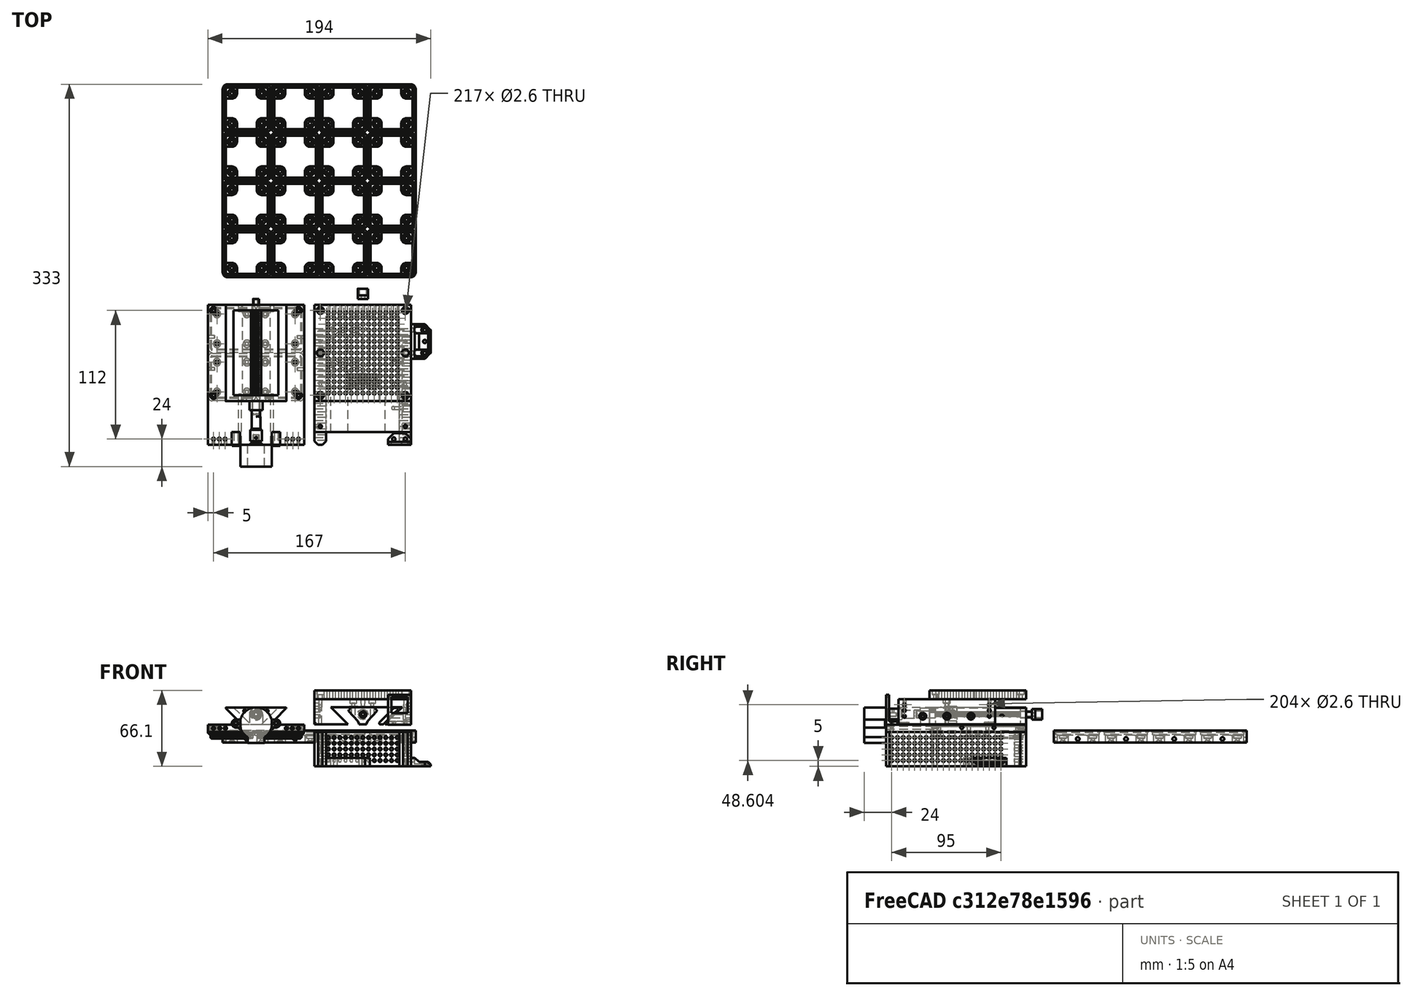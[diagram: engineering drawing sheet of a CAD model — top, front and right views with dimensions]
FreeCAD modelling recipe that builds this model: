
FCSTD DOCUMENT  (FreeCAD 1.0R39109 (Git))
Label: Linear Stage Motorised
License: All rights reserved
LicenseURL: https://en.wikipedia.org/wiki/All_rights_reserved
objects: Sketcher::SketchObject×99, PartDesign::Pocket×54, PartDesign::Pad×44, PartDesign::Chamfer×26, PartDesign::Plane×17, PartDesign::Body×16, PartDesign::ShapeBinder×15, PartDesign::Fillet×6, PartDesign::SubShapeBinder×5, PartDesign::Hole×3, PartDesign::FeatureBase×3, PartDesign::LinearPattern×3, PartDesign::Point×1, Part::Part2DObjectPython×1, Part::Helix×1, PartDesign::AdditivePipe×1, Part::FeaturePython×1, App::VarSet×1, PartDesign::FeaturePython×1
note: 671 computed .brp shape members not serialized (recipe doc carries the construction recipe); baked Part::Feature solids carry a one-line shape summary decoded from their .brp

FEATURE [Sketcher::SketchObject] Sketch
  ArcFitTolerance = 1e-06
  AttachmentSupport = -> [XZ_Plane]
  FullyConstrained = true
  MakeInternals = false
  MapMode = 5
  Placement = pos=(0,0,0) rot=(1,0,0;1.5708rad)
  sketch-geometry (8):
    g0: LineSegment StartX=0 StartY=0 StartZ=0 EndX=84 EndY=0 EndZ=0
    g1: LineSegment StartX=0 StartY=0 StartZ=0 EndX=0 EndY=5 EndZ=0
    g2: LineSegment StartX=84 StartY=0 StartZ=0 EndX=84 EndY=5 EndZ=0
    g3: LineSegment StartX=0 StartY=5 StartZ=0 EndX=30 EndY=5 EndZ=0
    g4: LineSegment StartX=84 StartY=5 StartZ=0 EndX=54 EndY=5 EndZ=0
    g5: LineSegment StartX=30 StartY=5 StartZ=0 EndX=15 EndY=20 EndZ=0
    g6: LineSegment StartX=54 StartY=5 StartZ=0 EndX=69 EndY=20 EndZ=0
    g7: LineSegment StartX=15 StartY=20 StartZ=0 EndX=69 EndY=20 EndZ=0
  constraints (24):
    c: Distance(g0) = 84
    c: Distance(g1) = 5
    c: Coincident(g1,g0)
    c: PointOnObject(g1,g-2)
    c: Vertical(g1)
    c: Distance(g2) = 5
    c: Vertical(g2)
    c: Tangent(g0,g-1)
    c: PointOnObject(g2,g0)
    c: PointOnObject(g0,g2)
    c: Coincident(g3,g1)
    c: Horizontal(g3)
    c: Coincident(g4,g2)
    c: Horizontal(g4)
    c: DistanceX(g3,g3) = 30
    c: DistanceX(g4,g4) = 30
    c: Angle(g-1,g5) = 2.35619
    c: Coincident(g5,g3)
    c: Angle(g-1,g6) = 0.785398
    c: Coincident(g6,g4)
    c: DistanceY(g-1,g5) = 20
    c: DistanceY(g-1,g6) = 20
    c: Coincident(g7,g5)
    c: Coincident(g7,g6)
FEATURE [PartDesign::Pad] Pad
  Direction = (0,-1,2e-16)
  Length = 5
  Length2 = 10
  Placement = pos=(0,0,0) rot=(1,0,0;1.5708rad)
  Profile = -> Sketch
  ReferenceAxis = -> Sketch [N_Axis]
  Refine = true
  Suppressed = false
  Type = 0
FEATURE [Sketcher::SketchObject] Sketch001
  ArcFitTolerance = 1e-06
  AttachmentSupport = -> [Pad]
  ExternalGeometry = -> [Pad]
  FullyConstrained = true
  MakeInternals = false
  MapMode = 5
  Placement = pos=(0,-5,0) rot=(1,0,0;1.5708rad)
  sketch-geometry (14):
    g0: LineSegment StartX=15 StartY=20 StartZ=0 EndX=22.5 EndY=20 EndZ=0
    g1: LineSegment [constr] StartX=30 StartY=5 StartZ=0 EndX=37.5 EndY=5 EndZ=0
    g2: LineSegment StartX=22.5 StartY=20 StartZ=0 EndX=37.5 EndY=5 EndZ=0
    g3: LineSegment StartX=69 StartY=20 StartZ=0 EndX=61.5 EndY=20 EndZ=0
    g4: LineSegment [constr] StartX=54 StartY=5 StartZ=0 EndX=46.5 EndY=5 EndZ=0
    g5: LineSegment StartX=46.5 StartY=5 StartZ=0 EndX=61.5 EndY=20 EndZ=0
    g6: LineSegment StartX=46.5 StartY=5 StartZ=0 EndX=37.5 EndY=5 EndZ=0
    g7: LineSegment StartX=15 StartY=20 StartZ=0 EndX=30 EndY=5 EndZ=0
    g8: LineSegment StartX=30 StartY=5 StartZ=0 EndX=0 EndY=5 EndZ=0
    g9: LineSegment StartX=0 StartY=5 StartZ=0 EndX=0 EndY=0 EndZ=0
    g10: LineSegment StartX=0 StartY=0 StartZ=0 EndX=84 EndY=0 EndZ=0
    g11: LineSegment StartX=84 StartY=0 StartZ=0 EndX=84 EndY=5 EndZ=0
    g12: LineSegment StartX=84 StartY=5 StartZ=0 EndX=54 EndY=5 EndZ=0
    g13: LineSegment StartX=54 StartY=5 StartZ=0 EndX=69 EndY=20 EndZ=0
  constraints (32):
    c: Distance(g0) = 7.5
    c: Coincident(g0,g-4)
    c: PointOnObject(g0,g-3)
    c: Distance(g1) = 7.5
    c: Coincident(g1,g-5)
    c: Horizontal(g1)
    c: Coincident(g2,g0)
    c: Coincident(g2,g1)
    c: Distance(g3) = 7.5
    c: Coincident(g3,g-3)
    c: PointOnObject(g3,g-3)
    c: Distance(g4) = 7.5
    c: Coincident(g4,g-6)
    c: Horizontal(g4)
    c: Coincident(g5,g4)
    c: Coincident(g5,g3)
    c: Coincident(g6,g4)
    c: Coincident(g6,g1)
    c: Coincident(g7,g0)
    c: Coincident(g7,g1)
    c: Coincident(g8,g1)
    c: Coincident(g8,g-8)
    c: Coincident(g9,g8)
    c: Coincident(g9,g-1)
    c: Coincident(g10,g9)
    c: Coincident(g10,g-9)
    c: Coincident(g11,g10)
    c: Coincident(g11,g-7)
    c: Coincident(g12,g11)
    c: Coincident(g12,g4)
    c: Coincident(g13,g4)
    c: Coincident(g13,g3)
FEATURE [PartDesign::Pad] Pad001
  BaseFeature = -> Pad
  Direction = (0,-1,2e-16)
  Length = 74
  Length2 = 10
  Placement = pos=(0,0,0) rot=(1,0,0;1.5708rad)
  Profile = -> Sketch001
  ReferenceAxis = -> Sketch001 [N_Axis]
  Refine = true
  Suppressed = false
  Type = 0
FEATURE [Sketcher::SketchObject] Sketch002
  ArcFitTolerance = 1e-06
  AttachmentSupport = -> [Pad001]
  ExternalGeometry = -> [Pad001]
  FullyConstrained = true
  MakeInternals = false
  MapMode = 5
  Placement = pos=(0,-5,0) rot=(1,0,0;1.5708rad)
  sketch-geometry (2):
    g0: LineSegment [constr] StartX=42 StartY=20 StartZ=0 EndX=42 EndY=14 EndZ=0
    g1: Circle CenterX=42 CenterY=14 CenterZ=0 NormalX=0 NormalY=0 NormalZ=1 AngleXU=0 Radius=3
  constraints (5):
    c: Distance(g0) = 6
    c: Symmetric(g-3,g-3,g0)
    c: Vertical(g0)
    c: Diameter(g1) = 6
    c: Coincident(g1,g0)
FEATURE [PartDesign::Hole] Hole
  BaseFeature = -> Pad001
  CustomThreadClearance = 0
  Depth = 25
  DepthType = 0
  Diameter = 6
  DrillForDepth = false
  DrillPoint = 1
  DrillPointAngle = 118
  HoleCutCountersinkAngle = 90
  HoleCutCustomValues = false
  HoleCutDepth = 0
  HoleCutDiameter = 6.1
  HoleCutType = 0
  ModelThread = false
  Placement = pos=(0,0,0) rot=(1,0,0;1.5708rad)
  Profile = -> Sketch002
  Refine = true
  Suppressed = false
  Tapered = false
  TaperedAngle = 90
  ThreadClass = 0
  ThreadDepth = 25
  ThreadDepthType = 0
  ThreadDirection = 0
  ThreadFit = 0
  ThreadSize = 0
  ThreadType = 0
  Threaded = false
  UseCustomThreadClearance = false
FEATURE [Sketcher::SketchObject] Sketch003
  ArcFitTolerance = 1e-06
  AttachmentSupport = -> [Hole]
  ExternalGeometry = -> [Hole]
  FullyConstrained = true
  MakeInternals = false
  MapMode = 5
  Placement = pos=(0,-79,1.74e-14) rot=(1,0,0;1.5708rad)
  sketch-geometry (16):
    g0: LineSegment StartX=15 StartY=20 StartZ=0 EndX=69 EndY=20 EndZ=0
    g1: LineSegment StartX=15 StartY=20 StartZ=0 EndX=30 EndY=5 EndZ=0
    g2: LineSegment StartX=30 StartY=5 StartZ=0 EndX=0 EndY=5 EndZ=0
    g3: LineSegment StartX=0 StartY=5 StartZ=0 EndX=0 EndY=0 EndZ=0
    g4: LineSegment StartX=0 StartY=0 StartZ=0 EndX=84 EndY=0 EndZ=0
    g5: LineSegment StartX=84 StartY=0 StartZ=0 EndX=84 EndY=5 EndZ=0
    g6: LineSegment StartX=84 StartY=5 StartZ=0 EndX=54 EndY=5 EndZ=0
    g7: LineSegment StartX=54 StartY=5 StartZ=0 EndX=69 EndY=20 EndZ=0
    g8: LineSegment [constr] StartX=42 StartY=20 StartZ=0 EndX=42 EndY=14 EndZ=0
    g9: Circle CenterX=42 CenterY=14 CenterZ=0 NormalX=0 NormalY=0 NormalZ=1 AngleXU=0 Radius=3
    g10: LineSegment [constr] StartX=42 StartY=14 StartZ=0 EndX=22.5 EndY=20 EndZ=0
    g11: LineSegment [constr] StartX=42 StartY=14 StartZ=0 EndX=61.5 EndY=20 EndZ=0
    g12: GeomPoint [constr] X=32.25 Y=17 Z=0
    g13: GeomPoint [constr] X=51.75 Y=17 Z=0
    g14: Circle CenterX=32.25 CenterY=17 CenterZ=0 NormalX=0 NormalY=0 NormalZ=1 AngleXU=0 Radius=1.25
    g15: Circle CenterX=51.75 CenterY=17 CenterZ=0 NormalX=0 NormalY=0 NormalZ=1 AngleXU=0 Radius=1.25
  constraints (31):
    c: Coincident(g0,g-4)
    c: Coincident(g0,g-11)
    c: Coincident(g1,g0)
    c: Coincident(g1,g-5)
    c: Coincident(g2,g1)
    c: Coincident(g2,g-6)
    c: Coincident(g3,g2)
    c: Coincident(g3,g-1)
    c: Coincident(g4,g3)
    c: Coincident(g4,g-8)
    c: Coincident(g5,g4)
    c: Coincident(g5,g-9)
    c: Coincident(g6,g5)
    c: Coincident(g6,g-10)
    c: Coincident(g7,g6)
    c: Coincident(g7,g0)
    c: Distance(g8) = 6
    c: Symmetric(g0,g0,g8)
    c: Vertical(g8)
    c: Diameter(g9) = 6
    c: Coincident(g9,g8)
    c: Coincident(g10,g8)
    c: Coincident(g10,g-14)
    c: Coincident(g11,g8)
    c: Coincident(g11,g-12)
    c: Symmetric(g10,g10,g12)
    c: Symmetric(g11,g11,g13)
    c: Diameter(g14) = 2.5
    c: Coincident(g14,g12)
    c: Diameter(g15) = 2.5
    c: Coincident(g15,g13)
FEATURE [PartDesign::Pad] Pad002
  BaseFeature = -> Hole
  Direction = (0,-1,2e-16)
  Length = 5
  Length2 = 10
  Placement = pos=(0,0,0) rot=(1,0,0;1.5708rad)
  Profile = -> Sketch003
  ReferenceAxis = -> Sketch003 [N_Axis]
  Refine = true
  Suppressed = false
  Type = 0
FEATURE [PartDesign::Plane] DatumPlane
  AttachmentSupport = -> [Pad002]
  Length = 131.586
  MapMode = 5
  Placement = pos=(0,0,-5e-16) rot=(1,0,0;3.14159rad)
  ResizeMode = 0
  Width = 139.586
FEATURE [Sketcher::SketchObject] Sketch004
  ArcFitTolerance = 1e-06
  AttachmentSupport = -> [Pad002]
  ExternalGeometry = -> [Pad002]
  FullyConstrained = true
  MakeInternals = false
  MapMode = 5
  Placement = pos=(0,0,-5e-16) rot=(1,0,0;3.14159rad)
  sketch-geometry (23):
    g0: LineSegment [constr] StartX=0 StartY=84 StartZ=0 EndX=84 EndY=0 EndZ=0
    g1: LineSegment [constr] StartX=41.75 StartY=41.75 StartZ=0 EndX=42.25 EndY=41.75 EndZ=0
    g2: LineSegment [constr] StartX=42.25 StartY=41.75 StartZ=0 EndX=42.25 EndY=42.25 EndZ=0
    g3: LineSegment [constr] StartX=42.25 StartY=42.25 StartZ=0 EndX=41.75 EndY=42.25 EndZ=0
    g4: LineSegment [constr] StartX=41.75 StartY=42.25 StartZ=0 EndX=41.75 EndY=41.75 EndZ=0
    g5: GeomPoint [constr] X=42 Y=42 Z=0
    g6: LineSegment [constr] StartX=0 StartY=0 StartZ=0 EndX=84 EndY=84 EndZ=0
    g7: LineSegment StartX=42.25 StartY=42.25 StartZ=0 EndX=83.75 EndY=42.25 EndZ=0
    g8: LineSegment StartX=83.75 StartY=42.25 StartZ=0 EndX=83.75 EndY=83.75 EndZ=0
    g9: LineSegment StartX=83.75 StartY=83.75 StartZ=0 EndX=42.25 EndY=83.75 EndZ=0
    g10: LineSegment StartX=42.25 StartY=83.75 StartZ=0 EndX=42.25 EndY=42.25 EndZ=0
    g11: LineSegment StartX=41.75 StartY=42.25 StartZ=0 EndX=41.75 EndY=83.75 EndZ=0
    g12: LineSegment StartX=41.75 StartY=83.75 StartZ=0 EndX=0.25 EndY=83.75 EndZ=0
    g13: LineSegment StartX=0.25 StartY=83.75 StartZ=0 EndX=0.25 EndY=42.25 EndZ=0
    g14: LineSegment StartX=0.25 StartY=42.25 StartZ=0 EndX=41.75 EndY=42.25 EndZ=0
    g15: LineSegment StartX=42.25 StartY=41.75 StartZ=0 EndX=42.25 EndY=0.25 EndZ=0
    g16: LineSegment StartX=42.25 StartY=0.25 StartZ=0 EndX=83.75 EndY=0.25 EndZ=0
    g17: LineSegment StartX=83.75 StartY=0.25 StartZ=0 EndX=83.75 EndY=41.75 EndZ=0
    g18: LineSegment StartX=83.75 StartY=41.75 StartZ=0 EndX=42.25 EndY=41.75 EndZ=0
    g19: LineSegment StartX=41.75 StartY=41.75 StartZ=0 EndX=0.25 EndY=41.75 EndZ=0
    g20: LineSegment StartX=0.25 StartY=41.75 StartZ=0 EndX=0.25 EndY=0.25 EndZ=0
    g21: LineSegment StartX=0.25 StartY=0.25 StartZ=0 EndX=41.75 EndY=0.25 EndZ=0
    g22: LineSegment StartX=41.75 StartY=0.25 StartZ=0 EndX=41.75 EndY=41.75 EndZ=0
  constraints (61):
    c: Coincident(g0,g-6)
    c: Coincident(g0,g-5)
    c: Coincident(g1,g2)
    c: Coincident(g2,g3)
    c: Coincident(g3,g4)
    c: Coincident(g4,g1)
    c: Horizontal(g1)
    c: Horizontal(g3)
    c: Vertical(g2)
    c: Vertical(g4)
    c: Symmetric(g3,g1,g5)
    c: Distance(g2,g4) = 0.5
    c: Distance(g1,g3) = 0.5
    c: PointOnObject(g5,g0)
    c: Coincident(g6,g-1)
    c: Coincident(g6,g-4)
    c: PointOnObject(g5,g6)
    c: Coincident(g7,g8)
    c: Coincident(g8,g9)
    c: Coincident(g9,g10)
    c: Coincident(g10,g7)
    c: Horizontal(g7)
    c: Horizontal(g9)
    c: Vertical(g8)
    c: Vertical(g10)
    c: Distance(g8,g10) = 41.5
    c: Coincident(g7,g2)
    c: PointOnObject(g8,g6)
    c: Coincident(g11,g12)
    c: Coincident(g12,g13)
    c: Coincident(g13,g14)
    c: Coincident(g14,g11)
    c: Vertical(g11)
    c: Vertical(g13)
    c: Horizontal(g12)
    c: Horizontal(g14)
    c: Distance(g11,g13) = 41.5
    c: Coincident(g11,g3)
    c: PointOnObject(g12,g0)
    c: Coincident(g15,g16)
    c: Coincident(g16,g17)
    c: Coincident(g17,g18)
    c: Coincident(g18,g15)
    c: Vertical(g15)
    c: Vertical(g17)
    c: Horizontal(g16)
    c: Horizontal(g18)
    c: Distance(g15,g17) = 41.5
    c: Coincident(g15,g1)
    c: PointOnObject(g16,g0)
    c: Coincident(g19,g20)
    c: Coincident(g20,g21)
    c: Coincident(g21,g22)
    c: Coincident(g22,g19)
    c: Horizontal(g19)
    c: Horizontal(g21)
    c: Vertical(g20)
    c: Vertical(g22)
    c: Distance(g20,g22) = 41.5
    c: Coincident(g19,g1)
    c: PointOnObject(g20,g6)
FEATURE [PartDesign::Pad] Pad003
  BaseFeature = -> Pad002
  Direction = (0,0,-1)
  Length = 1
  Length2 = 10
  Placement = pos=(0,0,0) rot=(1,0,0;1.5708rad)
  Profile = -> Sketch004
  ReferenceAxis = -> Sketch004 [N_Axis]
  Refine = true
  Suppressed = false
  Type = 0
FEATURE [PartDesign::Plane] DatumPlane001
  AttachmentSupport = -> [Pad003]
  Length = 131.586
  MapMode = 5
  Placement = pos=(0,0,-1) rot=(1,0,0;3.14159rad)
  ResizeMode = 0
  Width = 139.586
FEATURE [Sketcher::SketchObject] Sketch005
  ArcFitTolerance = 1e-06
  AttachmentSupport = -> [DatumPlane001]
  ExternalGeometry = -> [Pad003]
  FullyConstrained = true
  MakeInternals = false
  MapMode = 5
  Placement = pos=(0,0,-1) rot=(1,0,0;3.14159rad)
  sketch-geometry (28):
    g0: LineSegment [constr] StartX=41.75 StartY=42.25 StartZ=0 EndX=0.25 EndY=83.75 EndZ=0
    g1: GeomPoint [constr] X=21 Y=63 Z=0
    g2: LineSegment StartX=2.4 StartY=44.4 StartZ=0 EndX=39.6 EndY=44.4 EndZ=0
    g3: LineSegment StartX=39.6 StartY=44.4 StartZ=0 EndX=39.6 EndY=81.6 EndZ=0
    g4: LineSegment StartX=39.6 StartY=81.6 StartZ=0 EndX=2.4 EndY=81.6 EndZ=0
    g5: LineSegment StartX=2.4 StartY=81.6 StartZ=0 EndX=2.4 EndY=44.4 EndZ=0
    g6: GeomPoint [constr] X=21 Y=63 Z=0
    g7: LineSegment [constr] StartX=42.25 StartY=83.75 StartZ=0 EndX=83.75 EndY=42.25 EndZ=0
    g8: LineSegment [constr] StartX=83.75 StartY=41.75 StartZ=0 EndX=42.25 EndY=0.25 EndZ=0
    g9: LineSegment [constr] StartX=41.75 StartY=0.25 StartZ=0 EndX=0.25 EndY=41.75 EndZ=0
    g10: GeomPoint [constr] X=63 Y=63 Z=0
    g11: GeomPoint [constr] X=63 Y=21 Z=0
    g12: GeomPoint [constr] X=21 Y=21 Z=0
    g13: LineSegment StartX=44.4 StartY=44.4 StartZ=0 EndX=81.6 EndY=44.4 EndZ=0
    g14: LineSegment StartX=81.6 StartY=44.4 StartZ=0 EndX=81.6 EndY=81.6 EndZ=0
    g15: LineSegment StartX=81.6 StartY=81.6 StartZ=0 EndX=44.4 EndY=81.6 EndZ=0
    g16: LineSegment StartX=44.4 StartY=81.6 StartZ=0 EndX=44.4 EndY=44.4 EndZ=0
    g17: GeomPoint [constr] X=63 Y=63 Z=0
    g18: LineSegment StartX=44.4 StartY=2.4 StartZ=0 EndX=81.6 EndY=2.4 EndZ=0
    g19: LineSegment StartX=81.6 StartY=2.4 StartZ=0 EndX=81.6 EndY=39.6 EndZ=0
    g20: LineSegment StartX=81.6 StartY=39.6 StartZ=0 EndX=44.4 EndY=39.6 EndZ=0
    g21: LineSegment StartX=44.4 StartY=39.6 StartZ=0 EndX=44.4 EndY=2.4 EndZ=0
    g22: GeomPoint [constr] X=63 Y=21 Z=0
    g23: LineSegment StartX=2.4 StartY=2.4 StartZ=0 EndX=39.6 EndY=2.4 EndZ=0
    g24: LineSegment StartX=39.6 StartY=2.4 StartZ=0 EndX=39.6 EndY=39.6 EndZ=0
    g25: LineSegment StartX=39.6 StartY=39.6 StartZ=0 EndX=2.4 EndY=39.6 EndZ=0
    g26: LineSegment StartX=2.4 StartY=39.6 StartZ=0 EndX=2.4 EndY=2.4 EndZ=0
    g27: GeomPoint [constr] X=21 Y=21 Z=0
  constraints (60):
    c: Coincident(g0,g-14)
    c: Coincident(g0,g-16)
    c: Symmetric(g0,g0,g1)
    c: Coincident(g2,g3)
    c: Coincident(g3,g4)
    c: Coincident(g4,g5)
    c: Coincident(g5,g2)
    c: Horizontal(g2)
    c: Horizontal(g4)
    c: Vertical(g3)
    c: Vertical(g5)
    c: Symmetric(g4,g2,g6)
    c: Distance(g3,g5) = 37.2
    c: Distance(g2,g4) = 37.2
    c: Coincident(g6,g1)
    c: Coincident(g7,g-18)
    c: Coincident(g7,g-17)
    c: Coincident(g8,g-9)
    c: Coincident(g8,g-10)
    c: Coincident(g9,g-4)
    c: Coincident(g9,g-6)
    c: Symmetric(g7,g7,g10)
    c: Symmetric(g8,g8,g11)
    c: Symmetric(g9,g9,g12)
    c: Coincident(g13,g14)
    c: Coincident(g14,g15)
    c: Coincident(g15,g16)
    c: Coincident(g16,g13)
    c: Horizontal(g13)
    c: Horizontal(g15)
    c: Vertical(g14)
    c: Vertical(g16)
    c: Symmetric(g15,g13,g17)
    c: Distance(g14,g16) = 37.2
    c: Distance(g13,g15) = 37.2
    c: Coincident(g17,g10)
    c: Coincident(g18,g19)
    c: Coincident(g19,g20)
    c: Coincident(g20,g21)
    c: Coincident(g21,g18)
    c: Horizontal(g18)
    c: Horizontal(g20)
    c: Vertical(g19)
    c: Vertical(g21)
    c: Symmetric(g20,g18,g22)
    c: Distance(g19,g21) = 37.2
    c: Coincident(g22,g11)
    c: PointOnObject(g19,g8)
    c: Coincident(g23,g24)
    c: Coincident(g24,g25)
    c: Coincident(g25,g26)
    c: Coincident(g26,g23)
    c: Horizontal(g23)
    c: Horizontal(g25)
    c: Vertical(g24)
    c: Vertical(g26)
    c: Symmetric(g25,g23,g27)
    c: Distance(g24,g26) = 37.2
    c: Distance(g23,g25) = 37.2
    c: Coincident(g27,g12)
FEATURE [PartDesign::Pad] Pad004
  BaseFeature = -> Pad003
  Direction = (0,0,-1)
  Length = 3.5
  Length2 = 10
  Placement = pos=(0,0,0) rot=(1,0,0;1.5708rad)
  Profile = -> Sketch005
  ReferenceAxis = -> Sketch005 [N_Axis]
  Refine = true
  Suppressed = false
  Type = 0
FEATURE [PartDesign::Chamfer] Chamfer
  Angle = 45
  Base = -> Pad004 [Edge114]
  BaseFeature = -> Pad004
  ChamferType = 0
  FlipDirection = false
  Placement = pos=(0,0,0) rot=(1,0,0;1.5708rad)
  Refine = true
  Size = 7
  Size2 = 1
  SupportTransform = false
  Suppressed = false
  UseAllEdges = false
FEATURE [PartDesign::Chamfer] Chamfer001
  Angle = 45
  Base = -> Chamfer [Edge23]
  BaseFeature = -> Chamfer
  ChamferType = 0
  FlipDirection = false
  Placement = pos=(0,0,0) rot=(1,0,0;1.5708rad)
  Refine = true
  Size = 7
  Size2 = 1
  SupportTransform = false
  Suppressed = false
  UseAllEdges = false
FEATURE [PartDesign::Chamfer] Chamfer002
  Angle = 45
  Base = -> Chamfer001 [Edge136,Edge28,Edge143,Edge22,Edge135,Edge128,Edge144,Edge148,Edge140,Edge127,Edge132,Edge138,Edge26,Edge130]
  BaseFeature = -> Chamfer001
  ChamferType = 0
  FlipDirection = false
  Placement = pos=(0,0,0) rot=(1,0,0;1.5708rad)
  Refine = true
  Size = 7
  Size2 = 1
  SupportTransform = false
  Suppressed = false
  UseAllEdges = false
FEATURE [PartDesign::Chamfer] Chamfer003
  Angle = 45
  Base = -> Chamfer002 [Edge77,Edge79,Edge93,Edge81,Edge95,Edge38,Edge76,Edge32,Edge92,Edge84,Edge97,Edge85,Edge87,Edge89,Edge35]
  BaseFeature = -> Chamfer002
  ChamferType = 0
  FlipDirection = false
  Placement = pos=(0,0,0) rot=(1,0,0;1.5708rad)
  Refine = true
  Size = 8
  Size2 = 1
  SupportTransform = false
  Suppressed = false
  UseAllEdges = false
FEATURE [PartDesign::Chamfer] Chamfer004
  Angle = 45
  Base = -> Chamfer003 [Edge231]
  BaseFeature = -> Chamfer003
  ChamferType = 0
  FlipDirection = false
  Placement = pos=(0,0,0) rot=(1,0,0;1.5708rad)
  Refine = true
  Size = 7
  Size2 = 1
  SupportTransform = false
  Suppressed = false
  UseAllEdges = false
FEATURE [PartDesign::Chamfer] Chamfer005
  Angle = 45
  Base = -> Chamfer004 [Edge1,Edge2,Edge4,Edge6,Edge8,Edge7,Edge5,Edge3]
  BaseFeature = -> Chamfer004
  ChamferType = 0
  FlipDirection = false
  Placement = pos=(0,0,0) rot=(1,0,0;1.5708rad)
  Refine = true
  Size = 2
  Size2 = 1
  SupportTransform = false
  Suppressed = false
  UseAllEdges = false
FEATURE [PartDesign::Chamfer] Chamfer006
  Angle = 45
  Base = -> Chamfer005 [Edge60,Edge64,Edge62,Edge58,Edge55,Edge50,Edge52,Edge56]
  BaseFeature = -> Chamfer005
  ChamferType = 0
  FlipDirection = false
  Placement = pos=(0,0,0) rot=(1,0,0;1.5708rad)
  Refine = true
  Size = 0.8
  Size2 = 1
  SupportTransform = false
  Suppressed = false
  UseAllEdges = false
FEATURE [PartDesign::Chamfer] Chamfer007
  Angle = 45
  Base = -> Chamfer006 [Edge207,Edge208,Edge205,Edge206,Edge204,Edge202,Edge203,Edge201]
  BaseFeature = -> Chamfer006
  ChamferType = 0
  FlipDirection = false
  Placement = pos=(0,0,0) rot=(1,0,0;1.5708rad)
  Refine = true
  Size = 2
  Size2 = 1
  SupportTransform = false
  Suppressed = false
  UseAllEdges = false
FEATURE [PartDesign::Chamfer] Chamfer008
  Angle = 45
  Base = -> Chamfer007 [Edge63,Edge64,Edge60,Edge57,Edge52,Edge50,Edge55,Edge59]
  BaseFeature = -> Chamfer007
  ChamferType = 0
  FlipDirection = false
  Placement = pos=(0,0,0) rot=(1,0,0;1.5708rad)
  Refine = true
  Size = 0.8
  Size2 = 1
  SupportTransform = false
  Suppressed = false
  UseAllEdges = false
FEATURE [PartDesign::Chamfer] Chamfer009
  Angle = 45
  Base = -> Chamfer008 [Edge179,Edge177,Edge178,Edge181,Edge180,Edge182,Edge184,Edge183]
  BaseFeature = -> Chamfer008
  ChamferType = 0
  FlipDirection = false
  Placement = pos=(0,0,0) rot=(1,0,0;1.5708rad)
  Refine = true
  Size = 2
  Size2 = 1
  SupportTransform = false
  Suppressed = false
  UseAllEdges = false
FEATURE [PartDesign::Chamfer] Chamfer010
  Angle = 45
  Base = -> Chamfer009 [Edge55,Edge58,Edge62,Edge64,Edge61,Edge56,Edge53,Edge50]
  BaseFeature = -> Chamfer009
  ChamferType = 0
  FlipDirection = false
  Placement = pos=(0,0,0) rot=(1,0,0;1.5708rad)
  Refine = true
  Size = 0.8
  Size2 = 1
  SupportTransform = false
  Suppressed = false
  UseAllEdges = false
FEATURE [PartDesign::Chamfer] Chamfer011
  Angle = 45
  Base = -> Chamfer010 [Edge203,Edge205,Edge201,Edge202,Edge204,Edge206,Edge208,Edge207]
  BaseFeature = -> Chamfer010
  ChamferType = 0
  FlipDirection = false
  Placement = pos=(0,0,0) rot=(1,0,0;1.5708rad)
  Refine = true
  Size = 2
  Size2 = 1
  SupportTransform = false
  Suppressed = false
  UseAllEdges = false
FEATURE [PartDesign::Chamfer] Chamfer012
  Angle = 45
  Base = -> Chamfer011 [Edge62,Edge59,Edge54,Edge50,Edge53,Edge56,Edge61,Edge64]
  BaseFeature = -> Chamfer011
  ChamferType = 0
  FlipDirection = false
  Placement = pos=(0,0,0) rot=(1,0,0;1.5708rad)
  Refine = true
  Size = 0.8
  Size2 = 1
  SupportTransform = false
  Suppressed = false
  UseAllEdges = false
FEATURE [PartDesign::Fillet] Fillet
  Base = -> Chamfer012 [Edge188,Edge187]
  BaseFeature = -> Chamfer012
  Placement = pos=(0,0,0) rot=(1,0,0;1.5708rad)
  Radius = 0.5
  Refine = true
  SupportTransform = false
  Suppressed = false
  UseAllEdges = false
FEATURE [PartDesign::ShapeBinder] ShapeBinder
  Support = -> [Fillet]
  TraceSupport = false
FEATURE [PartDesign::ShapeBinder] CopyFillet
  Placement = pos=(0,-5,2e-15) rot=(0,0,1;0rad)
  TraceSupport = false
FEATURE [PartDesign::Plane] DatumPlane002
  AttachmentSupport = -> [CopyFillet]
  Length = 111.71
  MapMode = 5
  Placement = pos=(0,-84,2e-15) rot=(1,0,0;1.5708rad)
  ResizeMode = 0
  Width = 63.9806
FEATURE [Sketcher::SketchObject] Sketch006
  ArcFitTolerance = 1e-06
  AttachmentSupport = -> [DatumPlane002]
  ExternalGeometry = -> [ShapeBinder]
  FullyConstrained = true
  MakeInternals = false
  MapMode = 5
  Placement = pos=(0,-84,2e-15) rot=(1,0,0;1.5708rad)
  sketch-geometry (16):
    g0: LineSegment [constr] StartX=68.1465 StartY=19.1464 StartZ=0 EndX=69 EndY=20 EndZ=0
    g1: LineSegment [constr] StartX=67.7929 StartY=20 StartZ=0 EndX=69 EndY=20 EndZ=0
    g2: LineSegment [constr] StartX=69 StartY=20 StartZ=0 EndX=69.5 EndY=20 EndZ=0
    g3: LineSegment [constr] StartX=69.5 StartY=20 StartZ=0 EndX=74.5 EndY=20 EndZ=0
    g4: LineSegment [constr] StartX=54 StartY=5 StartZ=0 EndX=54.5 EndY=5 EndZ=0
    g5: LineSegment [constr] StartX=54.5 StartY=5 StartZ=0 EndX=59.5 EndY=5 EndZ=0
    g6: LineSegment [constr] StartX=59.5 StartY=5 StartZ=0 EndX=74.5 EndY=20 EndZ=0
    g7: LineSegment [constr] StartX=54.5 StartY=5 StartZ=0 EndX=69.5 EndY=20 EndZ=0
    g8: LineSegment [constr] StartX=59.5 StartY=5 StartZ=0 EndX=59.8536 EndY=5.35355 EndZ=0
    g9: LineSegment [constr] StartX=54.5 StartY=5 StartZ=0 EndX=54.8536 EndY=5.35355 EndZ=0
    g10: LineSegment [constr] StartX=74.5 StartY=20 StartZ=0 EndX=74.1465 EndY=19.6464 EndZ=0
    g11: LineSegment [constr] StartX=69.5 StartY=20 StartZ=0 EndX=69.1465 EndY=19.6464 EndZ=0
    g12: LineSegment StartX=54.8536 StartY=5.35355 StartZ=0 EndX=59.8536 EndY=5.35355 EndZ=0
    g13: LineSegment StartX=59.8536 StartY=5.35355 StartZ=0 EndX=74.1465 EndY=19.6464 EndZ=0
    g14: LineSegment StartX=74.1465 StartY=19.6464 StartZ=0 EndX=69.1465 EndY=19.6464 EndZ=0
    g15: LineSegment StartX=69.1465 StartY=19.6464 StartZ=0 EndX=54.8536 EndY=5.35355 EndZ=0
  constraints (41):
    c: Coincident(g0,g-3)
    c: Coincident(g1,g-4)
    c: Coincident(g1,g0)
    c: Angle(g-4,g1) = 3.14159
    c: Angle(g-3,g0) = 3.14159
    c: Distance(g2) = 0.5
    c: Coincident(g2,g0)
    c: Horizontal(g2)
    c: Distance(g3) = 5
    c: Coincident(g3,g2)
    c: Horizontal(g3)
    c: Distance(g4) = 0.5
    c: Coincident(g4,g-3)
    c: Horizontal(g4)
    c: Distance(g5) = 5
    c: Coincident(g5,g4)
    c: Horizontal(g5)
    c: Coincident(g6,g5)
    c: Coincident(g6,g3)
    c: Coincident(g7,g4)
    c: Coincident(g7,g2)
    c: Distance(g8) = 0.5
    c: Coincident(g8,g5)
    c: PointOnObject(g8,g6)
    c: Distance(g9) = 0.5
    c: Coincident(g9,g4)
    c: PointOnObject(g9,g7)
    c: Distance(g10) = 0.5
    c: Coincident(g10,g3)
    c: PointOnObject(g10,g6)
    c: Distance(g11) = 0.5
    c: Coincident(g11,g2)
    c: PointOnObject(g11,g7)
    c: Coincident(g12,g9)
    c: Coincident(g12,g8)
    c: Coincident(g13,g8)
    c: Coincident(g13,g10)
    c: Coincident(g14,g10)
    c: Coincident(g14,g11)
    c: Coincident(g15,g11)
    c: Coincident(g15,g9)
FEATURE [PartDesign::Pad] Pad005
  Direction = (0,-1,2e-16)
  Length = 84
  Length2 = 10
  Placement = pos=(0,-84,2e-15) rot=(1,0,0;1.5708rad)
  Profile = -> Sketch006
  ReferenceAxis = -> Sketch006 [N_Axis]
  Refine = true
  Reversed = true
  Suppressed = false
  Type = 0
FEATURE [PartDesign::Plane] DatumPlane003
  AttachmentSupport = -> [Pad005]
  Length = 125.801
  MapMode = 5
  Placement = pos=(27.25,-84,-27.25) rot=(0.92388,0,0.382683;3.14159rad)
  ResizeMode = 0
  Width = 130.341
FEATURE [Sketcher::SketchObject] Sketch007
  ArcFitTolerance = 1e-06
  AttachmentSupport = -> [DatumPlane003]
  ExternalGeometry = -> [Pad005]
  FullyConstrained = true
  MakeInternals = false
  MapMode = 5
  Placement = pos=(27.25,-84,-27.25) rot=(0.92388,0,0.382683;3.14159rad)
  sketch-geometry (8):
    g0: LineSegment [constr] StartX=46.1084 StartY=-42 StartZ=0 EndX=66.3216 EndY=-42 EndZ=0
    g1: LineSegment [constr] StartX=56.215 StartY=-42 StartZ=0 EndX=56.215 EndY=-1.42e-14 EndZ=0
    g2: LineSegment [constr] StartX=56.215 StartY=-42 StartZ=0 EndX=56.215 EndY=-84 EndZ=0
    g3: GeomPoint [constr] X=56.215 Y=-63 Z=0
    g4: GeomPoint [constr] X=56.215 Y=-21 Z=0
    g5: Circle CenterX=56.215 CenterY=-21 CenterZ=0 NormalX=0 NormalY=0 NormalZ=1 AngleXU=0 Radius=1.55
    g6: Circle CenterX=56.215 CenterY=-42 CenterZ=0 NormalX=0 NormalY=0 NormalZ=1 AngleXU=0 Radius=1.55
    g7: Circle CenterX=56.215 CenterY=-63 CenterZ=0 NormalX=0 NormalY=0 NormalZ=1 AngleXU=0 Radius=1.55
  constraints (14):
    c: Symmetric(g-4,g-4,g0)
    c: Symmetric(g-3,g-3,g0)
    c: Symmetric(g0,g0,g1)
    c: Symmetric(g-5,g-5,g1)
    c: Coincident(g2,g1)
    c: Symmetric(g-6,g-6,g2)
    c: Symmetric(g2,g2,g3)
    c: Symmetric(g1,g1,g4)
    c: Diameter(g5) = 3.1
    c: Coincident(g5,g4)
    c: Diameter(g6) = 3.1
    c: Coincident(g6,g1)
    c: Diameter(g7) = 3.1
    c: Coincident(g7,g3)
FEATURE [PartDesign::Pocket] Pocket
  BaseFeature = -> Pad005
  Direction = (-0.707107,0,0.707107)
  Length = 1
  Length2 = 5
  Placement = pos=(0,-84,2e-15) rot=(1,0,0;1.5708rad)
  Profile = -> Sketch007
  ReferenceAxis = -> Sketch007 [N_Axis]
  Refine = true
  Suppressed = false
  Type = 0
FEATURE [PartDesign::Fillet] Fillet001
  Base = -> Pocket [Edge5,Edge10,Edge1,Edge2]
  BaseFeature = -> Pocket
  Placement = pos=(0,-84,2e-15) rot=(1,0,0;1.5708rad)
  Radius = 1
  Refine = true
  SupportTransform = false
  Suppressed = false
  UseAllEdges = false
FEATURE [PartDesign::Fillet] Fillet002
  Base = -> Fillet001 [Edge24,Edge25,Edge23]
  BaseFeature = -> Fillet001
  Placement = pos=(0,-84,2e-15) rot=(1,0,0;1.5708rad)
  Radius = 0.3
  Refine = true
  SupportTransform = false
  Suppressed = false
  UseAllEdges = false
FEATURE [PartDesign::Fillet] Fillet003
  Base = -> Fillet002 [Edge31,Edge37,Edge39]
  BaseFeature = -> Fillet002
  Placement = pos=(0,-84,2e-15) rot=(1,0,0;1.5708rad)
  Radius = 0.3
  Refine = true
  SupportTransform = false
  Suppressed = false
  UseAllEdges = false
FEATURE [PartDesign::Body] Body001  label="Shim"
  AllowCompound = false
  Group = -> [ShapeBinder,DatumPlane002,CopyFillet,Sketch006,Pad005,DatumPlane003,Sketch007,Pocket,Fillet001,Fillet002,Fillet003]
  Origin = -> Origin001
  Tip = -> Fillet003
FEATURE [PartDesign::ShapeBinder] ShapeBinder001
  Support = -> [Fillet]
  TraceSupport = false
FEATURE [PartDesign::ShapeBinder] CopyFillet001
  Placement = pos=(0,-5,2e-15) rot=(0,0,1;0rad)
  TraceSupport = false
FEATURE [PartDesign::Plane] DatumPlane004
  AttachmentSupport = -> [CopyFillet001]
  Length = 124.108
  MapMode = 5
  Placement = pos=(0,-84,2e-15) rot=(1,0,0;1.5708rad)
  ResizeMode = 0
  Width = 67.4619
FEATURE [Sketcher::SketchObject] Sketch008
  ArcFitTolerance = 1e-06
  AttachmentSupport = -> [DatumPlane004]
  ExternalGeometry = -> [ShapeBinder001]
  FullyConstrained = true
  MakeInternals = false
  MapMode = 5
  Placement = pos=(0,-84,2e-15) rot=(1,0,0;1.5708rad)
  sketch-geometry (21):
    g0: LineSegment [constr] StartX=54 StartY=5 StartZ=0 EndX=61 EndY=5 EndZ=0
    g1: LineSegment [constr] StartX=68.1465 StartY=19.1464 StartZ=0 EndX=69 EndY=20 EndZ=0
    g2: LineSegment [constr] StartX=67.7929 StartY=20 StartZ=0 EndX=69 EndY=20 EndZ=0
    g3: LineSegment [constr] StartX=69 StartY=20 StartZ=0 EndX=76 EndY=20 EndZ=0
    g4: LineSegment [constr] StartX=61 StartY=5 StartZ=0 EndX=61.3536 EndY=5.35355 EndZ=0
    g5: LineSegment [constr] StartX=76 StartY=20 StartZ=0 EndX=76.3536 EndY=20.3536 EndZ=0
    g6: LineSegment StartX=76.3536 StartY=20.3536 StartZ=0 EndX=61.3536 EndY=5.35355 EndZ=0
    g7: LineSegment [constr] StartX=84 StartY=5 StartZ=0 EndX=84 EndY=5.5 EndZ=0
    g8: LineSegment StartX=61.3536 StartY=5.35355 StartZ=0 EndX=84 EndY=5.35355 EndZ=0
    g9: LineSegment StartX=84 StartY=5.35355 StartZ=0 EndX=84 EndY=25.3536 EndZ=0
    g10: LineSegment [constr] StartX=30 StartY=5 StartZ=0 EndX=29.5 EndY=5 EndZ=0
    g11: LineSegment [constr] StartX=16.2071 StartY=20 StartZ=0 EndX=14.5 EndY=20 EndZ=0
    g12: LineSegment [constr] StartX=29.5 StartY=5 StartZ=0 EndX=14.5 EndY=20 EndZ=0
    g13: LineSegment [constr] StartX=14.5 StartY=20 StartZ=0 EndX=14.1465 EndY=20.3536 EndZ=0
    g14: LineSegment [constr] StartX=29.5 StartY=5 StartZ=0 EndX=29.1464 EndY=5.35355 EndZ=0
    g15: LineSegment StartX=29.1464 StartY=5.35355 StartZ=0 EndX=14.1465 EndY=20.3536 EndZ=0
    g16: LineSegment [constr] StartX=0 StartY=5 StartZ=0 EndX=0 EndY=15 EndZ=0
    g17: LineSegment StartX=29.1464 StartY=5.35355 StartZ=0 EndX=0 EndY=5.35355 EndZ=0
    g18: LineSegment StartX=0 StartY=5.35355 StartZ=0 EndX=0 EndY=25.3536 EndZ=0
    g19: LineSegment StartX=0 StartY=25.3536 StartZ=0 EndX=84 EndY=25.3536 EndZ=0
    g20: LineSegment StartX=14.1465 StartY=20.3536 StartZ=0 EndX=76.3536 EndY=20.3536 EndZ=0
  constraints (58):
    c: Distance(g0) = 7
    c: Coincident(g0,g-8)
    c: PointOnObject(g0,g-8)
    c: Coincident(g1,g-7)
    c: Coincident(g2,g-6)
    c: Coincident(g2,g1)
    c: Parallel(g2,g-6)
    c: Parallel(g1,g-7)
    c: Distance(g3) = 7
    c: Coincident(g3,g1)
    c: Parallel(g3,g-6)
    c: Distance(g4) = 0.5
    c: Coincident(g4,g0)
    c: Parallel(g-7,g4)
    c: Distance(g5) = 0.5
    c: Coincident(g5,g3)
    c: Parallel(g5,g1)
    c: Coincident(g6,g5)
    c: Coincident(g6,g4)
    c: Distance(g7) = 0.5
    c: Coincident(g7,g-9)
    c: Vertical(g7)
    c: Coincident(g8,g4)
    c: PointOnObject(g8,g7)
    c: Horizontal(g8)
    c: Distance(g9) = 20
    c: Coincident(g9,g8)
    c: Vertical(g9)
    c: Distance(g10) = 0.5
    c: Coincident(g10,g-5)
    c: PointOnObject(g10,g-3)
    c: Coincident(g11,g-6)
    c: Horizontal(g11)
    c: Coincident(g12,g10)
    c: PointOnObject(g12,g11)
    c: Parallel(g12,g-5)
    c: PointOnObject(g11,g12)
    c: Distance(g13) = 0.5
    c: Coincident(g13,g11)
    c: Parallel(g12,g13)
    c: Distance(g14) = 0.5
    c: Coincident(g14,g10)
    c: PointOnObject(g14,g12)
    c: Coincident(g15,g14)
    c: Coincident(g15,g13)
    c: Distance(g16) = 10
    c: Coincident(g16,g-4)
    c: PointOnObject(g16,g-2)
    c: Coincident(g17,g14)
    c: PointOnObject(g17,g16)
    c: Parallel(g17,g-3)
    c: Distance(g18) = 20
    c: Coincident(g18,g17)
    c: PointOnObject(g18,g-2)
    c: Coincident(g19,g18)
    c: Coincident(g19,g9)
    c: Coincident(g20,g13)
    c: Coincident(g20,g5)
FEATURE [PartDesign::Pad] Pad006
  Direction = (0,-1,2e-16)
  Length = 84
  Length2 = 10
  Placement = pos=(0,-84,2e-15) rot=(1,0,0;1.5708rad)
  Profile = -> Sketch008
  ReferenceAxis = -> Sketch008 [N_Axis]
  Refine = true
  Reversed = true
  Suppressed = false
  Type = 0
FEATURE [Sketcher::SketchObject] Sketch009
  ArcFitTolerance = 1e-06
  AttachmentSupport = -> [Pad006]
  ExternalGeometry = -> [Pad006]
  FullyConstrained = true
  MakeInternals = false
  MapMode = 5
  Placement = pos=(84,-84,2e-15) rot=(0.707107,0,0.707107;3.14159rad)
  sketch-geometry (11):
    g0: GeomPoint [constr] X=25.3536 Y=-42 Z=0
    g1: GeomPoint [constr] X=5.35355 Y=-42 Z=0
    g2: LineSegment [constr] StartX=5.35355 StartY=-42 StartZ=0 EndX=25.3536 EndY=-42 EndZ=0
    g3: LineSegment [constr] StartX=5.35355 StartY=-42 StartZ=0 EndX=12.3536 EndY=-42 EndZ=0
    g4: LineSegment [constr] StartX=12.3536 StartY=-42 StartZ=0 EndX=12.3536 EndY=-7.1e-15 EndZ=0
    g5: LineSegment [constr] StartX=12.3536 StartY=-42 StartZ=0 EndX=12.3536 EndY=-84 EndZ=0
    g6: GeomPoint [constr] X=12.3536 Y=-21 Z=0
    g7: GeomPoint [constr] X=12.3536 Y=-63 Z=0
    g8: Circle CenterX=12.3536 CenterY=-21 CenterZ=0 NormalX=0 NormalY=0 NormalZ=1 AngleXU=0 Radius=1.325
    g9: Circle CenterX=12.3536 CenterY=-42 CenterZ=0 NormalX=0 NormalY=0 NormalZ=1 AngleXU=0 Radius=1.325
    g10: Circle CenterX=12.3536 CenterY=-63 CenterZ=0 NormalX=0 NormalY=0 NormalZ=1 AngleXU=0 Radius=1.325
  constraints (21):
    c: Symmetric(g-3,g-3,g0)
    c: Symmetric(g-5,g-5,g1)
    c: Coincident(g2,g1)
    c: Coincident(g2,g0)
    c: Distance(g3) = 7
    c: Coincident(g3,g1)
    c: PointOnObject(g3,g2)
    c: Coincident(g4,g3)
    c: PointOnObject(g4,g-6)
    c: Parallel(g4,g-5)
    c: Coincident(g5,g3)
    c: PointOnObject(g5,g-4)
    c: Vertical(g5)
    c: Symmetric(g4,g4,g6)
    c: Symmetric(g5,g5,g7)
    c: Diameter(g8) = 2.65
    c: Coincident(g8,g6)
    c: Diameter(g9) = 2.65
    c: Coincident(g9,g3)
    c: Diameter(g10) = 2.65
    c: Coincident(g10,g7)
FEATURE [PartDesign::Pocket] Pocket001
  BaseFeature = -> Pad006
  Direction = (-1,0,2e-16)
  Length = 20
  Length2 = 5
  Placement = pos=(0,-84,2e-15) rot=(1,0,0;1.5708rad)
  Profile = -> Sketch009
  ReferenceAxis = -> Sketch009 [N_Axis]
  Refine = true
  Suppressed = false
  Type = 0
FEATURE [Sketcher::SketchObject] Sketch010
  ArcFitTolerance = 1e-06
  AttachmentSupport = -> [Pocket001]
  ExternalGeometry = -> [Pocket001]
  FullyConstrained = true
  MakeInternals = false
  MapMode = 5
  Placement = pos=(7.71195e-08,-84,20.3536) rot=(1,0,0;3.14159rad)
  sketch-geometry (8):
    g0: LineSegment [constr] StartX=14.1465 StartY=0 StartZ=0 EndX=41.9965 EndY=0 EndZ=0
    g1: LineSegment [constr] StartX=41.9965 StartY=0 StartZ=0 EndX=41.9965 EndY=-84 EndZ=0
    g2: GeomPoint [constr] X=41.9965 Y=-42 Z=0
    g3: LineSegment StartX=35.4965 StartY=-47 StartZ=0 EndX=48.4965 EndY=-47 EndZ=0
    g4: LineSegment StartX=48.4965 StartY=-47 StartZ=0 EndX=48.4965 EndY=-37 EndZ=0
    g5: LineSegment StartX=48.4965 StartY=-37 StartZ=0 EndX=35.4965 EndY=-37 EndZ=0
    g6: LineSegment StartX=35.4965 StartY=-37 StartZ=0 EndX=35.4965 EndY=-47 EndZ=0
    g7: GeomPoint [constr] X=41.9965 Y=-42 Z=0
  constraints (19):
    c: Distance(g0) = 27.85
    c: Coincident(g0,g-3)
    c: PointOnObject(g0,g-3)
    c: Coincident(g1,g0)
    c: PointOnObject(g1,g-4)
    c: Vertical(g1)
    c: Symmetric(g1,g1,g2)
    c: Coincident(g3,g4)
    c: Coincident(g4,g5)
    c: Coincident(g5,g6)
    c: Coincident(g6,g3)
    c: Horizontal(g3)
    c: Horizontal(g5)
    c: Vertical(g4)
    c: Vertical(g6)
    c: Symmetric(g5,g3,g7)
    c: Distance(g4,g6) = 13
    c: Distance(g3,g5) = 10
    c: Coincident(g7,g2)
FEATURE [PartDesign::Pocket] Pocket002
  BaseFeature = -> Pocket001
  Direction = (3.78899e-09,0,1)
  Length = 0.5
  Length2 = 5
  Placement = pos=(0,-84,2e-15) rot=(1,0,0;1.5708rad)
  Profile = -> Sketch010
  ReferenceAxis = -> Sketch010 [N_Axis]
  Refine = true
  Suppressed = false
  Type = 0
FEATURE [Sketcher::SketchObject] Sketch011
  ArcFitTolerance = 1e-06
  AttachmentSupport = -> [Pocket002]
  FullyConstrained = true
  MakeInternals = false
  MapMode = 5
  Placement = pos=(7.9014e-08,-84,20.8536) rot=(1,0,0;3.14159rad)
  sketch-geometry (2):
    g0: LineSegment [constr] StartX=41.9965 StartY=-37 StartZ=0 EndX=41.9965 EndY=-47 EndZ=0
    g1: Circle CenterX=41.9965 CenterY=-42 CenterZ=0 NormalX=0 NormalY=0 NormalZ=1 AngleXU=0 Radius=1.55
  constraints (4):
    c: Symmetric(g-3,g-3,g0)
    c: Symmetric(g-5,g-5,g0)
    c: Diameter(g1) = 3.1
    c: Symmetric(g0,g0,g1)
FEATURE [PartDesign::Pocket] Pocket003
  BaseFeature = -> Pocket002
  Direction = (3.78899e-09,0,1)
  Length = 5
  Length2 = 5
  Placement = pos=(0,-84,2e-15) rot=(1,0,0;1.5708rad)
  Profile = -> Sketch011
  ReferenceAxis = -> Sketch011 [N_Axis]
  Refine = true
  Suppressed = false
  Type = 0
FEATURE [Sketcher::SketchObject] Sketch012
  ArcFitTolerance = 1e-06
  AttachmentSupport = -> [Pocket003]
  ExternalGeometry = -> [Pocket003]
  FullyConstrained = true
  MakeInternals = false
  MapMode = 5
  Placement = pos=(7.11416e-08,-84,25.3536) rot=(0,0,1;3.14159rad)
  sketch-geometry (20):
    g0: LineSegment [constr] StartX=-84 StartY=1.42e-14 StartZ=0 EndX=-84 EndY=-5 EndZ=0
    g1: LineSegment [constr] StartX=-84 StartY=-5 StartZ=0 EndX=-79 EndY=-5 EndZ=0
    g2: LineSegment [constr] StartX=-79 StartY=-5 StartZ=0 EndX=-79 EndY=1.42e-14 EndZ=0
    g3: LineSegment [constr] StartX=-79 StartY=1.42e-14 StartZ=0 EndX=-84 EndY=1.42e-14 EndZ=0
    g4: LineSegment [constr] StartX=-84 StartY=-84 StartZ=0 EndX=-79 EndY=-84 EndZ=0
    g5: LineSegment [constr] StartX=-79 StartY=-84 StartZ=0 EndX=-79 EndY=-79 EndZ=0
    g6: LineSegment [constr] StartX=-79 StartY=-79 StartZ=0 EndX=-84 EndY=-79 EndZ=0
    g7: LineSegment [constr] StartX=-84 StartY=-79 StartZ=0 EndX=-84 EndY=-84 EndZ=0
    g8: LineSegment [constr] StartX=0 StartY=0 StartZ=0 EndX=-5 EndY=0 EndZ=0
    g9: LineSegment [constr] StartX=-5 StartY=0 StartZ=0 EndX=-5 EndY=-5 EndZ=0
    g10: LineSegment [constr] StartX=-5 StartY=-5 StartZ=0 EndX=0 EndY=-5 EndZ=0
    g11: LineSegment [constr] StartX=0 StartY=-5 StartZ=0 EndX=0 EndY=0 EndZ=0
    g12: LineSegment [constr] StartX=7.11416e-08 StartY=-84 StartZ=0 EndX=7.11416e-08 EndY=-79 EndZ=0
    g13: LineSegment [constr] StartX=7.11416e-08 StartY=-79 StartZ=0 EndX=-5 EndY=-79 EndZ=0
    g14: LineSegment [constr] StartX=-5 StartY=-79 StartZ=0 EndX=-5 EndY=-84 EndZ=0
    g15: LineSegment [constr] StartX=-5 StartY=-84 StartZ=0 EndX=7.11416e-08 EndY=-84 EndZ=0
    g16: Circle CenterX=-79 CenterY=-5 CenterZ=0 NormalX=0 NormalY=0 NormalZ=1 AngleXU=0 Radius=1.35
    g17: Circle CenterX=-79 CenterY=-79 CenterZ=0 NormalX=0 NormalY=0 NormalZ=1 AngleXU=0 Radius=1.35
    g18: Circle CenterX=-5 CenterY=-79 CenterZ=0 NormalX=0 NormalY=0 NormalZ=1 AngleXU=0 Radius=1.35
    g19: Circle CenterX=-5 CenterY=-5 CenterZ=0 NormalX=0 NormalY=0 NormalZ=1 AngleXU=0 Radius=1.35
  constraints (52):
    c: Coincident(g0,g1)
    c: Coincident(g1,g2)
    c: Coincident(g2,g3)
    c: Coincident(g3,g0)
    c: Vertical(g0)
    c: Vertical(g2)
    c: Horizontal(g1)
    c: Horizontal(g3)
    c: Distance(g0,g2) = 5
    c: Distance(g1,g3) = 5
    c: Coincident(g0,g-4)
    c: Coincident(g4,g5)
    c: Coincident(g5,g6)
    c: Coincident(g6,g7)
    c: Coincident(g7,g4)
    c: Horizontal(g4)
    c: Horizontal(g6)
    c: Vertical(g5)
    c: Vertical(g7)
    c: Distance(g5,g7) = 5
    c: Distance(g4,g6) = 5
    c: Coincident(g4,g-6)
    c: Coincident(g8,g9)
    c: Coincident(g9,g10)
    c: Coincident(g10,g11)
    c: Coincident(g11,g8)
    c: Horizontal(g8)
    c: Horizontal(g10)
    c: Vertical(g9)
    c: Vertical(g11)
    c: Distance(g9,g11) = 5
    c: Distance(g8,g10) = 5
    c: Coincident(g8,g-1)
    c: Coincident(g12,g13)
    c: Coincident(g13,g14)
    c: Coincident(g14,g15)
    c: Coincident(g15,g12)
    c: Vertical(g12)
    c: Vertical(g14)
    c: Horizontal(g13)
    c: Horizontal(g15)
    c: Distance(g12,g14) = 5
    c: Distance(g13,g15) = 5
    c: Coincident(g12,g-6)
    c: Diameter(g16) = 2.7
    c: Coincident(g16,g1)
    c: Diameter(g17) = 2.7
    c: Coincident(g17,g5)
    c: Diameter(g18) = 2.7
    c: Coincident(g18,g13)
    c: Diameter(g19) = 2.7
    c: Coincident(g19,g9)
FEATURE [PartDesign::Pocket] Pocket004
  BaseFeature = -> Pocket003
  Direction = (-2.80598e-09,0,-1)
  Length = 5
  Length2 = 5
  Placement = pos=(0,-84,2e-15) rot=(1,0,0;1.5708rad)
  Profile = -> Sketch012
  ReferenceAxis = -> Sketch012 [N_Axis]
  Refine = true
  Suppressed = false
  Type = 0
FEATURE [Sketcher::SketchObject] Sketch013
  ArcFitTolerance = 1e-06
  AttachmentSupport = -> [Pocket004]
  ExternalGeometry = -> [Pocket004]
  FullyConstrained = true
  MakeInternals = false
  MapMode = 5
  Placement = pos=(7.11416e-08,-84,25.3536) rot=(0,0,1;3.14159rad)
  sketch-geometry (4):
    g0: LineSegment [constr] StartX=7.11416e-08 StartY=-42 StartZ=0 EndX=-5 EndY=-42 EndZ=0
    g1: Circle CenterX=-5 CenterY=-42 CenterZ=0 NormalX=0 NormalY=0 NormalZ=1 AngleXU=0 Radius=1.35
    g2: LineSegment [constr] StartX=-84 StartY=-42 StartZ=0 EndX=-79 EndY=-42 EndZ=0
    g3: Circle CenterX=-79 CenterY=-42 CenterZ=0 NormalX=0 NormalY=0 NormalZ=1 AngleXU=0 Radius=1.35
  constraints (10):
    c: Distance(g0) = 5
    c: Symmetric(g-3,g-3,g0)
    c: Horizontal(g0)
    c: Diameter(g1) = 2.7
    c: Coincident(g1,g0)
    c: Distance(g2) = 5
    c: Symmetric(g-4,g-4,g2)
    c: Horizontal(g2)
    c: Diameter(g3) = 2.7
    c: Coincident(g3,g2)
FEATURE [PartDesign::Pocket] Pocket005
  BaseFeature = -> Pocket004
  Direction = (-2.80598e-09,0,-1)
  Length = 22
  Length2 = 5
  Placement = pos=(0,-84,2e-15) rot=(1,0,0;1.5708rad)
  Profile = -> Sketch013
  ReferenceAxis = -> Sketch013 [N_Axis]
  Refine = true
  Suppressed = false
  Type = 0
FEATURE [PartDesign::ShapeBinder] CopyPocket005
  Placement = pos=(0,-84,2e-15) rot=(1,0,0;1.5708rad)
  TraceSupport = false
FEATURE [PartDesign::Plane] DatumPlane005
  AttachmentSupport = -> [CopyPocket005]
  Length = 91.117
  MapMode = 5
  Placement = pos=(7.9014e-08,-84,20.8536) rot=(1,0,0;3.14159rad)
  ResizeMode = 0
  Width = 126.87
FEATURE [Sketcher::SketchObject] Sketch014
  ArcFitTolerance = 1e-06
  AttachmentSupport = -> [DatumPlane005]
  FullyConstrained = true
  MakeInternals = false
  MapMode = 5
  Placement = pos=(7.9014e-08,-84,20.8536) rot=(1,0,0;3.14159rad)
  sketch-geometry (6):
    g0: Circle CenterX=41.9965 CenterY=-42 CenterZ=0 NormalX=0 NormalY=0 NormalZ=1 AngleXU=0 Radius=1.35
    g1: LineSegment StartX=35.7465 StartY=-46.75 StartZ=0 EndX=48.2465 EndY=-46.75 EndZ=0
    g2: LineSegment StartX=48.2465 StartY=-46.75 StartZ=0 EndX=48.2465 EndY=-37.25 EndZ=0
    g3: LineSegment StartX=48.2465 StartY=-37.25 StartZ=0 EndX=35.7465 EndY=-37.25 EndZ=0
    g4: LineSegment StartX=35.7465 StartY=-37.25 StartZ=0 EndX=35.7465 EndY=-46.75 EndZ=0
    g5: GeomPoint [constr] X=41.9965 Y=-42 Z=0
  constraints (14):
    c: Diameter(g0) = 2.7
    c: Coincident(g0,g-4)
    c: Coincident(g1,g2)
    c: Coincident(g2,g3)
    c: Coincident(g3,g4)
    c: Coincident(g4,g1)
    c: Horizontal(g1)
    c: Horizontal(g3)
    c: Vertical(g2)
    c: Vertical(g4)
    c: Symmetric(g3,g1,g5)
    c: Distance(g2,g4) = 12.5
    c: Distance(g1,g3) = 9.5
    c: Coincident(g5,g0)
FEATURE [PartDesign::Pad] Pad007
  Direction = (-3.78899e-09,0,-1)
  Length = 3
  Length2 = 10
  Placement = pos=(7.9014e-08,-84,20.8536) rot=(1,0,0;3.14159rad)
  Profile = -> Sketch014
  ReferenceAxis = -> Sketch014 [N_Axis]
  Refine = true
  Suppressed = false
  Type = 0
FEATURE [Sketcher::SketchObject] Sketch015
  ArcFitTolerance = 1e-06
  AttachmentSupport = -> [Pad007]
  ExternalGeometry = -> [Pad007]
  FullyConstrained = true
  MakeInternals = false
  MapMode = 5
  Placement = pos=(6.7647e-08,-84,17.8536) rot=(1,0,0;3.14159rad)
  sketch-geometry (4):
    g0: LineSegment StartX=35.7465 StartY=-37.25 StartZ=0 EndX=35.7465 EndY=-46.75 EndZ=0
    g1: LineSegment StartX=35.7465 StartY=-46.75 StartZ=0 EndX=48.2465 EndY=-46.75 EndZ=0
    g2: LineSegment StartX=48.2465 StartY=-46.75 StartZ=0 EndX=48.2465 EndY=-37.25 EndZ=0
    g3: LineSegment StartX=48.2465 StartY=-37.25 StartZ=0 EndX=35.7465 EndY=-37.25 EndZ=0
  constraints (10):
    c: Coincident(g0,g1)
    c: Coincident(g1,g2)
    c: Coincident(g2,g3)
    c: Coincident(g3,g0)
    c: Vertical(g0)
    c: Vertical(g2)
    c: Horizontal(g1)
    c: Horizontal(g3)
    c: Coincident(g0,g-6)
    c: Coincident(g1,g-5)
FEATURE [PartDesign::Pad] Pad008
  BaseFeature = -> Pad007
  Direction = (-3.78899e-09,0,-1)
  Length = 8
  Length2 = 10
  Placement = pos=(7.9014e-08,-84,20.8536) rot=(1,0,0;3.14159rad)
  Profile = -> Sketch015
  ReferenceAxis = -> Sketch015 [N_Axis]
  Refine = true
  Suppressed = false
  Type = 0
FEATURE [Sketcher::SketchObject] Sketch016
  ArcFitTolerance = 1e-06
  AttachmentSupport = -> [Pad008]
  ExternalGeometry = -> [Pad008]
  FullyConstrained = true
  MakeInternals = false
  MapMode = 5
  Placement = pos=(7.9014e-08,-46.75,20.8536) rot=(0,0.707107,-0.707107;3.14159rad)
  sketch-geometry (2):
    g0: LineSegment [constr] StartX=-41.9965 StartY=0 StartZ=0 EndX=-41.9965 EndY=7 EndZ=0
    g1: Circle CenterX=-41.9965 CenterY=7 CenterZ=0 NormalX=0 NormalY=0 NormalZ=1 AngleXU=0 Radius=2.5
  constraints (5):
    c: Distance(g0) = 7
    c: Symmetric(g-6,g-6,g0)
    c: Vertical(g0)
    c: Diameter(g1) = 5
    c: Coincident(g1,g0)
FEATURE [PartDesign::Hole] Hole001
  BaseFeature = -> Pad008
  CustomThreadClearance = 0
  Depth = 12.72
  DepthType = 0
  Diameter = 4.2
  DrillForDepth = false
  DrillPoint = 1
  DrillPointAngle = 118
  HoleCutCountersinkAngle = 90
  HoleCutCustomValues = false
  HoleCutDepth = 0
  HoleCutDiameter = 6.1
  HoleCutType = 0
  ModelThread = false
  Placement = pos=(7.9014e-08,-84,20.8536) rot=(1,0,0;3.14159rad)
  Profile = -> Sketch016
  Refine = true
  Suppressed = false
  Tapered = false
  TaperedAngle = 90
  ThreadClass = 0
  ThreadDepth = 12.72
  ThreadDepthType = 0
  ThreadDirection = 0
  ThreadFit = 0
  ThreadSize = 13
  ThreadType = 1
  Threaded = true
  UseCustomThreadClearance = false
FEATURE [Sketcher::SketchObject] Sketch017
  ArcFitTolerance = 1e-06
  AttachmentSupport = -> [Hole001]
  ExternalGeometry = -> [Hole001]
  FullyConstrained = true
  MakeInternals = false
  MapMode = 5
  Placement = pos=(7.9014e-08,-46.75,20.8536) rot=(0,0.707107,-0.707107;3.14159rad)
  sketch-geometry (4):
    g0: LineSegment [constr] StartX=-48.2465 StartY=0 StartZ=0 EndX=-48.2465 EndY=2.5 EndZ=0
    g1: LineSegment [constr] StartX=-35.7465 StartY=0 StartZ=0 EndX=-35.7465 EndY=2.5 EndZ=0
    g2: Circle CenterX=-48.2465 CenterY=2.5 CenterZ=0 NormalX=0 NormalY=0 NormalZ=1 AngleXU=0 Radius=1
    g3: Circle CenterX=-35.7465 CenterY=2.5 CenterZ=0 NormalX=0 NormalY=0 NormalZ=1 AngleXU=0 Radius=1
  constraints (10):
    c: Distance(g0) = 2.5
    c: Coincident(g0,g-6)
    c: PointOnObject(g0,g-3)
    c: Distance(g1) = 2.5
    c: Coincident(g1,g-6)
    c: PointOnObject(g1,g-5)
    c: Diameter(g2) = 2
    c: Coincident(g2,g0)
    c: Diameter(g3) = 2
    c: Coincident(g3,g1)
FEATURE [PartDesign::Pocket] Pocket006
  BaseFeature = -> Hole001
  Direction = (0,1,2e-16)
  Length = 10
  Length2 = 5
  Placement = pos=(7.9014e-08,-84,20.8536) rot=(1,0,0;3.14159rad)
  Profile = -> Sketch017
  ReferenceAxis = -> Sketch017 [N_Axis]
  Refine = true
  Suppressed = false
  Type = 0
FEATURE [PartDesign::Chamfer] Chamfer013
  Angle = 45
  Base = -> Pocket006 [Edge30,Edge29]
  BaseFeature = -> Pocket006
  ChamferType = 0
  FlipDirection = false
  Placement = pos=(7.9014e-08,-84,20.8536) rot=(1,0,0;3.14159rad)
  Refine = true
  Size = 3
  Size2 = 1
  SupportTransform = false
  Suppressed = false
  UseAllEdges = false
FEATURE [PartDesign::Body] Body003  label="PlateThreadBlock OLD"
  AllowCompound = false
  Group = -> [DatumPlane005,CopyPocket005,Sketch014,Pad007,Sketch015,Pad008,Sketch016,Hole001,Sketch017,Pocket006,Chamfer013]
  Origin = -> Origin003
  Tip = -> Chamfer013
FEATURE [PartDesign::FeatureBase] Clone
  BaseFeature = -> Body003
  Suppressed = false
FEATURE [Sketcher::SketchObject] Sketch018
  ArcFitTolerance = 1e-06
  AttachmentSupport = -> [Clone]
  ExternalGeometry = -> [Clone]
  FullyConstrained = true
  MakeInternals = false
  MapMode = 5
  Placement = pos=(0,-46.75,0) rot=(1,0,0;1.5708rad)
  sketch-geometry (1):
    g0: Circle CenterX=41.9965 CenterY=13.8536 CenterZ=0 NormalX=0 NormalY=0 NormalZ=1 AngleXU=0 Radius=2.5
  constraints (2):
    c: Diameter(g0) = 5
    c: Coincident(g0,g-3)
FEATURE [PartDesign::Hole] Hole002
  BaseFeature = -> Clone
  CustomThreadClearance = 0.2
  Depth = 25
  DepthType = 0
  Diameter = 5.2
  DrillForDepth = false
  DrillPoint = 1
  DrillPointAngle = 118
  HoleCutCountersinkAngle = 90
  HoleCutCustomValues = false
  HoleCutDepth = 0
  HoleCutDiameter = 6.1
  HoleCutType = 0
  ModelThread = true
  Profile = -> Sketch018
  Refine = true
  Suppressed = false
  Tapered = false
  TaperedAngle = 90
  ThreadClass = 0
  ThreadDepth = 25
  ThreadDepthType = 0
  ThreadDirection = 0
  ThreadFit = 0
  ThreadSize = 14
  ThreadType = 1
  Threaded = true
  UseCustomThreadClearance = true
FEATURE [PartDesign::ShapeBinder] ShapeBinder003
  Placement = pos=(0,-84,2e-14) rot=(1,0,0;1.5708rad)
  Support = -> [Fillet]
  TraceSupport = false
FEATURE [PartDesign::Plane] DatumPlane006
  AttachmentSupport = -> [ShapeBinder003]
  Length = 61.997
  MapMode = 11
  Placement = pos=(42,-84,14) rot=(0.57735,-0.57735,0.57735;2.0944rad)
  ResizeMode = 0
  Width = 83.9605
FEATURE [Sketcher::SketchObject] Sketch019
  ArcFitTolerance = 1e-06
  AttachmentSupport = -> [DatumPlane006]
  ExternalGeometry = -> [ShapeBinder003]
  FullyConstrained = true
  MakeInternals = false
  MapMode = 5
  Placement = pos=(42,-84,14) rot=(0.57735,-0.57735,0.57735;2.0944rad)
  sketch-geometry (1):
    g0: Circle CenterX=0 CenterY=0 CenterZ=0 NormalX=0 NormalY=0 NormalZ=1 AngleXU=0 Radius=2.9
  constraints (2):
    c: Diameter(g0) = 5.8
    c: Coincident(g0,g-1)
FEATURE [PartDesign::Pad] Pad009
  Direction = (0,-1,0)
  Length = 5
  Length2 = 10
  Placement = pos=(42,-84,14) rot=(0.57735,-0.57735,0.57735;2.0944rad)
  Profile = -> Sketch019
  ReferenceAxis = -> Sketch019 [N_Axis]
  Refine = true
  Reversed = true
  Suppressed = false
  Type = 0
FEATURE [Sketcher::SketchObject] Sketch020
  ArcFitTolerance = 1e-06
  AttachmentSupport = -> [Pad009]
  ExternalGeometry = -> [Pad009]
  FullyConstrained = true
  MakeInternals = false
  MapMode = 5
  Placement = pos=(42,-84,14) rot=(0.57735,-0.57735,0.57735;2.0944rad)
  sketch-geometry (1):
    g0: Circle CenterX=0 CenterY=0 CenterZ=0 NormalX=0 NormalY=0 NormalZ=1 AngleXU=0 Radius=3
  constraints (2):
    c: Diameter(g0) = 6
    c: Coincident(g0,g-1)
FEATURE [PartDesign::Pad] Pad010
  BaseFeature = -> Pad009
  Direction = (0,-1,0)
  Length = 15
  Length2 = 10
  Placement = pos=(42,-84,14) rot=(0.57735,-0.57735,0.57735;2.0944rad)
  Profile = -> Sketch020
  ReferenceAxis = -> Sketch020 [N_Axis]
  Refine = true
  Suppressed = false
  Type = 0
FEATURE [Sketcher::SketchObject] Sketch021
  ArcFitTolerance = 1e-06
  AttachmentSupport = -> [Pad010]
  ExternalGeometry = -> [Pad010]
  FullyConstrained = true
  MakeInternals = false
  MapMode = 5
  Placement = pos=(42,-99,14) rot=(0.57735,-0.57735,0.57735;2.0944rad)
  sketch-geometry (1):
    g0: Circle CenterX=0 CenterY=0 CenterZ=0 NormalX=0 NormalY=0 NormalZ=1 AngleXU=0 Radius=7.5
  constraints (2):
    c: Diameter(g0) = 15
    c: Coincident(g0,g-1)
FEATURE [PartDesign::Pad] Pad011
  BaseFeature = -> Pad010
  Direction = (0,-1,0)
  Length = 20
  Length2 = 10
  Placement = pos=(42,-84,14) rot=(0.57735,-0.57735,0.57735;2.0944rad)
  Profile = -> Sketch021
  ReferenceAxis = -> Sketch021 [N_Axis]
  Refine = true
  Suppressed = false
  Type = 0
FEATURE [Sketcher::SketchObject] Sketch022
  ArcFitTolerance = 1e-06
  AttachmentSupport = -> [Pad011]
  ExternalGeometry = -> [Pad011]
  FullyConstrained = true
  MakeInternals = false
  MapMode = 5
  Placement = pos=(42,-119,14) rot=(0.57735,-0.57735,0.57735;2.0944rad)
  sketch-geometry (17):
    g0: LineSegment [constr] StartX=-5.29923e-11 StartY=5.2929e-11 StartZ=0 EndX=-5.29923e-11 EndY=7.5 EndZ=0
    g1: LineSegment [constr] StartX=-5.29923e-11 StartY=5.2929e-11 StartZ=0 EndX=7.5 EndY=5.2929e-11 EndZ=0
    g2: LineSegment [constr] StartX=-5.29923e-11 StartY=5.2929e-11 StartZ=0 EndX=-5.29923e-11 EndY=-7.5 EndZ=0
    g3: LineSegment [constr] StartX=-5.29923e-11 StartY=5.2929e-11 StartZ=0 EndX=-7.5 EndY=5.2929e-11 EndZ=0
    g4: LineSegment [constr] StartX=-5.29923e-11 StartY=5.2929e-11 StartZ=0 EndX=-5.3033 EndY=5.3033 EndZ=0
    g5: LineSegment [constr] StartX=-5.29923e-11 StartY=5.2929e-11 StartZ=0 EndX=5.3033 EndY=5.3033 EndZ=0
    g6: LineSegment [constr] StartX=-5.29923e-11 StartY=5.2929e-11 StartZ=0 EndX=5.3033 EndY=-5.3033 EndZ=0
    g7: LineSegment [constr] StartX=-5.29923e-11 StartY=5.2929e-11 StartZ=0 EndX=-5.3033 EndY=-5.3033 EndZ=0
    g8: Circle CenterX=-5.3033 CenterY=5.3033 CenterZ=0 NormalX=0 NormalY=0 NormalZ=1 AngleXU=0 Radius=1.34e-13
    g9: Circle CenterX=-5.3033 CenterY=5.3033 CenterZ=0 NormalX=0 NormalY=0 NormalZ=1 AngleXU=0 Radius=1.75
    g10: Circle CenterX=-7.5 CenterY=5.2929e-11 CenterZ=0 NormalX=0 NormalY=0 NormalZ=1 AngleXU=0 Radius=1.75
    g11: Circle CenterX=-5.3033 CenterY=-5.3033 CenterZ=0 NormalX=0 NormalY=0 NormalZ=1 AngleXU=0 Radius=1.75
    g12: Circle CenterX=-5.29923e-11 CenterY=-7.5 CenterZ=0 NormalX=0 NormalY=0 NormalZ=1 AngleXU=0 Radius=1.75
    g13: Circle CenterX=5.3033 CenterY=-5.3033 CenterZ=0 NormalX=0 NormalY=0 NormalZ=1 AngleXU=0 Radius=1.75
    g14: Circle CenterX=7.5 CenterY=5.2929e-11 CenterZ=0 NormalX=0 NormalY=0 NormalZ=1 AngleXU=0 Radius=1.75
    g15: Circle CenterX=5.3033 CenterY=5.3033 CenterZ=0 NormalX=0 NormalY=0 NormalZ=1 AngleXU=0 Radius=1.75
    g16: Circle CenterX=-5.29923e-11 CenterY=7.5 CenterZ=0 NormalX=0 NormalY=0 NormalZ=1 AngleXU=0 Radius=1.75
  constraints (42):
    c: Coincident(g0,g-1)
    c: PointOnObject(g0,g-3)
    c: Vertical(g0)
    c: Coincident(g1,g0)
    c: PointOnObject(g1,g-3)
    c: Horizontal(g1)
    c: Coincident(g2,g0)
    c: PointOnObject(g2,g-3)
    c: Vertical(g2)
    c: Coincident(g3,g0)
    c: PointOnObject(g3,g-3)
    c: Horizontal(g3)
    c: Angle(g-1,g4) = 2.35619
    c: Coincident(g4,g0)
    c: PointOnObject(g4,g-3)
    c: Angle(g-1,g5) = 0.785398
    c: Coincident(g5,g0)
    c: PointOnObject(g5,g-3)
    c: Angle(g-1,g6) = -0.785398
    c: Coincident(g6,g0)
    c: PointOnObject(g6,g-3)
    c: Angle(g-1,g7) = -2.35619
    c: Coincident(g7,g0)
    c: PointOnObject(g7,g-3)
    c: Coincident(g8,g4)
    c: Tangent(g8,g-3)
    c: Diameter(g9) = 3.5
    c: Coincident(g9,g4)
    c: Diameter(g10) = 3.5
    c: Coincident(g10,g3)
    c: Diameter(g11) = 3.5
    c: Coincident(g11,g7)
    c: Diameter(g12) = 3.5
    c: Coincident(g12,g2)
    c: Diameter(g13) = 3.5
    c: Coincident(g13,g6)
    c: Diameter(g14) = 3.5
    c: Coincident(g14,g1)
    c: Diameter(g15) = 3.5
    c: Coincident(g15,g5)
    c: Diameter(g16) = 3.5
    c: Coincident(g16,g0)
FEATURE [PartDesign::Pocket] Pocket007
  BaseFeature = -> Pad011
  Direction = (0,1,0)
  Length = 50
  Length2 = 5
  Placement = pos=(42,-84,14) rot=(0.57735,-0.57735,0.57735;2.0944rad)
  Profile = -> Sketch022
  ReferenceAxis = -> Sketch022 [N_Axis]
  Refine = true
  Suppressed = false
  Type = 1
FEATURE [PartDesign::Fillet] Fillet004
  Base = -> Pocket007 [Edge23]
  BaseFeature = -> Pocket007
  Placement = pos=(42,-84,14) rot=(0.57735,-0.57735,0.57735;2.0944rad)
  Radius = 4
  Refine = true
  SupportTransform = false
  Suppressed = false
  UseAllEdges = false
FEATURE [PartDesign::Point] DatumPoint
  AttacherType = Attacher::AttachEnginePoint
  AttachmentSupport = -> [Fillet004]
  MapMode = 36
  Placement = pos=(42,-79,14) rot=(0.707107,0,0.707107;3.14159rad)
FEATURE [Part::Part2DObjectPython] VThreadProfile  # Draft 2D object (typed FeaturePython)
  Area = 21.5626
  Closed = true
  Continuity = C2
  Deviation = 0.1
  Height = 74
  Helix = Helix
  Instructions = Expand this with the ... button to view instructions | Sweep this object along a helix of the same pitch to produce your thread. | It is recommended to make the helix in the ThreadProfile workbench. | If there is an active Body the ThreadProfile object will be put into it.,If not it can be dragged and dropped into the body later. | If there is an active Body when the helix is made there will be made a ShapeBinder for it | For internal threads you will need to cut the Sweep object out of a cylinder, or if using Part Design sweep it as a Subtractive Pipe. | Always use Frenet mode | I have provided some presets, but it is possible there could be some errors.  Double check for mission critical applications. | Also, the tolerances might be different from what you wish to have.  I believe the internal minor diameters are all minimum and the external are all maximum.
  InternalOrExternal = 1
  MakeFace = true
  MinorDiameter = 4.773
  Parameterization = 1
  Pitch = 1
  Placement = pos=(42,-79,14) rot=(1,0,0;-1.5708rad)
  Points = (66) [(2.37314,0.228827,0),(2.31975,0.451556,0),(2.25136,0.667864,0),(2.16643,0.876642,0),(2.06474,1.07659,0),(1.94661,1.26636,0),(1.81267,1.44463,0),+59 more]
  Presets = 16
  Quality = 11
  ThreadCount = 74
  Variants = 0
  Version = 1.92
  external2S_data = [-0.00461051,-0.00886426,-0.0128148,-0.0165028,-0.0199596,-0.0232105,-0.0262759,-0.0291725,-0.0319145,-0.0345137,-0.0369805,-0.0393235,-0.0415505,-0.0436681,-0.0456823,-0.0475981,-0.0494204,-0.0511532,-0.0528003,-0.0543649,-0.0558502,+698 more]
  external3S_data = [-0.00677828,-0.0128149,-0.0182584,-0.0232106,-0.0277444,-0.0319145,-0.0357632,-0.0393236,-0.0426227,-0.0456823,-0.0485208,-0.0511533,-0.0535928,-0.0558503,-0.0579353,-0.059856,-0.0616195,-0.0632319,-0.0646984,-0.0660239,-0.0672123,+698 more]
  external45_data = [-0.00137363,-0.00271738,-0.00403219,-0.00531893,-0.00657844,-0.00781148,-0.00901878,-0.010201,-0.0113589,-0.012493,-0.0136039,-0.0146921,-0.0157583,-0.0168028,-0.0178261,-0.0188288,-0.0198112,-0.0207738,-0.0217169,-0.0226409,-0.0235462,+698 more]
  external_data = [-0.00235387,-0.00461052,-0.00677828,-0.00886428,-0.0108747,-0.0128149,-0.0146895,-0.0165028,-0.0182584,-0.0199597,-0.0216095,-0.0232106,-0.0247653,-0.0262759,-0.0277444,-0.0291725,-0.0305621,-0.0319145,-0.0332313,-0.0345138,-0.0357632,+698 more]
  internal2S_data = [0,0,0,0,0,0,0,0,0,0,0,0,0,0,0,0,0,0,0,0,0,0,0,0,0,0,0,0,0,0,0,0,0,0,0,0,0,0,0,0,0,0,0,0,0,0,0,0,0,0,0,0,0,0,0,0,0,0,0,0,0,0,0,0,0,0,0,0,0,0,0,0,0,0,0,0,0,0,0,0,0,0,0,0,0,0,0,0,0,0,0.00481128,0.00962256,0.0144338,0.0192451,0.0240564,+624 more]
  internal3S_data = [0,0,0,0,0,0,0,0,0,0,0,0,0,0,0,0,0,0,0,0,0,0,0,0,0,0,0,0,0,0,0,0,0,0,0,0,0,0,0,0,0,0,0,0,0,0,0,0,0,0,0,0,0,0,0,0,0,0,0,0,0.00721688,0.0144338,0.0216506,0.0288675,0.0360844,0.0433013,0.0505181,0.057735,0.0649519,0.0721688,0.0793857,0.0866025,+647 more]
  internal45_data = [0,0,0,0,0,0,0,0,0,0,0,0,0,0,0,0,0,0,0,0,0,0,0,0,0,0,0,0,0,0,0,0,0,0,0,0,0,0,0,0,0,0,0,0,0,0,0,0,0,0,0,0,0,0,0,0,0,0,0,0,0,0,0,0,0,0,0,0,0,0,0,0,0,0,0,0,0,0,0,0,0,0,0,0,0,0,0,0,0,0,0,0,0,0,0,0,0,0,0,0,0,0,0,0,0,0,0,0,0,0,0,0,0,0,0,0,0,0,0,0,+599 more]
  internal_data = [0,0,0,0,0,0,0,0,0,0,0,0,0,0,0,0,0,0,0,0,0,0,0,0,0,0,0,0,0,0,0,0,0,0,0,0,0,0,0,0,0,0,0,0,0,0,0,0,0,0,0,0,0,0,0,0,0,0,0,0,0,0,0,0,0,0,0,0,0,0,0,0,0,0,0,0,0,0,0,0,0,0,0,0,0,0,0,0,0,0,0,0,0,0,0,0,0,0,0,0,0,0,0,0,0,0,0,0,0,0,0,0,0,0,0,0,0,0,0,0,+599 more]
  preset_names = <blob: 3959 chars omitted>
  presets_data = [0,0,0,2.20878,24.1173,24.6888,0.25,0.693,0.729,0.25,0.793,0.829,0.25,0.893,0.929,0.3,1.032,1.075,0.35,1.171,1.221,0.35,1.371,1.421,0.4,1.509,1.567,0.45,1.648,1.713,0.45,1.948,2.013,0.5,2.387,2.459,0.6,2.764,2.85,0.7,3.141,3.242,0.75,3.58,+712 more]
FEATURE [Part::Helix] Helix
  Angle = 0
  AttacherType = Attacher::AttachEngine3D
  Height = 74
  Length = 470.808
  LocalCoord = 0
  Pitch = 1
  Placement = pos=(42,-79,14) rot=(1,0,0;-1.5708rad)
  Radius = 1
  SegmentLength = 1
  Style = 0
  expr: AttachmentOffset = VThreadProfile.AttachmentOffset
  expr: AttachmentSupport = VThreadProfile.AttachmentSupport
  expr: Height = VThreadProfile.ThreadCount * VThreadProfile.Pitch
  expr: MapMode = VThreadProfile.MapMode
  expr: MapPathParameter = VThreadProfile.MapPathParameter
  expr: MapReversed = VThreadProfile.MapReversed
  expr: Pitch = VThreadProfile.Pitch
  expr: SegmentLength = 1
FEATURE [PartDesign::AdditivePipe] AdditivePipe
  AuxilleryCurvelinear = true
  AuxillerySpineTangent = false
  BaseFeature = -> Fillet004
  Binormal = (0,0,0)
  Mode = 2
  Placement = pos=(42,-84,14) rot=(0.57735,-0.57735,0.57735;2.0944rad)
  Profile = -> VThreadProfile
  Refine = true
  Spine = -> Helix [Edge1,Edge2,Edge3,Edge4,Edge5,Edge6,Edge7,Edge8,Edge9,Edge10,Edge11,Edge12,Edge13,Edge14,Edge15,Edge16,Edge17,Edge18,Edge19,Edge20,Edge21,Edge22,Edge23,Edge24,Edge25,Edge26,Edge27,Edge28,Edge29,Edge30,Edge31,Edge32,Edge33,Edge34,Edge35,Edge36,Edge37,Edge38,Edge39,Edge40,+34 more]
  SpineTangent = false
  Suppressed = false
  Transformation = 0
  Transition = 0
FEATURE [PartDesign::ShapeBinder] ShapeBinder004
  Support = -> [Fillet]
  TraceSupport = false
FEATURE [PartDesign::Plane] DatumPlane007
  AttachmentSupport = -> [AdditivePipe]
  Length = 61.9972
  MapMode = 5
  Placement = pos=(42.0014,-4.99998,14) rot=(0.577354,0.577344,0.577354;4.18878rad)
  ResizeMode = 0
  Width = 83.9633
FEATURE [Sketcher::SketchObject] Sketch023
  ArcFitTolerance = 1e-06
  AttachmentSupport = -> [DatumPlane007]
  FullyConstrained = true
  MakeInternals = false
  MapMode = 5
  Placement = pos=(42.0014,-4.99998,14) rot=(0.577354,0.577344,0.577354;4.18878rad)
  sketch-geometry (1):
    g0: Circle CenterX=0 CenterY=0 CenterZ=0 NormalX=0 NormalY=0 NormalZ=1 AngleXU=0 Radius=2.9
  constraints (2):
    c: Diameter(g0) = 5.8
    c: Coincident(g0,g-1)
FEATURE [PartDesign::Pad] Pad012
  BaseFeature = -> AdditivePipe
  Direction = (1.755e-05,1,1.0234e-10)
  Length = 10
  Length2 = 10
  Placement = pos=(42,-84,14) rot=(0.57735,-0.57735,0.57735;2.0944rad)
  Profile = -> Sketch023
  ReferenceAxis = -> Sketch023 [N_Axis]
  Refine = true
  Suppressed = false
  Type = 0
FEATURE [PartDesign::ShapeBinder] CopyPocket008
  Placement = pos=(42,-84,14) rot=(0.57735,-0.57735,0.57735;2.0944rad)
  TraceSupport = false
FEATURE [PartDesign::Plane] DatumPlane008
  AttachmentSupport = -> [CopyPocket008]
  Length = 61.9575
  MapMode = 5
  Placement = pos=(41.9985,5.00002,14) rot=(-0.577347,-0.577357,-0.577347;2.09438rad)
  ResizeMode = 0
  Width = 83.4479
FEATURE [Sketcher::SketchObject] Sketch025
  ArcFitTolerance = 1e-06
  AttachmentSupport = -> [DatumPlane008]
  ExternalGeometry = -> [CopyPocket008]
  FullyConstrained = true
  MakeInternals = false
  MapMode = 5
  Placement = pos=(41.9985,5.00002,14) rot=(-0.577347,-0.577357,-0.577347;2.09438rad)
  sketch-geometry (2):
    g0: Circle CenterX=0 CenterY=0 CenterZ=0 NormalX=0 NormalY=0 NormalZ=1 AngleXU=0 Radius=1.55
    g1: Circle CenterX=0 CenterY=0 CenterZ=0 NormalX=0 NormalY=0 NormalZ=1 AngleXU=0 Radius=4.5
  constraints (4):
    c: Diameter(g0) = 3.1
    c: Coincident(g0,g-1)
    c: Diameter(g1) = 9
    c: Coincident(g1,g0)
FEATURE [PartDesign::Pad] Pad013
  Direction = (-1.75232e-05,1,-4.99912e-10)
  Length = 3
  Length2 = 10
  Placement = pos=(41.9985,5.00002,14) rot=(-0.577347,-0.577357,-0.577347;2.09438rad)
  Profile = -> Sketch025
  ReferenceAxis = -> Sketch025 [N_Axis]
  Refine = true
  Suppressed = false
  Type = 0
FEATURE [PartDesign::Plane] DatumPlane009
  AttachmentSupport = -> [Pad013]
  Length = 61.9575
  MapMode = 5
  Placement = pos=(41.9984,8.00002,14) rot=(-0.577347,-0.577357,-0.577347;2.09438rad)
  ResizeMode = 0
  Width = 83.4479
FEATURE [Sketcher::SketchObject] Sketch026
  ArcFitTolerance = 1e-06
  AttachmentSupport = -> [DatumPlane009]
  ExternalGeometry = -> [Pad013]
  FullyConstrained = true
  MakeInternals = false
  MapMode = 5
  Placement = pos=(41.9984,8.00002,14) rot=(-0.577347,-0.577357,-0.577347;2.09438rad)
  sketch-geometry (2):
    g0: Circle CenterX=0 CenterY=0 CenterZ=0 NormalX=0 NormalY=0 NormalZ=1 AngleXU=0 Radius=4.50001
    g1: Circle CenterX=0 CenterY=0 CenterZ=0 NormalX=0 NormalY=0 NormalZ=1 AngleXU=0 Radius=3.1
  constraints (4):
    c: Coincident(g0,g-1)
    c: Tangent(g0,g-3)
    c: Diameter(g1) = 6.2
    c: Coincident(g1,g0)
FEATURE [PartDesign::Pad] Pad014
  BaseFeature = -> Pad013
  Direction = (-1.75232e-05,1,-4.99912e-10)
  Length = 6
  Length2 = 10
  Placement = pos=(41.9985,5.00002,14) rot=(-0.577347,-0.577357,-0.577347;2.09438rad)
  Profile = -> Sketch026
  ReferenceAxis = -> Sketch026 [N_Axis]
  Refine = true
  Suppressed = false
  Type = 0
FEATURE [PartDesign::Chamfer] Chamfer014
  Angle = 45
  Base = -> Pad014 [Edge11]
  BaseFeature = -> Pad014
  ChamferType = 0
  FlipDirection = false
  Placement = pos=(41.9985,5.00002,14) rot=(-0.577347,-0.577357,-0.577347;2.09438rad)
  Refine = true
  Size = 0.5
  Size2 = 1
  SupportTransform = false
  Suppressed = false
  UseAllEdges = false
FEATURE [PartDesign::Body] Body006  label="Adjuster Cap"
  AllowCompound = false
  Group = -> [DatumPlane008,CopyPocket008,Sketch025,Pad013,DatumPlane009,Sketch026,Pad014,Chamfer014]
  Origin = -> Origin006
  Tip = -> Chamfer014
FEATURE [Sketcher::SketchObject] Sketch027
  ArcFitTolerance = 1e-06
  AttachmentSupport = -> [Fillet]
  ExternalGeometry = -> [Fillet]
  FullyConstrained = true
  MakeInternals = false
  MapMode = 5
  Placement = pos=(0,-84,0) rot=(1,0,0;1.5708rad)
  sketch-geometry (2):
    g0: Circle CenterX=42 CenterY=14 CenterZ=0 NormalX=0 NormalY=0 NormalZ=1 AngleXU=0 Radius=3.125
    g1: Circle CenterX=42 CenterY=14 CenterZ=0 NormalX=0 NormalY=0 NormalZ=1 AngleXU=0 Radius=3.75
  constraints (4):
    c: Coincident(g0,g-3)
    c: Diameter(g1) = 7.5
    c: Coincident(g1,g0)
    c: Diameter(g0) = 6.25
FEATURE [PartDesign::Pad] Pad015
  BaseFeature = -> Fillet
  Direction = (0,-1,2e-16)
  Length = 8
  Length2 = 10
  Placement = pos=(0,0,0) rot=(1,0,0;1.5708rad)
  Profile = -> Sketch027
  ReferenceAxis = -> Sketch027 [N_Axis]
  Refine = true
  Suppressed = false
  Type = 0
FEATURE [PartDesign::Fillet] Fillet005
  Base = -> Pad015 [Edge70]
  BaseFeature = -> Pad015
  Placement = pos=(0,0,0) rot=(1,0,0;1.5708rad)
  Radius = 2
  Refine = true
  SupportTransform = false
  Suppressed = false
  UseAllEdges = false
FEATURE [Sketcher::SketchObject] Sketch030
  ArcFitTolerance = 1e-06
  AttachmentSupport = -> [Pocket005]
  ExternalGeometry = -> [Pocket005]
  FullyConstrained = true
  MakeInternals = false
  MapMode = 5
  Placement = pos=(7.11416e-08,-84,25.3536) rot=(0,0,1;3.14159rad)
  sketch-geometry (11):
    g0: LineSegment StartX=-84 StartY=0 StartZ=0 EndX=-84 EndY=-84 EndZ=0
    g1: LineSegment StartX=-84 StartY=-84 StartZ=0 EndX=7.11416e-08 EndY=-84 EndZ=0
    g2: LineSegment StartX=7.11416e-08 StartY=-84 StartZ=0 EndX=7.11416e-08 EndY=0 EndZ=0
    g3: LineSegment StartX=7.11416e-08 StartY=0 StartZ=0 EndX=-84 EndY=0 EndZ=0
    g4: Circle CenterX=-79 CenterY=-5 CenterZ=0 NormalX=0 NormalY=0 NormalZ=1 AngleXU=0 Radius=1.35
    g5: Circle CenterX=-79 CenterY=-42 CenterZ=0 NormalX=0 NormalY=0 NormalZ=1 AngleXU=0 Radius=1.35
    g6: Circle CenterX=-79 CenterY=-79 CenterZ=0 NormalX=0 NormalY=0 NormalZ=1 AngleXU=0 Radius=1.35
    g7: Circle CenterX=-41.9965 CenterY=-42 CenterZ=0 NormalX=0 NormalY=0 NormalZ=1 AngleXU=0 Radius=1.55
    g8: Circle CenterX=-5 CenterY=-5 CenterZ=0 NormalX=0 NormalY=0 NormalZ=1 AngleXU=0 Radius=1.35
    g9: Circle CenterX=-5 CenterY=-42 CenterZ=0 NormalX=0 NormalY=0 NormalZ=1 AngleXU=0 Radius=1.35
    g10: Circle CenterX=-5 CenterY=-79 CenterZ=0 NormalX=0 NormalY=0 NormalZ=1 AngleXU=0 Radius=1.35
  constraints (24):
    c: Coincident(g0,g1)
    c: Coincident(g1,g2)
    c: Coincident(g2,g3)
    c: Coincident(g3,g0)
    c: Vertical(g0)
    c: Vertical(g2)
    c: Horizontal(g1)
    c: Horizontal(g3)
    c: Coincident(g0,g-7)
    c: Coincident(g1,g-6)
    c: Coincident(g4,g-3)
    c: Equal(g4,g-3)
    c: Coincident(g5,g-10)
    c: Equal(g5,g-10)
    c: Coincident(g6,g-12)
    c: Equal(g6,g-12)
    c: Coincident(g7,g-9)
    c: Equal(g7,g-9)
    c: Coincident(g8,g-11)
    c: Equal(g8,g-11)
    c: Coincident(g9,g-8)
    c: Equal(g9,g-8)
    c: Coincident(g10,g-13)
    c: Equal(g10,g-13)
FEATURE [PartDesign::Pad] Pad016
  BaseFeature = -> Pocket005
  Direction = (2.80598e-09,0,1)
  Length = 2
  Length2 = 10
  Placement = pos=(0,-84,2e-15) rot=(1,0,0;1.5708rad)
  Profile = -> Sketch030
  ReferenceAxis = -> Sketch030 [N_Axis]
  Refine = true
  Suppressed = false
  Type = 0
FEATURE [Sketcher::SketchObject] Sketch031
  ArcFitTolerance = 1e-06
  AttachmentSupport = -> [Pad016]
  ExternalGeometry = -> [Pad016]
  FullyConstrained = true
  MakeInternals = false
  MapMode = 5
  Placement = pos=(7.67535e-08,-84,27.3536) rot=(0,0,1;3.14159rad)
  sketch-geometry (1):
    g0: Circle CenterX=-41.9965 CenterY=-42 CenterZ=0 NormalX=0 NormalY=0 NormalZ=1 AngleXU=0 Radius=3
  constraints (2):
    c: Diameter(g0) = 6
    c: Coincident(g0,g-3)
FEATURE [PartDesign::Pocket] Pocket011
  BaseFeature = -> Pad016
  Direction = (-2.80598e-09,0,-1)
  Length = 4
  Length2 = 5
  Placement = pos=(0,-84,2e-15) rot=(1,0,0;1.5708rad)
  Profile = -> Sketch031
  ReferenceAxis = -> Sketch031 [N_Axis]
  Refine = true
  Suppressed = false
  Type = 0
FEATURE [PartDesign::ShapeBinder] CopyPocket011
  Placement = pos=(0,-84,2e-15) rot=(1,0,0;1.5708rad)
  TraceSupport = false
FEATURE [PartDesign::Plane] DatumPlane010
  AttachmentSupport = -> [CopyPocket011]
  Length = 130.8
  MapMode = 5
  Placement = pos=(7.67535e-08,-84,27.3536) rot=(0,0,1;3.14159rad)
  ResizeMode = 0
  Width = 130.8
FEATURE [Sketcher::SketchObject] Sketch032
  ArcFitTolerance = 1e-06
  AttachmentSupport = -> [DatumPlane010]
  ExternalGeometry = -> [CopyPocket011]
  FullyConstrained = true
  MakeInternals = false
  MapMode = 5
  Placement = pos=(7.67535e-08,-84,27.3536) rot=(0,0,1;3.14159rad)
  sketch-geometry (10):
    g0: Circle CenterX=-79 CenterY=-42 CenterZ=0 NormalX=0 NormalY=0 NormalZ=1 AngleXU=0 Radius=3
    g1: Circle CenterX=-5 CenterY=-42 CenterZ=0 NormalX=0 NormalY=0 NormalZ=1 AngleXU=0 Radius=3
    g2: LineSegment StartX=-84 StartY=0 StartZ=0 EndX=-84 EndY=-84 EndZ=0
    g3: LineSegment StartX=-84 StartY=-84 StartZ=0 EndX=7.11416e-08 EndY=-84 EndZ=0
    g4: LineSegment StartX=7.11416e-08 StartY=-84 StartZ=0 EndX=7.11416e-08 EndY=0 EndZ=0
    g5: LineSegment StartX=7.11416e-08 StartY=0 StartZ=0 EndX=-84 EndY=0 EndZ=0
    g6: Circle CenterX=-79 CenterY=-5 CenterZ=0 NormalX=0 NormalY=0 NormalZ=1 AngleXU=0 Radius=1.6
    g7: Circle CenterX=-79 CenterY=-79 CenterZ=0 NormalX=0 NormalY=0 NormalZ=1 AngleXU=0 Radius=1.6
    g8: Circle CenterX=-5 CenterY=-5 CenterZ=0 NormalX=0 NormalY=0 NormalZ=1 AngleXU=0 Radius=1.6
    g9: Circle CenterX=-5 CenterY=-79 CenterZ=0 NormalX=0 NormalY=0 NormalZ=1 AngleXU=0 Radius=1.6
  constraints (22):
    c: Diameter(g0) = 6
    c: Coincident(g0,g-8)
    c: Diameter(g1) = 6
    c: Coincident(g1,g-10)
    c: Coincident(g2,g3)
    c: Coincident(g3,g4)
    c: Coincident(g4,g5)
    c: Coincident(g5,g2)
    c: Vertical(g2)
    c: Vertical(g4)
    c: Horizontal(g3)
    c: Horizontal(g5)
    c: Coincident(g2,g-4)
    c: Coincident(g3,g-6)
    c: Diameter(g6) = 3.2
    c: Coincident(g6,g-9)
    c: Coincident(g7,g-7)
    c: Diameter(g7) = 3.2
    c: Coincident(g8,g-12)
    c: Coincident(g9,g-11)
    c: Diameter(g9) = 3.2
    c: Diameter(g8) = 3.2
FEATURE [PartDesign::Pad] Pad017
  Direction = (2.80598e-09,0,1)
  Length = 4
  Length2 = 10
  Placement = pos=(7.67535e-08,-84,27.3536) rot=(0,0,1;3.14159rad)
  Profile = -> Sketch032
  ReferenceAxis = -> Sketch032 [N_Axis]
  Refine = true
  Suppressed = false
  Type = 0
FEATURE [Sketcher::SketchObject] Sketch033
  ArcFitTolerance = 1e-06
  AttachmentSupport = -> [Pad017]
  ExternalGeometry = -> [Pad017]
  FullyConstrained = true
  MakeInternals = false
  MapMode = 5
  Placement = pos=(8.79774e-08,-84,31.3536) rot=(0,0,1;3.14159rad)
  sketch-geometry (10):
    g0: Circle CenterX=-79 CenterY=-42 CenterZ=0 NormalX=0 NormalY=0 NormalZ=1 AngleXU=0 Radius=3
    g1: Circle CenterX=-5 CenterY=-42 CenterZ=0 NormalX=0 NormalY=0 NormalZ=1 AngleXU=0 Radius=3
    g2: Circle CenterX=-5 CenterY=-5 CenterZ=0 NormalX=0 NormalY=0 NormalZ=1 AngleXU=0 Radius=3
    g3: Circle CenterX=-5 CenterY=-79 CenterZ=0 NormalX=0 NormalY=0 NormalZ=1 AngleXU=0 Radius=3
    g4: Circle CenterX=-79 CenterY=-79 CenterZ=0 NormalX=0 NormalY=0 NormalZ=1 AngleXU=0 Radius=3
    g5: Circle CenterX=-79 CenterY=-5 CenterZ=0 NormalX=0 NormalY=0 NormalZ=1 AngleXU=0 Radius=3
    g6: LineSegment StartX=-84 StartY=0 StartZ=0 EndX=-84 EndY=-84 EndZ=0
    g7: LineSegment StartX=-84 StartY=-84 StartZ=0 EndX=7.11416e-08 EndY=-84 EndZ=0
    g8: LineSegment StartX=7.11416e-08 StartY=-84 StartZ=0 EndX=7.11416e-08 EndY=0 EndZ=0
    g9: LineSegment StartX=7.11416e-08 StartY=0 StartZ=0 EndX=-84 EndY=0 EndZ=0
  constraints (22):
    c: Coincident(g0,g-8)
    c: Equal(g0,g-8)
    c: Coincident(g1,g-11)
    c: Equal(g1,g-11)
    c: Diameter(g2) = 6
    c: Coincident(g2,g-10)
    c: Diameter(g3) = 6
    c: Coincident(g3,g-12)
    c: Diameter(g4) = 6
    c: Coincident(g4,g-7)
    c: Diameter(g5) = 6
    c: Coincident(g5,g-9)
    c: Coincident(g6,g7)
    c: Coincident(g7,g8)
    c: Coincident(g8,g9)
    c: Coincident(g9,g6)
    c: Vertical(g6)
    c: Vertical(g8)
    c: Horizontal(g7)
    c: Horizontal(g9)
    c: Coincident(g6,g-4)
    c: Coincident(g7,g-6)
FEATURE [PartDesign::Pad] Pad018
  BaseFeature = -> Pad017
  Direction = (2.80598e-09,0,1)
  Length = 3.5
  Length2 = 10
  Placement = pos=(7.67535e-08,-84,27.3536) rot=(0,0,1;3.14159rad)
  Profile = -> Sketch033
  ReferenceAxis = -> Sketch033 [N_Axis]
  Refine = true
  Suppressed = false
  Type = 0
FEATURE [Sketcher::SketchObject] Sketch034
  ArcFitTolerance = 1e-06
  AttachmentSupport = -> [Pad018]
  ExternalGeometry = -> [Pad018]
  FullyConstrained = false
  MakeInternals = false
  MapMode = 5
  Placement = pos=(9.77984e-08,-84,34.8536) rot=(0,0,1;3.14159rad)
  sketch-geometry (212):
    g0: LineSegment [constr] StartX=-42 StartY=-7.1e-15 StartZ=0 EndX=-42 EndY=-84 EndZ=0
    g1: GeomPoint X=-42 Y=-42 Z=0
    g2: Circle CenterX=-42 CenterY=-42 CenterZ=0 NormalX=0 NormalY=0 NormalZ=1 AngleXU=0 Radius=1.3
    g3: Circle CenterX=-37 CenterY=-42 CenterZ=0 NormalX=0 NormalY=0 NormalZ=1 AngleXU=0 Radius=1.3
    g4: Circle CenterX=-32 CenterY=-42 CenterZ=0 NormalX=0 NormalY=0 NormalZ=1 AngleXU=0 Radius=1.3
    g5: Circle CenterX=-27 CenterY=-42 CenterZ=0 NormalX=0 NormalY=0 NormalZ=1 AngleXU=0 Radius=1.3
    g6: Circle CenterX=-22 CenterY=-42 CenterZ=0 NormalX=0 NormalY=0 NormalZ=1 AngleXU=0 Radius=1.3
    g7: Circle CenterX=-17 CenterY=-42 CenterZ=0 NormalX=0 NormalY=0 NormalZ=1 AngleXU=0 Radius=1.3
    g8: Circle CenterX=-12 CenterY=-42 CenterZ=0 NormalX=0 NormalY=0 NormalZ=1 AngleXU=0 Radius=1.3
    g9: GeomPoint X=-42 Y=-37 Z=0
    g10: Circle CenterX=-42 CenterY=-37 CenterZ=0 NormalX=0 NormalY=0 NormalZ=1 AngleXU=0 Radius=1.3
    g11: Circle CenterX=-37 CenterY=-37 CenterZ=0 NormalX=0 NormalY=0 NormalZ=1 AngleXU=0 Radius=1.3
    g12: Circle CenterX=-32 CenterY=-37 CenterZ=0 NormalX=0 NormalY=0 NormalZ=1 AngleXU=0 Radius=1.3
    g13: Circle CenterX=-27 CenterY=-37 CenterZ=0 NormalX=0 NormalY=0 NormalZ=1 AngleXU=0 Radius=1.3
    g14: Circle CenterX=-22 CenterY=-37 CenterZ=0 NormalX=0 NormalY=0 NormalZ=1 AngleXU=0 Radius=1.3
    g15: Circle CenterX=-17 CenterY=-37 CenterZ=0 NormalX=0 NormalY=0 NormalZ=1 AngleXU=0 Radius=1.3
    g16: Circle CenterX=-12 CenterY=-37 CenterZ=0 NormalX=0 NormalY=0 NormalZ=1 AngleXU=0 Radius=1.3
    g17: GeomPoint X=-42 Y=-32 Z=0
    g18: Circle CenterX=-42 CenterY=-32 CenterZ=0 NormalX=0 NormalY=0 NormalZ=1 AngleXU=0 Radius=1.3
    g19: Circle CenterX=-37 CenterY=-32 CenterZ=0 NormalX=0 NormalY=0 NormalZ=1 AngleXU=0 Radius=1.3
    g20: Circle CenterX=-32 CenterY=-32 CenterZ=0 NormalX=0 NormalY=0 NormalZ=1 AngleXU=0 Radius=1.3
    g21: Circle CenterX=-27 CenterY=-32 CenterZ=0 NormalX=0 NormalY=0 NormalZ=1 AngleXU=0 Radius=1.3
    g22: Circle CenterX=-22 CenterY=-32 CenterZ=0 NormalX=0 NormalY=0 NormalZ=1 AngleXU=0 Radius=1.3
    g23: Circle CenterX=-17 CenterY=-32 CenterZ=0 NormalX=0 NormalY=0 NormalZ=1 AngleXU=0 Radius=1.3
    g24: Circle CenterX=-12 CenterY=-32 CenterZ=0 NormalX=0 NormalY=0 NormalZ=1 AngleXU=0 Radius=1.3
    g25: GeomPoint X=-42 Y=-27 Z=0
    g26: Circle CenterX=-42 CenterY=-27 CenterZ=0 NormalX=0 NormalY=0 NormalZ=1 AngleXU=0 Radius=1.3
    g27: Circle CenterX=-37 CenterY=-27 CenterZ=0 NormalX=0 NormalY=0 NormalZ=1 AngleXU=0 Radius=1.3
    g28: Circle CenterX=-32 CenterY=-27 CenterZ=0 NormalX=0 NormalY=0 NormalZ=1 AngleXU=0 Radius=1.3
    g29: Circle CenterX=-27 CenterY=-27 CenterZ=0 NormalX=0 NormalY=0 NormalZ=1 AngleXU=0 Radius=1.3
    g30: Circle CenterX=-22 CenterY=-27 CenterZ=0 NormalX=0 NormalY=0 NormalZ=1 AngleXU=0 Radius=1.3
    g31: Circle CenterX=-17 CenterY=-27 CenterZ=0 NormalX=0 NormalY=0 NormalZ=1 AngleXU=0 Radius=1.3
    g32: Circle CenterX=-12 CenterY=-27 CenterZ=0 NormalX=0 NormalY=0 NormalZ=1 AngleXU=0 Radius=1.3
    g33: GeomPoint X=-42 Y=-22 Z=0
    g34: Circle CenterX=-42 CenterY=-22 CenterZ=0 NormalX=0 NormalY=0 NormalZ=1 AngleXU=0 Radius=1.3
    g35: Circle CenterX=-37 CenterY=-22 CenterZ=0 NormalX=0 NormalY=0 NormalZ=1 AngleXU=0 Radius=1.3
    g36: Circle CenterX=-32 CenterY=-22 CenterZ=0 NormalX=0 NormalY=0 NormalZ=1 AngleXU=0 Radius=1.3
    g37: Circle CenterX=-27 CenterY=-22 CenterZ=0 NormalX=0 NormalY=0 NormalZ=1 AngleXU=0 Radius=1.3
    g38: Circle CenterX=-22 CenterY=-22 CenterZ=0 NormalX=0 NormalY=0 NormalZ=1 AngleXU=0 Radius=1.3
    g39: Circle CenterX=-17 CenterY=-22 CenterZ=0 NormalX=0 NormalY=0 NormalZ=1 AngleXU=0 Radius=1.3
    g40: Circle CenterX=-12 CenterY=-22 CenterZ=0 NormalX=0 NormalY=0 NormalZ=1 AngleXU=0 Radius=1.3
    g41: GeomPoint X=-42 Y=-17 Z=0
    g42: Circle CenterX=-42 CenterY=-17 CenterZ=0 NormalX=0 NormalY=0 NormalZ=1 AngleXU=0 Radius=1.3
    g43: Circle CenterX=-37 CenterY=-17 CenterZ=0 NormalX=0 NormalY=0 NormalZ=1 AngleXU=0 Radius=1.3
    g44: Circle CenterX=-32 CenterY=-17 CenterZ=0 NormalX=0 NormalY=0 NormalZ=1 AngleXU=0 Radius=1.3
    g45: Circle CenterX=-27 CenterY=-17 CenterZ=0 NormalX=0 NormalY=0 NormalZ=1 AngleXU=0 Radius=1.3
    g46: Circle CenterX=-22 CenterY=-17 CenterZ=0 NormalX=0 NormalY=0 NormalZ=1 AngleXU=0 Radius=1.3
    g47: Circle CenterX=-17 CenterY=-17 CenterZ=0 NormalX=0 NormalY=0 NormalZ=1 AngleXU=0 Radius=1.3
    g48: Circle CenterX=-12 CenterY=-17 CenterZ=0 NormalX=0 NormalY=0 NormalZ=1 AngleXU=0 Radius=1.3
    g49: GeomPoint X=-42 Y=-12 Z=0
    g50: Circle CenterX=-42 CenterY=-12 CenterZ=0 NormalX=0 NormalY=0 NormalZ=1 AngleXU=0 Radius=1.3
    g51: Circle CenterX=-37 CenterY=-12 CenterZ=0 NormalX=0 NormalY=0 NormalZ=1 AngleXU=0 Radius=1.3
    g52: Circle CenterX=-32 CenterY=-12 CenterZ=0 NormalX=0 NormalY=0 NormalZ=1 AngleXU=0 Radius=1.3
    g53: Circle CenterX=-27 CenterY=-12 CenterZ=0 NormalX=0 NormalY=0 NormalZ=1 AngleXU=0 Radius=1.3
    g54: Circle CenterX=-22 CenterY=-12 CenterZ=0 NormalX=0 NormalY=0 NormalZ=1 AngleXU=0 Radius=1.3
    g55: Circle CenterX=-17 CenterY=-12 CenterZ=0 NormalX=0 NormalY=0 NormalZ=1 AngleXU=0 Radius=1.3
    g56: Circle CenterX=-12 CenterY=-12 CenterZ=0 NormalX=0 NormalY=0 NormalZ=1 AngleXU=0 Radius=1.3
    g57: GeomPoint X=-42 Y=-7 Z=0
    g58: Circle CenterX=-42 CenterY=-7 CenterZ=0 NormalX=0 NormalY=0 NormalZ=1 AngleXU=0 Radius=1.3
    g59: Circle CenterX=-37 CenterY=-7 CenterZ=0 NormalX=0 NormalY=0 NormalZ=1 AngleXU=0 Radius=1.3
    g60: Circle CenterX=-32 CenterY=-7 CenterZ=0 NormalX=0 NormalY=0 NormalZ=1 AngleXU=0 Radius=1.3
    g61: Circle CenterX=-27 CenterY=-7 CenterZ=0 NormalX=0 NormalY=0 NormalZ=1 AngleXU=0 Radius=1.3
    g62: Circle CenterX=-22 CenterY=-7 CenterZ=0 NormalX=0 NormalY=0 NormalZ=1 AngleXU=0 Radius=1.3
    g63: Circle CenterX=-17 CenterY=-7 CenterZ=0 NormalX=0 NormalY=0 NormalZ=1 AngleXU=0 Radius=1.3
    g64: Circle CenterX=-12 CenterY=-7 CenterZ=0 NormalX=0 NormalY=0 NormalZ=1 AngleXU=0 Radius=1.3
    g65: LineSegment [constr] StartX=-84 StartY=-42 StartZ=0 EndX=7.11416e-08 EndY=-42 EndZ=0
    g66: Circle CenterX=-47 CenterY=-42 CenterZ=0 NormalX=0 NormalY=0 NormalZ=1 AngleXU=0 Radius=1.3
    g67: Circle CenterX=-52 CenterY=-42 CenterZ=0 NormalX=0 NormalY=0 NormalZ=1 AngleXU=0 Radius=1.3
    g68: Circle CenterX=-57 CenterY=-42 CenterZ=0 NormalX=0 NormalY=0 NormalZ=1 AngleXU=0 Radius=1.3
    g69: Circle CenterX=-62 CenterY=-42 CenterZ=0 NormalX=0 NormalY=0 NormalZ=1 AngleXU=0 Radius=1.3
    g70: Circle CenterX=-67 CenterY=-42 CenterZ=0 NormalX=0 NormalY=0 NormalZ=1 AngleXU=0 Radius=1.3
    g71: Circle CenterX=-72 CenterY=-42 CenterZ=0 NormalX=0 NormalY=0 NormalZ=1 AngleXU=0 Radius=1.3
    g72: Circle CenterX=-47 CenterY=-37 CenterZ=0 NormalX=0 NormalY=0 NormalZ=1 AngleXU=0 Radius=1.3
    g73: Circle CenterX=-52 CenterY=-37 CenterZ=0 NormalX=0 NormalY=0 NormalZ=1 AngleXU=0 Radius=1.3
    g74: Circle CenterX=-57 CenterY=-37 CenterZ=0 NormalX=0 NormalY=0 NormalZ=1 AngleXU=0 Radius=1.3
    g75: Circle CenterX=-62 CenterY=-37 CenterZ=0 NormalX=0 NormalY=0 NormalZ=1 AngleXU=0 Radius=1.3
    g76: Circle CenterX=-67 CenterY=-37 CenterZ=0 NormalX=0 NormalY=0 NormalZ=1 AngleXU=0 Radius=1.3
    g77: Circle CenterX=-72 CenterY=-37 CenterZ=0 NormalX=0 NormalY=0 NormalZ=1 AngleXU=0 Radius=1.3
    g78: Circle CenterX=-47 CenterY=-32 CenterZ=0 NormalX=0 NormalY=0 NormalZ=1 AngleXU=0 Radius=1.3
    g79: Circle CenterX=-52 CenterY=-32 CenterZ=0 NormalX=0 NormalY=0 NormalZ=1 AngleXU=0 Radius=1.3
    g80: Circle CenterX=-57 CenterY=-32 CenterZ=0 NormalX=0 NormalY=0 NormalZ=1 AngleXU=0 Radius=1.3
    g81: Circle CenterX=-62 CenterY=-32 CenterZ=0 NormalX=0 NormalY=0 NormalZ=1 AngleXU=0 Radius=1.3
    g82: Circle CenterX=-67 CenterY=-32 CenterZ=0 NormalX=0 NormalY=0 NormalZ=1 AngleXU=0 Radius=1.3
    g83: Circle CenterX=-72 CenterY=-32 CenterZ=0 NormalX=0 NormalY=0 NormalZ=1 AngleXU=0 Radius=1.3
    g84: Circle CenterX=-47 CenterY=-27 CenterZ=0 NormalX=0 NormalY=0 NormalZ=1 AngleXU=0 Radius=1.3
    g85: Circle CenterX=-52 CenterY=-27 CenterZ=0 NormalX=0 NormalY=0 NormalZ=1 AngleXU=0 Radius=1.3
    g86: Circle CenterX=-57 CenterY=-27 CenterZ=0 NormalX=0 NormalY=0 NormalZ=1 AngleXU=0 Radius=1.3
    g87: Circle CenterX=-62 CenterY=-27 CenterZ=0 NormalX=0 NormalY=0 NormalZ=1 AngleXU=0 Radius=1.3
    g88: Circle CenterX=-67 CenterY=-27 CenterZ=0 NormalX=0 NormalY=0 NormalZ=1 AngleXU=0 Radius=1.3
    g89: Circle CenterX=-72 CenterY=-27 CenterZ=0 NormalX=0 NormalY=0 NormalZ=1 AngleXU=0 Radius=1.3
    g90: Circle CenterX=-47 CenterY=-22 CenterZ=0 NormalX=0 NormalY=0 NormalZ=1 AngleXU=0 Radius=1.3
    g91: Circle CenterX=-52 CenterY=-22 CenterZ=0 NormalX=0 NormalY=0 NormalZ=1 AngleXU=0 Radius=1.3
    g92: Circle CenterX=-57 CenterY=-22 CenterZ=0 NormalX=0 NormalY=0 NormalZ=1 AngleXU=0 Radius=1.3
    g93: Circle CenterX=-62 CenterY=-22 CenterZ=0 NormalX=0 NormalY=0 NormalZ=1 AngleXU=0 Radius=1.3
    g94: Circle CenterX=-67 CenterY=-22 CenterZ=0 NormalX=0 NormalY=0 NormalZ=1 AngleXU=0 Radius=1.3
    g95: Circle CenterX=-72 CenterY=-22 CenterZ=0 NormalX=0 NormalY=0 NormalZ=1 AngleXU=0 Radius=1.3
    g96: Circle CenterX=-47 CenterY=-17 CenterZ=0 NormalX=0 NormalY=0 NormalZ=1 AngleXU=0 Radius=1.3
    g97: Circle CenterX=-52 CenterY=-17 CenterZ=0 NormalX=0 NormalY=0 NormalZ=1 AngleXU=0 Radius=1.3
    g98: Circle CenterX=-57 CenterY=-17 CenterZ=0 NormalX=0 NormalY=0 NormalZ=1 AngleXU=0 Radius=1.3
    g99: Circle CenterX=-62 CenterY=-17 CenterZ=0 NormalX=0 NormalY=0 NormalZ=1 AngleXU=0 Radius=1.3
    g100: Circle CenterX=-67 CenterY=-17 CenterZ=0 NormalX=0 NormalY=0 NormalZ=1 AngleXU=0 Radius=1.3
    g101: Circle CenterX=-72 CenterY=-17 CenterZ=0 NormalX=0 NormalY=0 NormalZ=1 AngleXU=0 Radius=1.3
    g102: Circle CenterX=-47 CenterY=-12 CenterZ=0 NormalX=0 NormalY=0 NormalZ=1 AngleXU=0 Radius=1.3
    g103: Circle CenterX=-52 CenterY=-12 CenterZ=0 NormalX=0 NormalY=0 NormalZ=1 AngleXU=0 Radius=1.3
    g104: Circle CenterX=-57 CenterY=-12 CenterZ=0 NormalX=0 NormalY=0 NormalZ=1 AngleXU=0 Radius=1.3
    g105: Circle CenterX=-62 CenterY=-12 CenterZ=0 NormalX=0 NormalY=0 NormalZ=1 AngleXU=0 Radius=1.3
    g106: Circle CenterX=-67 CenterY=-12 CenterZ=0 NormalX=0 NormalY=0 NormalZ=1 AngleXU=0 Radius=1.3
    g107: Circle CenterX=-72 CenterY=-12 CenterZ=0 NormalX=0 NormalY=0 NormalZ=1 AngleXU=0 Radius=1.3
    g108: Circle CenterX=-47 CenterY=-7 CenterZ=0 NormalX=0 NormalY=0 NormalZ=1 AngleXU=0 Radius=1.3
    g109: Circle CenterX=-52 CenterY=-7 CenterZ=0 NormalX=0 NormalY=0 NormalZ=1 AngleXU=0 Radius=1.3
    g110: Circle CenterX=-57 CenterY=-7 CenterZ=0 NormalX=0 NormalY=0 NormalZ=1 AngleXU=0 Radius=1.3
    g111: Circle CenterX=-62 CenterY=-7 CenterZ=0 NormalX=0 NormalY=0 NormalZ=1 AngleXU=0 Radius=1.3
    g112: Circle CenterX=-67 CenterY=-7 CenterZ=0 NormalX=0 NormalY=0 NormalZ=1 AngleXU=0 Radius=1.3
    g113: Circle CenterX=-72 CenterY=-7 CenterZ=0 NormalX=0 NormalY=0 NormalZ=1 AngleXU=0 Radius=1.3
    g114: GeomPoint X=-42 Y=-47 Z=0
    g115: Circle CenterX=-42 CenterY=-47 CenterZ=0 NormalX=0 NormalY=0 NormalZ=1 AngleXU=0 Radius=1.3
    g116: Circle CenterX=-37 CenterY=-47 CenterZ=0 NormalX=0 NormalY=0 NormalZ=1 AngleXU=0 Radius=1.3
    g117: Circle CenterX=-32 CenterY=-47 CenterZ=0 NormalX=0 NormalY=0 NormalZ=1 AngleXU=0 Radius=1.3
    g118: Circle CenterX=-27 CenterY=-47 CenterZ=0 NormalX=0 NormalY=0 NormalZ=1 AngleXU=0 Radius=1.3
    g119: Circle CenterX=-22 CenterY=-47 CenterZ=0 NormalX=0 NormalY=0 NormalZ=1 AngleXU=0 Radius=1.3
    g120: Circle CenterX=-17 CenterY=-47 CenterZ=0 NormalX=0 NormalY=0 NormalZ=1 AngleXU=0 Radius=1.3
    g121: Circle CenterX=-12 CenterY=-47 CenterZ=0 NormalX=0 NormalY=0 NormalZ=1 AngleXU=0 Radius=1.3
    g122: GeomPoint X=-42 Y=-52 Z=0
    g123: Circle CenterX=-42 CenterY=-52 CenterZ=0 NormalX=0 NormalY=0 NormalZ=1 AngleXU=0 Radius=1.3
    g124: Circle CenterX=-37 CenterY=-52 CenterZ=0 NormalX=0 NormalY=0 NormalZ=1 AngleXU=0 Radius=1.3
    g125: Circle CenterX=-32 CenterY=-52 CenterZ=0 NormalX=0 NormalY=0 NormalZ=1 AngleXU=0 Radius=1.3
    g126: Circle CenterX=-27 CenterY=-52 CenterZ=0 NormalX=0 NormalY=0 NormalZ=1 AngleXU=0 Radius=1.3
    g127: Circle CenterX=-22 CenterY=-52 CenterZ=0 NormalX=0 NormalY=0 NormalZ=1 AngleXU=0 Radius=1.3
    g128: Circle CenterX=-17 CenterY=-52 CenterZ=0 NormalX=0 NormalY=0 NormalZ=1 AngleXU=0 Radius=1.3
    g129: Circle CenterX=-12 CenterY=-52 CenterZ=0 NormalX=0 NormalY=0 NormalZ=1 AngleXU=0 Radius=1.3
    g130: GeomPoint X=-42 Y=-57 Z=0
    g131: Circle CenterX=-42 CenterY=-57 CenterZ=0 NormalX=0 NormalY=0 NormalZ=1 AngleXU=0 Radius=1.3
    g132: Circle CenterX=-37 CenterY=-57 CenterZ=0 NormalX=0 NormalY=0 NormalZ=1 AngleXU=0 Radius=1.3
    g133: Circle CenterX=-32 CenterY=-57 CenterZ=0 NormalX=0 NormalY=0 NormalZ=1 AngleXU=0 Radius=1.3
    g134: Circle CenterX=-27 CenterY=-57 CenterZ=0 NormalX=0 NormalY=0 NormalZ=1 AngleXU=0 Radius=1.3
    g135: Circle CenterX=-22 CenterY=-57 CenterZ=0 NormalX=0 NormalY=0 NormalZ=1 AngleXU=0 Radius=1.3
    g136: Circle CenterX=-17 CenterY=-57 CenterZ=0 NormalX=0 NormalY=0 NormalZ=1 AngleXU=0 Radius=1.3
    g137: Circle CenterX=-12 CenterY=-57 CenterZ=0 NormalX=0 NormalY=0 NormalZ=1 AngleXU=0 Radius=1.3
    g138: GeomPoint X=-42 Y=-62 Z=0
    g139: Circle CenterX=-42 CenterY=-62 CenterZ=0 NormalX=0 NormalY=0 NormalZ=1 AngleXU=0 Radius=1.3
    g140: Circle CenterX=-37 CenterY=-62 CenterZ=0 NormalX=0 NormalY=0 NormalZ=1 AngleXU=0 Radius=1.3
    g141: Circle CenterX=-32 CenterY=-62 CenterZ=0 NormalX=0 NormalY=0 NormalZ=1 AngleXU=0 Radius=1.3
    g142: Circle CenterX=-27 CenterY=-62 CenterZ=0 NormalX=0 NormalY=0 NormalZ=1 AngleXU=0 Radius=1.3
    g143: Circle CenterX=-22 CenterY=-62 CenterZ=0 NormalX=0 NormalY=0 NormalZ=1 AngleXU=0 Radius=1.3
    g144: Circle CenterX=-17 CenterY=-62 CenterZ=0 NormalX=0 NormalY=0 NormalZ=1 AngleXU=0 Radius=1.3
    g145: Circle CenterX=-12 CenterY=-62 CenterZ=0 NormalX=0 NormalY=0 NormalZ=1 AngleXU=0 Radius=1.3
    g146: GeomPoint X=-42 Y=-67 Z=0
    g147: Circle CenterX=-42 CenterY=-67 CenterZ=0 NormalX=0 NormalY=0 NormalZ=1 AngleXU=0 Radius=1.3
    g148: Circle CenterX=-37 CenterY=-67 CenterZ=0 NormalX=0 NormalY=0 NormalZ=1 AngleXU=0 Radius=1.3
    g149: Circle CenterX=-32 CenterY=-67 CenterZ=0 NormalX=0 NormalY=0 NormalZ=1 AngleXU=0 Radius=1.3
    g150: Circle CenterX=-27 CenterY=-67 CenterZ=0 NormalX=0 NormalY=0 NormalZ=1 AngleXU=0 Radius=1.3
    g151: Circle CenterX=-22 CenterY=-67 CenterZ=0 NormalX=0 NormalY=0 NormalZ=1 AngleXU=0 Radius=1.3
    g152: Circle CenterX=-17 CenterY=-67 CenterZ=0 NormalX=0 NormalY=0 NormalZ=1 AngleXU=0 Radius=1.3
    g153: Circle CenterX=-12 CenterY=-67 CenterZ=0 NormalX=0 NormalY=0 NormalZ=1 AngleXU=0 Radius=1.3
    g154: GeomPoint X=-42 Y=-72 Z=0
    g155: Circle CenterX=-42 CenterY=-72 CenterZ=0 NormalX=0 NormalY=0 NormalZ=1 AngleXU=0 Radius=1.3
    g156: Circle CenterX=-37 CenterY=-72 CenterZ=0 NormalX=0 NormalY=0 NormalZ=1 AngleXU=0 Radius=1.3
    g157: Circle CenterX=-32 CenterY=-72 CenterZ=0 NormalX=0 NormalY=0 NormalZ=1 AngleXU=0 Radius=1.3
    g158: Circle CenterX=-27 CenterY=-72 CenterZ=0 NormalX=0 NormalY=0 NormalZ=1 AngleXU=0 Radius=1.3
    g159: Circle CenterX=-22 CenterY=-72 CenterZ=0 NormalX=0 NormalY=0 NormalZ=1 AngleXU=0 Radius=1.3
    g160: Circle CenterX=-17 CenterY=-72 CenterZ=0 NormalX=0 NormalY=0 NormalZ=1 AngleXU=0 Radius=1.3
    g161: Circle CenterX=-12 CenterY=-72 CenterZ=0 NormalX=0 NormalY=0 NormalZ=1 AngleXU=0 Radius=1.3
    g162: GeomPoint X=-42 Y=-77 Z=0
    g163: Circle CenterX=-42 CenterY=-77 CenterZ=0 NormalX=0 NormalY=0 NormalZ=1 AngleXU=0 Radius=1.3
    g164: Circle CenterX=-37 CenterY=-77 CenterZ=0 NormalX=0 NormalY=0 NormalZ=1 AngleXU=0 Radius=1.3
    g165: Circle CenterX=-32 CenterY=-77 CenterZ=0 NormalX=0 NormalY=0 NormalZ=1 AngleXU=0 Radius=1.3
    g166: Circle CenterX=-27 CenterY=-77 CenterZ=0 NormalX=0 NormalY=0 NormalZ=1 AngleXU=0 Radius=1.3
    g167: Circle CenterX=-22 CenterY=-77 CenterZ=0 NormalX=0 NormalY=0 NormalZ=1 AngleXU=0 Radius=1.3
    g168: Circle CenterX=-17 CenterY=-77 CenterZ=0 NormalX=0 NormalY=0 NormalZ=1 AngleXU=0 Radius=1.3
    g169: Circle CenterX=-12 CenterY=-77 CenterZ=0 NormalX=0 NormalY=0 NormalZ=1 AngleXU=0 Radius=1.3
    g170: Circle CenterX=-47 CenterY=-47 CenterZ=0 NormalX=0 NormalY=0 NormalZ=1 AngleXU=0 Radius=1.3
    g171: Circle CenterX=-52 CenterY=-47 CenterZ=0 NormalX=0 NormalY=0 NormalZ=1 AngleXU=0 Radius=1.3
    g172: Circle CenterX=-57 CenterY=-47 CenterZ=0 NormalX=0 NormalY=0 NormalZ=1 AngleXU=0 Radius=1.3
    g173: Circle CenterX=-62 CenterY=-47 CenterZ=0 NormalX=0 NormalY=0 NormalZ=1 AngleXU=0 Radius=1.3
    g174: Circle CenterX=-67 CenterY=-47 CenterZ=0 NormalX=0 NormalY=0 NormalZ=1 AngleXU=0 Radius=1.3
    g175: Circle CenterX=-72 CenterY=-47 CenterZ=0 NormalX=0 NormalY=0 NormalZ=1 AngleXU=0 Radius=1.3
    g176: Circle CenterX=-47 CenterY=-52 CenterZ=0 NormalX=0 NormalY=0 NormalZ=1 AngleXU=0 Radius=1.3
    g177: Circle CenterX=-52 CenterY=-52 CenterZ=0 NormalX=0 NormalY=0 NormalZ=1 AngleXU=0 Radius=1.3
    g178: Circle CenterX=-57 CenterY=-52 CenterZ=0 NormalX=0 NormalY=0 NormalZ=1 AngleXU=0 Radius=1.3
    g179: Circle CenterX=-62 CenterY=-52 CenterZ=0 NormalX=0 NormalY=0 NormalZ=1 AngleXU=0 Radius=1.3
    g180: Circle CenterX=-67 CenterY=-52 CenterZ=0 NormalX=0 NormalY=0 NormalZ=1 AngleXU=0 Radius=1.3
    g181: Circle CenterX=-72 CenterY=-52 CenterZ=0 NormalX=0 NormalY=0 NormalZ=1 AngleXU=0 Radius=1.3
    g182: Circle CenterX=-47 CenterY=-57 CenterZ=0 NormalX=0 NormalY=0 NormalZ=1 AngleXU=0 Radius=1.3
    g183: Circle CenterX=-52 CenterY=-57 CenterZ=0 NormalX=0 NormalY=0 NormalZ=1 AngleXU=0 Radius=1.3
    g184: Circle CenterX=-57 CenterY=-57 CenterZ=0 NormalX=0 NormalY=0 NormalZ=1 AngleXU=0 Radius=1.3
    g185: Circle CenterX=-62 CenterY=-57 CenterZ=0 NormalX=0 NormalY=0 NormalZ=1 AngleXU=0 Radius=1.3
    g186: Circle CenterX=-67 CenterY=-57 CenterZ=0 NormalX=0 NormalY=0 NormalZ=1 AngleXU=0 Radius=1.3
    g187: Circle CenterX=-72 CenterY=-57 CenterZ=0 NormalX=0 NormalY=0 NormalZ=1 AngleXU=0 Radius=1.3
    g188: Circle CenterX=-47 CenterY=-62 CenterZ=0 NormalX=0 NormalY=0 NormalZ=1 AngleXU=0 Radius=1.3
    g189: Circle CenterX=-52 CenterY=-62 CenterZ=0 NormalX=0 NormalY=0 NormalZ=1 AngleXU=0 Radius=1.3
    g190: Circle CenterX=-57 CenterY=-62 CenterZ=0 NormalX=0 NormalY=0 NormalZ=1 AngleXU=0 Radius=1.3
    g191: Circle CenterX=-62 CenterY=-62 CenterZ=0 NormalX=0 NormalY=0 NormalZ=1 AngleXU=0 Radius=1.3
    g192: Circle CenterX=-67 CenterY=-62 CenterZ=0 NormalX=0 NormalY=0 NormalZ=1 AngleXU=0 Radius=1.3
    g193: Circle CenterX=-72 CenterY=-62 CenterZ=0 NormalX=0 NormalY=0 NormalZ=1 AngleXU=0 Radius=1.3
    g194: Circle CenterX=-47 CenterY=-67 CenterZ=0 NormalX=0 NormalY=0 NormalZ=1 AngleXU=0 Radius=1.3
    g195: Circle CenterX=-52 CenterY=-67 CenterZ=0 NormalX=0 NormalY=0 NormalZ=1 AngleXU=0 Radius=1.3
    g196: Circle CenterX=-57 CenterY=-67 CenterZ=0 NormalX=0 NormalY=0 NormalZ=1 AngleXU=0 Radius=1.3
    g197: Circle CenterX=-62 CenterY=-67 CenterZ=0 NormalX=0 NormalY=0 NormalZ=1 AngleXU=0 Radius=1.3
    g198: Circle CenterX=-67 CenterY=-67 CenterZ=0 NormalX=0 NormalY=0 NormalZ=1 AngleXU=0 Radius=1.3
    g199: Circle CenterX=-72 CenterY=-67 CenterZ=0 NormalX=0 NormalY=0 NormalZ=1 AngleXU=0 Radius=1.3
    g200: Circle CenterX=-47 CenterY=-72 CenterZ=0 NormalX=0 NormalY=0 NormalZ=1 AngleXU=0 Radius=1.3
    g201: Circle CenterX=-52 CenterY=-72 CenterZ=0 NormalX=0 NormalY=0 NormalZ=1 AngleXU=0 Radius=1.3
    g202: Circle CenterX=-57 CenterY=-72 CenterZ=0 NormalX=0 NormalY=0 NormalZ=1 AngleXU=0 Radius=1.3
    g203: Circle CenterX=-62 CenterY=-72 CenterZ=0 NormalX=0 NormalY=0 NormalZ=1 AngleXU=0 Radius=1.3
    g204: Circle CenterX=-67 CenterY=-72 CenterZ=0 NormalX=0 NormalY=0 NormalZ=1 AngleXU=0 Radius=1.3
    g205: Circle CenterX=-72 CenterY=-72 CenterZ=0 NormalX=0 NormalY=0 NormalZ=1 AngleXU=0 Radius=1.3
    g206: Circle CenterX=-47 CenterY=-77 CenterZ=0 NormalX=0 NormalY=0 NormalZ=1 AngleXU=0 Radius=1.3
    g207: Circle CenterX=-52 CenterY=-77 CenterZ=0 NormalX=0 NormalY=0 NormalZ=1 AngleXU=0 Radius=1.3
    g208: Circle CenterX=-57 CenterY=-77 CenterZ=0 NormalX=0 NormalY=0 NormalZ=1 AngleXU=0 Radius=1.3
    g209: Circle CenterX=-62 CenterY=-77 CenterZ=0 NormalX=0 NormalY=0 NormalZ=1 AngleXU=0 Radius=1.3
    g210: Circle CenterX=-67 CenterY=-77 CenterZ=0 NormalX=0 NormalY=0 NormalZ=1 AngleXU=0 Radius=1.3
    g211: Circle CenterX=-72 CenterY=-77 CenterZ=0 NormalX=0 NormalY=0 NormalZ=1 AngleXU=0 Radius=1.3
  constraints (215):
    c: Symmetric(g-4,g-4,g0)
    c: Symmetric(g-6,g-6,g0)
    c: Symmetric(g0,g0,g1)
    c: Diameter(g2) = 2.6
    c: Coincident(g2,g1)
    c: Diameter(g3) = 2.6
    c: Diameter(g4) = 2.6
    c: Diameter(g5) = 2.6
    c: Diameter(g6) = 2.6
    c: Diameter(g7) = 2.6
    c: Diameter(g8) = 2.6
    c: Diameter(g10) = 2.6
    c: Diameter(g18) = 2.6
    c: Diameter(g26) = 2.6
    c: Diameter(g34) = 2.6
    c: Diameter(g42) = 2.6
    c: Diameter(g50) = 2.6
    c: Diameter(g58) = 2.6
    c: Coincident(g10,g9)
    c: Coincident(g18,g17)
    c: Coincident(g26,g25)
    c: Coincident(g34,g33)
    c: Coincident(g42,g41)
    c: Coincident(g50,g49)
    c: Coincident(g58,g57)
    c: Diameter(g11) = 2.6
    c: Diameter(g19) = 2.6
    c: Diameter(g27) = 2.6
    c: Diameter(g35) = 2.6
    c: Diameter(g43) = 2.6
    c: Diameter(g51) = 2.6
    c: Diameter(g59) = 2.6
    c: Diameter(g12) = 2.6
    c: Diameter(g20) = 2.6
    c: Diameter(g28) = 2.6
    c: Diameter(g36) = 2.6
    c: Diameter(g44) = 2.6
    c: Diameter(g52) = 2.6
    c: Diameter(g60) = 2.6
    c: Diameter(g13) = 2.6
    c: Diameter(g21) = 2.6
    c: Diameter(g29) = 2.6
    c: Diameter(g37) = 2.6
    c: Diameter(g45) = 2.6
    c: Diameter(g53) = 2.6
    c: Diameter(g61) = 2.6
    c: Diameter(g14) = 2.6
    c: Diameter(g22) = 2.6
    c: Diameter(g30) = 2.6
    c: Diameter(g38) = 2.6
    c: Diameter(g46) = 2.6
    c: Diameter(g54) = 2.6
    c: Diameter(g62) = 2.6
    c: Diameter(g15) = 2.6
    c: Diameter(g23) = 2.6
    c: Diameter(g31) = 2.6
    c: Diameter(g39) = 2.6
    c: Diameter(g47) = 2.6
    c: Diameter(g55) = 2.6
    c: Diameter(g63) = 2.6
    c: Diameter(g16) = 2.6
    c: Diameter(g24) = 2.6
    c: Diameter(g32) = 2.6
    c: Diameter(g40) = 2.6
    c: Diameter(g48) = 2.6
    c: Diameter(g56) = 2.6
    c: Diameter(g64) = 2.6
    c: Symmetric(g-3,g-3,g65)
    c: Symmetric(g-5,g-5,g65)
    c: Diameter(g66) = 2.6
    c: Diameter(g67) = 2.6
    c: Diameter(g68) = 2.6
    c: Diameter(g69) = 2.6
    c: Diameter(g70) = 2.6
    c: Diameter(g71) = 2.6
    c: Diameter(g72) = 2.6
    c: Diameter(g78) = 2.6
    c: Diameter(g84) = 2.6
    c: Diameter(g90) = 2.6
    c: Diameter(g96) = 2.6
    c: Diameter(g102) = 2.6
    c: Diameter(g108) = 2.6
    c: Diameter(g73) = 2.6
    c: Diameter(g79) = 2.6
    c: Diameter(g85) = 2.6
    c: Diameter(g91) = 2.6
    c: Diameter(g97) = 2.6
    c: Diameter(g103) = 2.6
    c: Diameter(g109) = 2.6
    c: Diameter(g74) = 2.6
    c: Diameter(g80) = 2.6
    c: Diameter(g86) = 2.6
    c: Diameter(g92) = 2.6
    c: Diameter(g98) = 2.6
    c: Diameter(g104) = 2.6
    c: Diameter(g110) = 2.6
    c: Diameter(g75) = 2.6
    c: Diameter(g81) = 2.6
    c: Diameter(g87) = 2.6
    c: Diameter(g93) = 2.6
    c: Diameter(g99) = 2.6
    c: Diameter(g105) = 2.6
    c: Diameter(g111) = 2.6
    c: Diameter(g76) = 2.6
    c: Diameter(g82) = 2.6
    c: Diameter(g88) = 2.6
    c: Diameter(g94) = 2.6
    c: Diameter(g100) = 2.6
    c: Diameter(g106) = 2.6
    c: Diameter(g112) = 2.6
    c: Diameter(g77) = 2.6
    c: Diameter(g83) = 2.6
    c: Diameter(g89) = 2.6
    c: Diameter(g95) = 2.6
    c: Diameter(g101) = 2.6
    c: Diameter(g107) = 2.6
    c: Diameter(g113) = 2.6
    c: Diameter(g115) = 2.6
    c: Diameter(g123) = 2.6
    c: Diameter(g131) = 2.6
    c: Diameter(g139) = 2.6
    c: Diameter(g147) = 2.6
    c: Diameter(g155) = 2.6
    c: Diameter(g163) = 2.6
    c: Coincident(g115,g114)
    c: Coincident(g123,g122)
    c: Coincident(g131,g130)
    c: Coincident(g139,g138)
    c: Coincident(g147,g146)
    c: Coincident(g155,g154)
    c: Coincident(g163,g162)
    c: Diameter(g116) = 2.6
    c: Diameter(g124) = 2.6
    c: Diameter(g132) = 2.6
    c: Diameter(g140) = 2.6
    c: Diameter(g148) = 2.6
    c: Diameter(g156) = 2.6
    c: Diameter(g164) = 2.6
    c: Diameter(g117) = 2.6
    c: Diameter(g125) = 2.6
    c: Diameter(g133) = 2.6
    c: Diameter(g141) = 2.6
    c: Diameter(g149) = 2.6
    c: Diameter(g157) = 2.6
    c: Diameter(g165) = 2.6
    c: Diameter(g118) = 2.6
    c: Diameter(g126) = 2.6
    c: Diameter(g134) = 2.6
    c: Diameter(g142) = 2.6
    c: Diameter(g150) = 2.6
    c: Diameter(g158) = 2.6
    c: Diameter(g166) = 2.6
    c: Diameter(g119) = 2.6
    c: Diameter(g127) = 2.6
    c: Diameter(g135) = 2.6
    c: Diameter(g143) = 2.6
    c: Diameter(g151) = 2.6
    c: Diameter(g159) = 2.6
    c: Diameter(g167) = 2.6
    c: Diameter(g120) = 2.6
    c: Diameter(g128) = 2.6
    c: Diameter(g136) = 2.6
    c: Diameter(g144) = 2.6
    c: Diameter(g152) = 2.6
    c: Diameter(g160) = 2.6
    c: Diameter(g168) = 2.6
    c: Diameter(g121) = 2.6
    c: Diameter(g129) = 2.6
    c: Diameter(g137) = 2.6
    c: Diameter(g145) = 2.6
    c: Diameter(g153) = 2.6
    c: Diameter(g161) = 2.6
    c: Diameter(g169) = 2.6
    c: Diameter(g170) = 2.6
    c: Diameter(g176) = 2.6
    c: Diameter(g182) = 2.6
    c: Diameter(g188) = 2.6
    c: Diameter(g194) = 2.6
    c: Diameter(g200) = 2.6
    c: Diameter(g206) = 2.6
    c: Diameter(g171) = 2.6
    c: Diameter(g177) = 2.6
    c: Diameter(g183) = 2.6
    c: Diameter(g189) = 2.6
    c: Diameter(g195) = 2.6
    c: Diameter(g201) = 2.6
    c: Diameter(g207) = 2.6
    c: Diameter(g172) = 2.6
    c: Diameter(g178) = 2.6
    c: Diameter(g184) = 2.6
    c: Diameter(g190) = 2.6
    c: Diameter(g196) = 2.6
    c: Diameter(g202) = 2.6
    c: Diameter(g208) = 2.6
    c: Diameter(g173) = 2.6
    c: Diameter(g179) = 2.6
    c: Diameter(g185) = 2.6
    c: Diameter(g191) = 2.6
    c: Diameter(g197) = 2.6
    c: Diameter(g203) = 2.6
    c: Diameter(g209) = 2.6
    c: Diameter(g174) = 2.6
    c: Diameter(g180) = 2.6
    c: Diameter(g186) = 2.6
    c: Diameter(g192) = 2.6
    c: Diameter(g198) = 2.6
    c: Diameter(g204) = 2.6
    c: Diameter(g210) = 2.6
    c: Diameter(g175) = 2.6
    c: Diameter(g181) = 2.6
    c: Diameter(g187) = 2.6
    c: Diameter(g193) = 2.6
    c: Diameter(g199) = 2.6
    c: Diameter(g205) = 2.6
    c: Diameter(g211) = 2.6
FEATURE [PartDesign::Pocket] Pocket012
  BaseFeature = -> Pad018
  Direction = (-2.80598e-09,0,-1)
  Length = 8
  Length2 = 5
  Placement = pos=(7.67535e-08,-84,27.3536) rot=(0,0,1;3.14159rad)
  Profile = -> Sketch034
  ReferenceAxis = -> Sketch034 [N_Axis]
  Refine = true
  Suppressed = false
  Type = 0
FEATURE [PartDesign::Body] Body008  label="M3 5mm Spaced Mounting Plate"
  AllowCompound = false
  Group = -> [DatumPlane010,CopyPocket011,Sketch032,Pad017,Sketch033,Pad018,Sketch034,Pocket012]
  Origin = -> Origin008
  Tip = -> Pocket012
FEATURE [Sketcher::SketchObject] Sketch035
  ArcFitTolerance = 1e-06
  AttachmentSupport = -> [Pad012]
  FullyConstrained = true
  MakeInternals = false
  MapMode = 5
  Placement = pos=(42.0016,5.00002,14) rot=(0.577354,0.577344,0.577354;4.18878rad)
  sketch-geometry (1):
    g0: Circle CenterX=0 CenterY=0 CenterZ=0 NormalX=0 NormalY=0 NormalZ=1 AngleXU=0 Radius=1.35
  constraints (2):
    c: Diameter(g0) = 2.7
    c: Coincident(g0,g-1)
FEATURE [PartDesign::Pocket] Pocket013
  BaseFeature = -> Pad012
  Direction = (-1.755e-05,-1,-1.0234e-10)
  Length = 5
  Length2 = 5
  Placement = pos=(42,-84,14) rot=(0.57735,-0.57735,0.57735;2.0944rad)
  Profile = -> Sketch035
  ReferenceAxis = -> Sketch035 [N_Axis]
  Refine = true
  Suppressed = false
  Type = 0
FEATURE [Sketcher::SketchObject] Sketch036
  ArcFitTolerance = 1e-06
  AttachmentSupport = -> [Pocket013]
  ExternalGeometry = -> [Pocket013]
  FullyConstrained = true
  MakeInternals = false
  MapMode = 5
  Placement = pos=(42.0016,5.00002,14) rot=(0.577354,0.577344,0.577354;4.18878rad)
  sketch-geometry (2):
    g0: Circle CenterX=0 CenterY=0 CenterZ=0 NormalX=0 NormalY=0 NormalZ=1 AngleXU=0 Radius=2.5
    g1: Circle CenterX=0 CenterY=0 CenterZ=0 NormalX=0 NormalY=0 NormalZ=1 AngleXU=0 Radius=2.9
  constraints (4):
    c: Diameter(g0) = 5
    c: Coincident(g0,g-1)
    c: Coincident(g1,g0)
    c: Tangent(g1,g-3)
FEATURE [PartDesign::Pocket] Pocket014
  BaseFeature = -> Pocket013
  Direction = (-1.755e-05,-1,-1.0234e-10)
  Length = 10
  Length2 = 5
  Placement = pos=(42,-84,14) rot=(0.57735,-0.57735,0.57735;2.0944rad)
  Profile = -> Sketch036
  ReferenceAxis = -> Sketch036 [N_Axis]
  Refine = true
  Suppressed = false
  Type = 0
FEATURE [Sketcher::SketchObject] Sketch037
  ArcFitTolerance = 1e-06
  AttachmentSupport = -> [Pocket011]
  FullyConstrained = true
  MakeInternals = false
  MapMode = 5
  Placement = pos=(84,-84,-1.80021e-08) rot=(0.707107,0,0.707107;3.14159rad)
  sketch-geometry (3):
    g0: Circle CenterX=12.3536 CenterY=-21 CenterZ=0 NormalX=0 NormalY=0 NormalZ=1 AngleXU=0 Radius=3
    g1: Circle CenterX=12.3536 CenterY=-42 CenterZ=0 NormalX=0 NormalY=0 NormalZ=1 AngleXU=0 Radius=3
    g2: Circle CenterX=12.3536 CenterY=-63 CenterZ=0 NormalX=0 NormalY=0 NormalZ=1 AngleXU=0 Radius=3
  constraints (6):
    c: Diameter(g0) = 6
    c: Coincident(g0,g-3)
    c: Diameter(g1) = 6
    c: Coincident(g1,g-4)
    c: Diameter(g2) = 6
    c: Coincident(g2,g-5)
FEATURE [PartDesign::Pocket] Pocket015
  BaseFeature = -> Pocket011
  Direction = (-1,0,2.14311e-10)
  Length = 7
  Length2 = 5
  Placement = pos=(0,-84,2e-15) rot=(1,0,0;1.5708rad)
  Profile = -> Sketch037
  ReferenceAxis = -> Sketch037 [N_Axis]
  Refine = true
  Suppressed = false
  Type = 0
FEATURE [Sketcher::SketchObject] Sketch038
  ArcFitTolerance = 1e-06
  AttachmentSupport = -> [Fillet005]
  ExternalGeometry = -> [Fillet005]
  FullyConstrained = false
  MakeInternals = false
  MapMode = 5
  Placement = pos=(0,0,0) rot=(0.707107,0,-0.707107;3.14159rad)
  sketch-geometry (332):
    g0: LineSegment [constr] StartX=-5 StartY=0 StartZ=0 EndX=-5 EndY=1 EndZ=0
    g1: LineSegment StartX=-5 StartY=1 StartZ=0 EndX=-3.00761 EndY=1.17431 EndZ=0
    g2: LineSegment StartX=-5 StartY=1 StartZ=0 EndX=-3.00761 EndY=0.825689 EndZ=0
    g3: LineSegment StartX=-3.00761 StartY=0.825689 StartZ=0 EndX=-3.00761 EndY=1.17431 EndZ=0
    g4: LineSegment [constr] StartX=-5 StartY=1 StartZ=0 EndX=-5 EndY=2 EndZ=0
    g5: LineSegment StartX=-5 StartY=2 StartZ=0 EndX=-3.00761 EndY=2.17431 EndZ=0
    g6: LineSegment StartX=-5 StartY=2 StartZ=0 EndX=-3.00761 EndY=1.82569 EndZ=0
    g7: LineSegment StartX=-3.00761 StartY=1.82569 StartZ=0 EndX=-3.00761 EndY=2.17431 EndZ=0
    g8: LineSegment [constr] StartX=-5 StartY=2 StartZ=0 EndX=-5 EndY=3 EndZ=0
    g9: LineSegment StartX=-5 StartY=3 StartZ=0 EndX=-3.00761 EndY=3.17431 EndZ=0
    g10: LineSegment StartX=-5 StartY=3 StartZ=0 EndX=-3.00761 EndY=2.82569 EndZ=0
    g11: LineSegment StartX=-3.00761 StartY=2.82569 StartZ=0 EndX=-3.00761 EndY=3.17431 EndZ=0
    g12: LineSegment [constr] StartX=-5 StartY=3 StartZ=0 EndX=-5 EndY=4 EndZ=0
    g13: LineSegment StartX=-5 StartY=4 StartZ=0 EndX=-3.00761 EndY=4.17431 EndZ=0
    g14: LineSegment StartX=-5 StartY=4 StartZ=0 EndX=-3.00761 EndY=3.82569 EndZ=0
    g15: LineSegment StartX=-3.00761 StartY=3.82569 StartZ=0 EndX=-3.00761 EndY=4.17431 EndZ=0
    g16: LineSegment [constr] StartX=-5 StartY=4 StartZ=0 EndX=-5 EndY=5 EndZ=0
    g17: LineSegment StartX=-5 StartY=5 StartZ=0 EndX=-3.00761 EndY=5.17431 EndZ=0
    g18: LineSegment StartX=-5 StartY=5 StartZ=0 EndX=-3.00761 EndY=4.82569 EndZ=0
    g19: LineSegment StartX=-3.00761 StartY=4.82569 StartZ=0 EndX=-3.00761 EndY=5.17431 EndZ=0
    g20: LineSegment [constr] StartX=-5 StartY=5 StartZ=0 EndX=-5 EndY=6 EndZ=0
    g21: LineSegment StartX=-5 StartY=6 StartZ=0 EndX=-3.00761 EndY=6.17431 EndZ=0
    g22: LineSegment StartX=-5 StartY=6 StartZ=0 EndX=-3.00761 EndY=5.82569 EndZ=0
    g23: LineSegment StartX=-3.00761 StartY=5.82569 StartZ=0 EndX=-3.00761 EndY=6.17431 EndZ=0
    g24: LineSegment [constr] StartX=-5 StartY=6 StartZ=0 EndX=-5 EndY=7 EndZ=0
    g25: LineSegment StartX=-5 StartY=7 StartZ=0 EndX=-3.00761 EndY=7.17431 EndZ=0
    g26: LineSegment StartX=-5 StartY=7 StartZ=0 EndX=-3.00761 EndY=6.82569 EndZ=0
    g27: LineSegment StartX=-3.00761 StartY=6.82569 StartZ=0 EndX=-3.00761 EndY=7.17431 EndZ=0
    g28: LineSegment [constr] StartX=-5 StartY=7 StartZ=0 EndX=-5 EndY=8 EndZ=0
    g29: LineSegment StartX=-5 StartY=8 StartZ=0 EndX=-3.00761 EndY=8.17431 EndZ=0
    g30: LineSegment StartX=-5 StartY=8 StartZ=0 EndX=-3.00761 EndY=7.82569 EndZ=0
    g31: LineSegment StartX=-3.00761 StartY=7.82569 StartZ=0 EndX=-3.00761 EndY=8.17431 EndZ=0
    g32: LineSegment [constr] StartX=-5 StartY=8 StartZ=0 EndX=-5 EndY=9 EndZ=0
    g33: LineSegment StartX=-5 StartY=9 StartZ=0 EndX=-3.00761 EndY=9.17431 EndZ=0
    g34: LineSegment StartX=-5 StartY=9 StartZ=0 EndX=-3.00761 EndY=8.82569 EndZ=0
    g35: LineSegment StartX=-3.00761 StartY=8.82569 StartZ=0 EndX=-3.00761 EndY=9.17431 EndZ=0
    g36: LineSegment [constr] StartX=-5 StartY=9 StartZ=0 EndX=-5 EndY=10 EndZ=0
    g37: LineSegment StartX=-5 StartY=10 StartZ=0 EndX=-3.00761 EndY=10.1743 EndZ=0
    g38: LineSegment StartX=-5 StartY=10 StartZ=0 EndX=-3.00761 EndY=9.82569 EndZ=0
    g39: LineSegment StartX=-3.00761 StartY=9.82569 StartZ=0 EndX=-3.00761 EndY=10.1743 EndZ=0
    g40: LineSegment [constr] StartX=-5 StartY=10 StartZ=0 EndX=-5 EndY=11 EndZ=0
    g41: LineSegment StartX=-5 StartY=11 StartZ=0 EndX=-3.00761 EndY=11.1743 EndZ=0
    g42: LineSegment StartX=-5 StartY=11 StartZ=0 EndX=-3.00761 EndY=10.8257 EndZ=0
    g43: LineSegment StartX=-3.00761 StartY=10.8257 StartZ=0 EndX=-3.00761 EndY=11.1743 EndZ=0
    g44: LineSegment [constr] StartX=-5 StartY=11 StartZ=0 EndX=-5 EndY=12 EndZ=0
    g45: LineSegment StartX=-5 StartY=12 StartZ=0 EndX=-3.00761 EndY=12.1743 EndZ=0
    g46: LineSegment StartX=-5 StartY=12 StartZ=0 EndX=-3.00761 EndY=11.8257 EndZ=0
    g47: LineSegment StartX=-3.00761 StartY=11.8257 StartZ=0 EndX=-3.00761 EndY=12.1743 EndZ=0
    g48: LineSegment [constr] StartX=-5 StartY=12 StartZ=0 EndX=-5 EndY=13 EndZ=0
    g49: LineSegment StartX=-5 StartY=13 StartZ=0 EndX=-3.00761 EndY=13.1743 EndZ=0
    g50: LineSegment StartX=-5 StartY=13 StartZ=0 EndX=-3.00761 EndY=12.8257 EndZ=0
    g51: LineSegment StartX=-3.00761 StartY=12.8257 StartZ=0 EndX=-3.00761 EndY=13.1743 EndZ=0
    g52: LineSegment [constr] StartX=-5 StartY=13 StartZ=0 EndX=-5 EndY=14 EndZ=0
    g53: LineSegment StartX=-5 StartY=14 StartZ=0 EndX=-3.00761 EndY=14.1743 EndZ=0
    g54: LineSegment StartX=-5 StartY=14 StartZ=0 EndX=-3.00761 EndY=13.8257 EndZ=0
    g55: LineSegment StartX=-3.00761 StartY=13.8257 StartZ=0 EndX=-3.00761 EndY=14.1743 EndZ=0
    g56: LineSegment [constr] StartX=-5 StartY=14 StartZ=0 EndX=-5 EndY=15 EndZ=0
    g57: LineSegment StartX=-5 StartY=15 StartZ=0 EndX=-3.00761 EndY=15.1743 EndZ=0
    g58: LineSegment StartX=-5 StartY=15 StartZ=0 EndX=-3.00761 EndY=14.8257 EndZ=0
    g59: LineSegment StartX=-3.00761 StartY=14.8257 StartZ=0 EndX=-3.00761 EndY=15.1743 EndZ=0
    g60: LineSegment [constr] StartX=-5 StartY=15 StartZ=0 EndX=-5 EndY=16 EndZ=0
    g61: LineSegment StartX=-5 StartY=16 StartZ=0 EndX=-3.00761 EndY=16.1743 EndZ=0
    g62: LineSegment StartX=-5 StartY=16 StartZ=0 EndX=-3.00761 EndY=15.8257 EndZ=0
    g63: LineSegment StartX=-3.00761 StartY=15.8257 StartZ=0 EndX=-3.00761 EndY=16.1743 EndZ=0
    g64: LineSegment [constr] StartX=-5 StartY=16 StartZ=0 EndX=-5 EndY=17 EndZ=0
    g65: LineSegment StartX=-5 StartY=17 StartZ=0 EndX=-3.00761 EndY=17.1743 EndZ=0
    g66: LineSegment StartX=-5 StartY=17 StartZ=0 EndX=-3.00761 EndY=16.8257 EndZ=0
    g67: LineSegment StartX=-3.00761 StartY=16.8257 StartZ=0 EndX=-3.00761 EndY=17.1743 EndZ=0
    g68: LineSegment [constr] StartX=-5 StartY=17 StartZ=0 EndX=-5 EndY=18 EndZ=0
    g69: LineSegment StartX=-5 StartY=18 StartZ=0 EndX=-3.00761 EndY=18.1743 EndZ=0
    g70: LineSegment StartX=-5 StartY=18 StartZ=0 EndX=-3.00761 EndY=17.8257 EndZ=0
    g71: LineSegment StartX=-3.00761 StartY=17.8257 StartZ=0 EndX=-3.00761 EndY=18.1743 EndZ=0
    g72: LineSegment [constr] StartX=-5 StartY=18 StartZ=0 EndX=-5 EndY=19 EndZ=0
    g73: LineSegment StartX=-5 StartY=19 StartZ=0 EndX=-3.00761 EndY=19.1743 EndZ=0
    g74: LineSegment StartX=-5 StartY=19 StartZ=0 EndX=-3.00761 EndY=18.8257 EndZ=0
    g75: LineSegment StartX=-3.00761 StartY=18.8257 StartZ=0 EndX=-3.00761 EndY=19.1743 EndZ=0
    g76: LineSegment [constr] StartX=-5 StartY=19 StartZ=0 EndX=-5 EndY=20 EndZ=0
    g77: LineSegment StartX=-5 StartY=20 StartZ=0 EndX=-3.00761 EndY=20.1743 EndZ=0
    g78: LineSegment StartX=-5 StartY=20 StartZ=0 EndX=-3.00761 EndY=19.8257 EndZ=0
    g79: LineSegment StartX=-3.00761 StartY=19.8257 StartZ=0 EndX=-3.00761 EndY=20.1743 EndZ=0
    g80: LineSegment [constr] StartX=-5 StartY=20 StartZ=0 EndX=-5 EndY=21 EndZ=0
    g81: LineSegment StartX=-5 StartY=21 StartZ=0 EndX=-3.00761 EndY=21.1743 EndZ=0
    g82: LineSegment StartX=-5 StartY=21 StartZ=0 EndX=-3.00761 EndY=20.8257 EndZ=0
    g83: LineSegment StartX=-3.00761 StartY=20.8257 StartZ=0 EndX=-3.00761 EndY=21.1743 EndZ=0
    g84: LineSegment [constr] StartX=-5 StartY=21 StartZ=0 EndX=-5 EndY=22 EndZ=0
    g85: LineSegment StartX=-5 StartY=22 StartZ=0 EndX=-3.00761 EndY=22.1743 EndZ=0
    g86: LineSegment StartX=-5 StartY=22 StartZ=0 EndX=-3.00761 EndY=21.8257 EndZ=0
    g87: LineSegment StartX=-3.00761 StartY=21.8257 StartZ=0 EndX=-3.00761 EndY=22.1743 EndZ=0
    g88: LineSegment [constr] StartX=-5 StartY=22 StartZ=0 EndX=-5 EndY=23 EndZ=0
    g89: LineSegment StartX=-5 StartY=23 StartZ=0 EndX=-3.00761 EndY=23.1743 EndZ=0
    g90: LineSegment StartX=-5 StartY=23 StartZ=0 EndX=-3.00761 EndY=22.8257 EndZ=0
    g91: LineSegment StartX=-3.00761 StartY=22.8257 StartZ=0 EndX=-3.00761 EndY=23.1743 EndZ=0
    g92: LineSegment [constr] StartX=-5 StartY=23 StartZ=0 EndX=-5 EndY=24 EndZ=0
    g93: LineSegment StartX=-5 StartY=24 StartZ=0 EndX=-3.00761 EndY=24.1743 EndZ=0
    g94: LineSegment StartX=-5 StartY=24 StartZ=0 EndX=-3.00761 EndY=23.8257 EndZ=0
    g95: LineSegment StartX=-3.00761 StartY=23.8257 StartZ=0 EndX=-3.00761 EndY=24.1743 EndZ=0
    g96: LineSegment [constr] StartX=-5 StartY=24 StartZ=0 EndX=-5 EndY=25 EndZ=0
    g97: LineSegment StartX=-5 StartY=25 StartZ=0 EndX=-3.00761 EndY=25.1743 EndZ=0
    g98: LineSegment StartX=-5 StartY=25 StartZ=0 EndX=-3.00761 EndY=24.8257 EndZ=0
    g99: LineSegment StartX=-3.00761 StartY=24.8257 StartZ=0 EndX=-3.00761 EndY=25.1743 EndZ=0
    g100: LineSegment [constr] StartX=-5 StartY=25 StartZ=0 EndX=-5 EndY=26 EndZ=0
    g101: LineSegment StartX=-5 StartY=26 StartZ=0 EndX=-3.00761 EndY=26.1743 EndZ=0
    g102: LineSegment StartX=-5 StartY=26 StartZ=0 EndX=-3.00761 EndY=25.8257 EndZ=0
    g103: LineSegment StartX=-3.00761 StartY=25.8257 StartZ=0 EndX=-3.00761 EndY=26.1743 EndZ=0
    g104: LineSegment [constr] StartX=-5 StartY=26 StartZ=0 EndX=-5 EndY=27 EndZ=0
    g105: LineSegment StartX=-5 StartY=27 StartZ=0 EndX=-3.00761 EndY=27.1743 EndZ=0
    g106: LineSegment StartX=-5 StartY=27 StartZ=0 EndX=-3.00761 EndY=26.8257 EndZ=0
    g107: LineSegment StartX=-3.00761 StartY=26.8257 StartZ=0 EndX=-3.00761 EndY=27.1743 EndZ=0
    g108: LineSegment [constr] StartX=-5 StartY=27 StartZ=0 EndX=-5 EndY=28 EndZ=0
    g109: LineSegment StartX=-5 StartY=28 StartZ=0 EndX=-3.00761 EndY=28.1743 EndZ=0
    g110: LineSegment StartX=-5 StartY=28 StartZ=0 EndX=-3.00761 EndY=27.8257 EndZ=0
    g111: LineSegment StartX=-3.00761 StartY=27.8257 StartZ=0 EndX=-3.00761 EndY=28.1743 EndZ=0
    g112: LineSegment [constr] StartX=-5 StartY=28 StartZ=0 EndX=-5 EndY=29 EndZ=0
    g113: LineSegment StartX=-5 StartY=29 StartZ=0 EndX=-3.00761 EndY=29.1743 EndZ=0
    g114: LineSegment StartX=-5 StartY=29 StartZ=0 EndX=-3.00761 EndY=28.8257 EndZ=0
    g115: LineSegment StartX=-3.00761 StartY=28.8257 StartZ=0 EndX=-3.00761 EndY=29.1743 EndZ=0
    g116: LineSegment [constr] StartX=-5 StartY=29 StartZ=0 EndX=-5 EndY=30 EndZ=0
    g117: LineSegment StartX=-5 StartY=30 StartZ=0 EndX=-3.00761 EndY=30.1743 EndZ=0
    g118: LineSegment StartX=-5 StartY=30 StartZ=0 EndX=-3.00761 EndY=29.8257 EndZ=0
    g119: LineSegment StartX=-3.00761 StartY=29.8257 StartZ=0 EndX=-3.00761 EndY=30.1743 EndZ=0
    g120: LineSegment [constr] StartX=-5 StartY=30 StartZ=0 EndX=-5 EndY=31 EndZ=0
    g121: LineSegment StartX=-5 StartY=31 StartZ=0 EndX=-3.00761 EndY=31.1743 EndZ=0
    g122: LineSegment StartX=-5 StartY=31 StartZ=0 EndX=-3.00761 EndY=30.8257 EndZ=0
    g123: LineSegment StartX=-3.00761 StartY=30.8257 StartZ=0 EndX=-3.00761 EndY=31.1743 EndZ=0
    g124: LineSegment [constr] StartX=-5 StartY=31 StartZ=0 EndX=-5 EndY=32 EndZ=0
    g125: LineSegment StartX=-5 StartY=32 StartZ=0 EndX=-3.00761 EndY=32.1743 EndZ=0
    g126: LineSegment StartX=-5 StartY=32 StartZ=0 EndX=-3.00761 EndY=31.8257 EndZ=0
    g127: LineSegment StartX=-3.00761 StartY=31.8257 StartZ=0 EndX=-3.00761 EndY=32.1743 EndZ=0
    g128: LineSegment [constr] StartX=-5 StartY=32 StartZ=0 EndX=-5 EndY=33 EndZ=0
    g129: LineSegment StartX=-5 StartY=33 StartZ=0 EndX=-3.00761 EndY=33.1743 EndZ=0
    g130: LineSegment StartX=-5 StartY=33 StartZ=0 EndX=-3.00761 EndY=32.8257 EndZ=0
    g131: LineSegment StartX=-3.00761 StartY=32.8257 StartZ=0 EndX=-3.00761 EndY=33.1743 EndZ=0
    g132: LineSegment [constr] StartX=-5 StartY=33 StartZ=0 EndX=-5 EndY=34 EndZ=0
    g133: LineSegment StartX=-5 StartY=34 StartZ=0 EndX=-3.00761 EndY=34.1743 EndZ=0
    g134: LineSegment StartX=-5 StartY=34 StartZ=0 EndX=-3.00761 EndY=33.8257 EndZ=0
    g135: LineSegment StartX=-3.00761 StartY=33.8257 StartZ=0 EndX=-3.00761 EndY=34.1743 EndZ=0
    g136: LineSegment [constr] StartX=-5 StartY=34 StartZ=0 EndX=-5 EndY=35 EndZ=0
    g137: LineSegment StartX=-5 StartY=35 StartZ=0 EndX=-3.00761 EndY=35.1743 EndZ=0
    g138: LineSegment StartX=-5 StartY=35 StartZ=0 EndX=-3.00761 EndY=34.8257 EndZ=0
    g139: LineSegment StartX=-3.00761 StartY=34.8257 StartZ=0 EndX=-3.00761 EndY=35.1743 EndZ=0
    g140: LineSegment [constr] StartX=-5 StartY=35 StartZ=0 EndX=-5 EndY=36 EndZ=0
    g141: LineSegment StartX=-5 StartY=36 StartZ=0 EndX=-3.00761 EndY=36.1743 EndZ=0
    g142: LineSegment StartX=-5 StartY=36 StartZ=0 EndX=-3.00761 EndY=35.8257 EndZ=0
    g143: LineSegment StartX=-3.00761 StartY=35.8257 StartZ=0 EndX=-3.00761 EndY=36.1743 EndZ=0
    g144: LineSegment [constr] StartX=-5 StartY=36 StartZ=0 EndX=-5 EndY=37 EndZ=0
    g145: LineSegment StartX=-5 StartY=37 StartZ=0 EndX=-3.00761 EndY=37.1743 EndZ=0
    g146: LineSegment StartX=-5 StartY=37 StartZ=0 EndX=-3.00761 EndY=36.8257 EndZ=0
    g147: LineSegment StartX=-3.00761 StartY=36.8257 StartZ=0 EndX=-3.00761 EndY=37.1743 EndZ=0
    g148: LineSegment [constr] StartX=-5 StartY=37 StartZ=0 EndX=-5 EndY=38 EndZ=0
    g149: LineSegment StartX=-5 StartY=38 StartZ=0 EndX=-3.00761 EndY=38.1743 EndZ=0
    g150: LineSegment StartX=-5 StartY=38 StartZ=0 EndX=-3.00761 EndY=37.8257 EndZ=0
    g151: LineSegment StartX=-3.00761 StartY=37.8257 StartZ=0 EndX=-3.00761 EndY=38.1743 EndZ=0
    g152: LineSegment [constr] StartX=-5 StartY=38 StartZ=0 EndX=-5 EndY=39 EndZ=0
    g153: LineSegment StartX=-5 StartY=39 StartZ=0 EndX=-3.00761 EndY=39.1743 EndZ=0
    g154: LineSegment StartX=-5 StartY=39 StartZ=0 EndX=-3.00761 EndY=38.8257 EndZ=0
    g155: LineSegment StartX=-3.00761 StartY=38.8257 StartZ=0 EndX=-3.00761 EndY=39.1743 EndZ=0
    g156: LineSegment [constr] StartX=-5 StartY=39 StartZ=0 EndX=-5 EndY=40 EndZ=0
    g157: LineSegment StartX=-5 StartY=40 StartZ=0 EndX=-3.00761 EndY=40.1743 EndZ=0
    g158: LineSegment StartX=-5 StartY=40 StartZ=0 EndX=-3.00761 EndY=39.8257 EndZ=0
    g159: LineSegment StartX=-3.00761 StartY=39.8257 StartZ=0 EndX=-3.00761 EndY=40.1743 EndZ=0
    g160: LineSegment [constr] StartX=-5 StartY=40 StartZ=0 EndX=-5 EndY=41 EndZ=0
    g161: LineSegment StartX=-5 StartY=41 StartZ=0 EndX=-3.00761 EndY=41.1743 EndZ=0
    g162: LineSegment StartX=-5 StartY=41 StartZ=0 EndX=-3.00761 EndY=40.8257 EndZ=0
    g163: LineSegment StartX=-3.00761 StartY=40.8257 StartZ=0 EndX=-3.00761 EndY=41.1743 EndZ=0
    g164: LineSegment [constr] StartX=-5 StartY=41 StartZ=0 EndX=-5 EndY=42 EndZ=0
    g165: LineSegment StartX=-5 StartY=42 StartZ=0 EndX=-3.00761 EndY=42.1743 EndZ=0
    g166: LineSegment StartX=-5 StartY=42 StartZ=0 EndX=-3.00761 EndY=41.8257 EndZ=0
    g167: LineSegment StartX=-3.00761 StartY=41.8257 StartZ=0 EndX=-3.00761 EndY=42.1743 EndZ=0
    g168: LineSegment [constr] StartX=-5 StartY=42 StartZ=0 EndX=-5 EndY=43 EndZ=0
    g169: LineSegment StartX=-5 StartY=43 StartZ=0 EndX=-3.00761 EndY=43.1743 EndZ=0
    g170: LineSegment StartX=-5 StartY=43 StartZ=0 EndX=-3.00761 EndY=42.8257 EndZ=0
    g171: LineSegment StartX=-3.00761 StartY=42.8257 StartZ=0 EndX=-3.00761 EndY=43.1743 EndZ=0
    g172: LineSegment [constr] StartX=-5 StartY=43 StartZ=0 EndX=-5 EndY=44 EndZ=0
    g173: LineSegment StartX=-5 StartY=44 StartZ=0 EndX=-3.00761 EndY=44.1743 EndZ=0
    g174: LineSegment StartX=-5 StartY=44 StartZ=0 EndX=-3.00761 EndY=43.8257 EndZ=0
    g175: LineSegment StartX=-3.00761 StartY=43.8257 StartZ=0 EndX=-3.00761 EndY=44.1743 EndZ=0
    g176: LineSegment [constr] StartX=-5 StartY=44 StartZ=0 EndX=-5 EndY=45 EndZ=0
    g177: LineSegment StartX=-5 StartY=45 StartZ=0 EndX=-3.00761 EndY=45.1743 EndZ=0
    g178: LineSegment StartX=-5 StartY=45 StartZ=0 EndX=-3.00761 EndY=44.8257 EndZ=0
    g179: LineSegment StartX=-3.00761 StartY=44.8257 StartZ=0 EndX=-3.00761 EndY=45.1743 EndZ=0
    g180: LineSegment [constr] StartX=-5 StartY=45 StartZ=0 EndX=-5 EndY=46 EndZ=0
    g181: LineSegment StartX=-5 StartY=46 StartZ=0 EndX=-3.00761 EndY=46.1743 EndZ=0
    g182: LineSegment StartX=-5 StartY=46 StartZ=0 EndX=-3.00761 EndY=45.8257 EndZ=0
    g183: LineSegment StartX=-3.00761 StartY=45.8257 StartZ=0 EndX=-3.00761 EndY=46.1743 EndZ=0
    g184: LineSegment [constr] StartX=-5 StartY=46 StartZ=0 EndX=-5 EndY=47 EndZ=0
    g185: LineSegment StartX=-5 StartY=47 StartZ=0 EndX=-3.00761 EndY=47.1743 EndZ=0
    g186: LineSegment StartX=-5 StartY=47 StartZ=0 EndX=-3.00761 EndY=46.8257 EndZ=0
    g187: LineSegment StartX=-3.00761 StartY=46.8257 StartZ=0 EndX=-3.00761 EndY=47.1743 EndZ=0
    g188: LineSegment [constr] StartX=-5 StartY=47 StartZ=0 EndX=-5 EndY=48 EndZ=0
    g189: LineSegment StartX=-5 StartY=48 StartZ=0 EndX=-3.00761 EndY=48.1743 EndZ=0
    g190: LineSegment StartX=-5 StartY=48 StartZ=0 EndX=-3.00761 EndY=47.8257 EndZ=0
    g191: LineSegment StartX=-3.00761 StartY=47.8257 StartZ=0 EndX=-3.00761 EndY=48.1743 EndZ=0
    g192: LineSegment [constr] StartX=-5 StartY=48 StartZ=0 EndX=-5 EndY=49 EndZ=0
    g193: LineSegment StartX=-5 StartY=49 StartZ=0 EndX=-3.00761 EndY=49.1743 EndZ=0
    g194: LineSegment StartX=-5 StartY=49 StartZ=0 EndX=-3.00761 EndY=48.8257 EndZ=0
    g195: LineSegment StartX=-3.00761 StartY=48.8257 StartZ=0 EndX=-3.00761 EndY=49.1743 EndZ=0
    g196: LineSegment [constr] StartX=-5 StartY=49 StartZ=0 EndX=-5 EndY=50 EndZ=0
    g197: LineSegment StartX=-5 StartY=50 StartZ=0 EndX=-3.00761 EndY=50.1743 EndZ=0
    g198: LineSegment StartX=-5 StartY=50 StartZ=0 EndX=-3.00761 EndY=49.8257 EndZ=0
    g199: LineSegment StartX=-3.00761 StartY=49.8257 StartZ=0 EndX=-3.00761 EndY=50.1743 EndZ=0
    g200: LineSegment [constr] StartX=-5 StartY=50 StartZ=0 EndX=-5 EndY=51 EndZ=0
    g201: LineSegment StartX=-5 StartY=51 StartZ=0 EndX=-3.00761 EndY=51.1743 EndZ=0
    g202: LineSegment StartX=-5 StartY=51 StartZ=0 EndX=-3.00761 EndY=50.8257 EndZ=0
    g203: LineSegment StartX=-3.00761 StartY=50.8257 StartZ=0 EndX=-3.00761 EndY=51.1743 EndZ=0
    g204: LineSegment [constr] StartX=-5 StartY=51 StartZ=0 EndX=-5 EndY=52 EndZ=0
    g205: LineSegment StartX=-5 StartY=52 StartZ=0 EndX=-3.00761 EndY=52.1743 EndZ=0
    g206: LineSegment StartX=-5 StartY=52 StartZ=0 EndX=-3.00761 EndY=51.8257 EndZ=0
    g207: LineSegment StartX=-3.00761 StartY=51.8257 StartZ=0 EndX=-3.00761 EndY=52.1743 EndZ=0
    g208: LineSegment [constr] StartX=-5 StartY=52 StartZ=0 EndX=-5 EndY=53 EndZ=0
    g209: LineSegment StartX=-5 StartY=53 StartZ=0 EndX=-3.00761 EndY=53.1743 EndZ=0
    g210: LineSegment StartX=-5 StartY=53 StartZ=0 EndX=-3.00761 EndY=52.8257 EndZ=0
    g211: LineSegment StartX=-3.00761 StartY=52.8257 StartZ=0 EndX=-3.00761 EndY=53.1743 EndZ=0
    g212: LineSegment [constr] StartX=-5 StartY=53 StartZ=0 EndX=-5 EndY=54 EndZ=0
    g213: LineSegment StartX=-5 StartY=54 StartZ=0 EndX=-3.00761 EndY=54.1743 EndZ=0
    g214: LineSegment StartX=-5 StartY=54 StartZ=0 EndX=-3.00761 EndY=53.8257 EndZ=0
    g215: LineSegment StartX=-3.00761 StartY=53.8257 StartZ=0 EndX=-3.00761 EndY=54.1743 EndZ=0
    g216: LineSegment [constr] StartX=-5 StartY=54 StartZ=0 EndX=-5 EndY=55 EndZ=0
    g217: LineSegment StartX=-5 StartY=55 StartZ=0 EndX=-3.00761 EndY=55.1743 EndZ=0
    g218: LineSegment StartX=-5 StartY=55 StartZ=0 EndX=-3.00761 EndY=54.8257 EndZ=0
    g219: LineSegment StartX=-3.00761 StartY=54.8257 StartZ=0 EndX=-3.00761 EndY=55.1743 EndZ=0
    g220: LineSegment [constr] StartX=-5 StartY=55 StartZ=0 EndX=-5 EndY=56 EndZ=0
    g221: LineSegment StartX=-5 StartY=56 StartZ=0 EndX=-3.00761 EndY=56.1743 EndZ=0
    g222: LineSegment StartX=-5 StartY=56 StartZ=0 EndX=-3.00761 EndY=55.8257 EndZ=0
    g223: LineSegment StartX=-3.00761 StartY=55.8257 StartZ=0 EndX=-3.00761 EndY=56.1743 EndZ=0
    g224: LineSegment [constr] StartX=-5 StartY=56 StartZ=0 EndX=-5 EndY=57 EndZ=0
    g225: LineSegment StartX=-5 StartY=57 StartZ=0 EndX=-3.00761 EndY=57.1743 EndZ=0
    g226: LineSegment StartX=-5 StartY=57 StartZ=0 EndX=-3.00761 EndY=56.8257 EndZ=0
    g227: LineSegment StartX=-3.00761 StartY=56.8257 StartZ=0 EndX=-3.00761 EndY=57.1743 EndZ=0
    g228: LineSegment [constr] StartX=-5 StartY=57 StartZ=0 EndX=-5 EndY=58 EndZ=0
    g229: LineSegment StartX=-5 StartY=58 StartZ=0 EndX=-3.00761 EndY=58.1743 EndZ=0
    g230: LineSegment StartX=-5 StartY=58 StartZ=0 EndX=-3.00761 EndY=57.8257 EndZ=0
    g231: LineSegment StartX=-3.00761 StartY=57.8257 StartZ=0 EndX=-3.00761 EndY=58.1743 EndZ=0
    g232: LineSegment [constr] StartX=-5 StartY=58 StartZ=0 EndX=-5 EndY=59 EndZ=0
    g233: LineSegment StartX=-5 StartY=59 StartZ=0 EndX=-3.00761 EndY=59.1743 EndZ=0
    g234: LineSegment StartX=-5 StartY=59 StartZ=0 EndX=-3.00761 EndY=58.8257 EndZ=0
    g235: LineSegment StartX=-3.00761 StartY=58.8257 StartZ=0 EndX=-3.00761 EndY=59.1743 EndZ=0
    g236: LineSegment [constr] StartX=-5 StartY=59 StartZ=0 EndX=-5 EndY=60 EndZ=0
    g237: LineSegment StartX=-5 StartY=60 StartZ=0 EndX=-3.00761 EndY=60.1743 EndZ=0
    g238: LineSegment StartX=-5 StartY=60 StartZ=0 EndX=-3.00761 EndY=59.8257 EndZ=0
    g239: LineSegment StartX=-3.00761 StartY=59.8257 StartZ=0 EndX=-3.00761 EndY=60.1743 EndZ=0
    g240: LineSegment [constr] StartX=-5 StartY=60 StartZ=0 EndX=-5 EndY=61 EndZ=0
    g241: LineSegment StartX=-5 StartY=61 StartZ=0 EndX=-3.00761 EndY=61.1743 EndZ=0
    g242: LineSegment StartX=-5 StartY=61 StartZ=0 EndX=-3.00761 EndY=60.8257 EndZ=0
    g243: LineSegment StartX=-3.00761 StartY=60.8257 StartZ=0 EndX=-3.00761 EndY=61.1743 EndZ=0
    g244: LineSegment [constr] StartX=-5 StartY=61 StartZ=0 EndX=-5 EndY=62 EndZ=0
    g245: LineSegment StartX=-5 StartY=62 StartZ=0 EndX=-3.00761 EndY=62.1743 EndZ=0
    g246: LineSegment StartX=-5 StartY=62 StartZ=0 EndX=-3.00761 EndY=61.8257 EndZ=0
    g247: LineSegment StartX=-3.00761 StartY=61.8257 StartZ=0 EndX=-3.00761 EndY=62.1743 EndZ=0
    g248: LineSegment [constr] StartX=-5 StartY=62 StartZ=0 EndX=-5 EndY=63 EndZ=0
    g249: LineSegment StartX=-5 StartY=63 StartZ=0 EndX=-3.00761 EndY=63.1743 EndZ=0
    g250: LineSegment StartX=-5 StartY=63 StartZ=0 EndX=-3.00761 EndY=62.8257 EndZ=0
    g251: LineSegment StartX=-3.00761 StartY=62.8257 StartZ=0 EndX=-3.00761 EndY=63.1743 EndZ=0
    g252: LineSegment [constr] StartX=-5 StartY=63 StartZ=0 EndX=-5 EndY=64 EndZ=0
    g253: LineSegment StartX=-5 StartY=64 StartZ=0 EndX=-3.00761 EndY=64.1743 EndZ=0
    g254: LineSegment StartX=-5 StartY=64 StartZ=0 EndX=-3.00761 EndY=63.8257 EndZ=0
    g255: LineSegment StartX=-3.00761 StartY=63.8257 StartZ=0 EndX=-3.00761 EndY=64.1743 EndZ=0
    g256: LineSegment [constr] StartX=-5 StartY=64 StartZ=0 EndX=-5 EndY=65 EndZ=0
    g257: LineSegment StartX=-5 StartY=65 StartZ=0 EndX=-3.00761 EndY=65.1743 EndZ=0
    g258: LineSegment StartX=-5 StartY=65 StartZ=0 EndX=-3.00761 EndY=64.8257 EndZ=0
    g259: LineSegment StartX=-3.00761 StartY=64.8257 StartZ=0 EndX=-3.00761 EndY=65.1743 EndZ=0
    g260: LineSegment [constr] StartX=-5 StartY=65 StartZ=0 EndX=-5 EndY=66 EndZ=0
    g261: LineSegment StartX=-5 StartY=66 StartZ=0 EndX=-3.00761 EndY=66.1743 EndZ=0
    g262: LineSegment StartX=-5 StartY=66 StartZ=0 EndX=-3.00761 EndY=65.8257 EndZ=0
    g263: LineSegment StartX=-3.00761 StartY=65.8257 StartZ=0 EndX=-3.00761 EndY=66.1743 EndZ=0
    g264: LineSegment [constr] StartX=-5 StartY=66 StartZ=0 EndX=-5 EndY=67 EndZ=0
    g265: LineSegment StartX=-5 StartY=67 StartZ=0 EndX=-3.00761 EndY=67.1743 EndZ=0
    g266: LineSegment StartX=-5 StartY=67 StartZ=0 EndX=-3.00761 EndY=66.8257 EndZ=0
    g267: LineSegment StartX=-3.00761 StartY=66.8257 StartZ=0 EndX=-3.00761 EndY=67.1743 EndZ=0
    g268: LineSegment [constr] StartX=-5 StartY=67 StartZ=0 EndX=-5 EndY=68 EndZ=0
    g269: LineSegment StartX=-5 StartY=68 StartZ=0 EndX=-3.00761 EndY=68.1743 EndZ=0
    g270: LineSegment StartX=-5 StartY=68 StartZ=0 EndX=-3.00761 EndY=67.8257 EndZ=0
    g271: LineSegment StartX=-3.00761 StartY=67.8257 StartZ=0 EndX=-3.00761 EndY=68.1743 EndZ=0
    g272: LineSegment [constr] StartX=-5 StartY=68 StartZ=0 EndX=-5 EndY=69 EndZ=0
    g273: LineSegment StartX=-5 StartY=69 StartZ=0 EndX=-3.00761 EndY=69.1743 EndZ=0
    g274: LineSegment StartX=-5 StartY=69 StartZ=0 EndX=-3.00761 EndY=68.8257 EndZ=0
    g275: LineSegment StartX=-3.00761 StartY=68.8257 StartZ=0 EndX=-3.00761 EndY=69.1743 EndZ=0
    g276: LineSegment [constr] StartX=-5 StartY=69 StartZ=0 EndX=-5 EndY=70 EndZ=0
    g277: LineSegment StartX=-5 StartY=70 StartZ=0 EndX=-3.00761 EndY=70.1743 EndZ=0
    g278: LineSegment StartX=-5 StartY=70 StartZ=0 EndX=-3.00761 EndY=69.8257 EndZ=0
    g279: LineSegment StartX=-3.00761 StartY=69.8257 StartZ=0 EndX=-3.00761 EndY=70.1743 EndZ=0
    g280: LineSegment [constr] StartX=-5 StartY=70 StartZ=0 EndX=-5 EndY=71 EndZ=0
    g281: LineSegment StartX=-5 StartY=71 StartZ=0 EndX=-3.00761 EndY=71.1743 EndZ=0
    g282: LineSegment StartX=-5 StartY=71 StartZ=0 EndX=-3.00761 EndY=70.8257 EndZ=0
    g283: LineSegment StartX=-3.00761 StartY=70.8257 StartZ=0 EndX=-3.00761 EndY=71.1743 EndZ=0
    g284: LineSegment [constr] StartX=-5 StartY=71 StartZ=0 EndX=-5 EndY=72 EndZ=0
    g285: LineSegment StartX=-5 StartY=72 StartZ=0 EndX=-3.00761 EndY=72.1743 EndZ=0
    g286: LineSegment StartX=-5 StartY=72 StartZ=0 EndX=-3.00761 EndY=71.8257 EndZ=0
    g287: LineSegment StartX=-3.00761 StartY=71.8257 StartZ=0 EndX=-3.00761 EndY=72.1743 EndZ=0
    g288: LineSegment [constr] StartX=-5 StartY=72 StartZ=0 EndX=-5 EndY=73 EndZ=0
    g289: LineSegment StartX=-5 StartY=73 StartZ=0 EndX=-3.00761 EndY=73.1743 EndZ=0
    g290: LineSegment StartX=-5 StartY=73 StartZ=0 EndX=-3.00761 EndY=72.8257 EndZ=0
    g291: LineSegment StartX=-3.00761 StartY=72.8257 StartZ=0 EndX=-3.00761 EndY=73.1743 EndZ=0
    g292: LineSegment [constr] StartX=-5 StartY=73 StartZ=0 EndX=-5 EndY=74 EndZ=0
    g293: LineSegment StartX=-5 StartY=74 StartZ=0 EndX=-3.00761 EndY=74.1743 EndZ=0
    g294: LineSegment StartX=-5 StartY=74 StartZ=0 EndX=-3.00761 EndY=73.8257 EndZ=0
    g295: LineSegment StartX=-3.00761 StartY=73.8257 StartZ=0 EndX=-3.00761 EndY=74.1743 EndZ=0
    g296: LineSegment [constr] StartX=-5 StartY=74 StartZ=0 EndX=-5 EndY=75 EndZ=0
    g297: LineSegment StartX=-5 StartY=75 StartZ=0 EndX=-3.00761 EndY=75.1743 EndZ=0
    g298: LineSegment StartX=-5 StartY=75 StartZ=0 EndX=-3.00761 EndY=74.8257 EndZ=0
    g299: LineSegment StartX=-3.00761 StartY=74.8257 StartZ=0 EndX=-3.00761 EndY=75.1743 EndZ=0
    g300: LineSegment [constr] StartX=-5 StartY=75 StartZ=0 EndX=-5 EndY=76 EndZ=0
    g301: LineSegment StartX=-5 StartY=76 StartZ=0 EndX=-3.00761 EndY=76.1743 EndZ=0
    g302: LineSegment StartX=-5 StartY=76 StartZ=0 EndX=-3.00761 EndY=75.8257 EndZ=0
    g303: LineSegment StartX=-3.00761 StartY=75.8257 StartZ=0 EndX=-3.00761 EndY=76.1743 EndZ=0
    g304: LineSegment [constr] StartX=-5 StartY=76 StartZ=0 EndX=-5 EndY=77 EndZ=0
    g305: LineSegment StartX=-5 StartY=77 StartZ=0 EndX=-3.00761 EndY=77.1743 EndZ=0
    g306: LineSegment StartX=-5 StartY=77 StartZ=0 EndX=-3.00761 EndY=76.8257 EndZ=0
    g307: LineSegment StartX=-3.00761 StartY=76.8257 StartZ=0 EndX=-3.00761 EndY=77.1743 EndZ=0
    g308: LineSegment [constr] StartX=-5 StartY=77 StartZ=0 EndX=-5 EndY=78 EndZ=0
    g309: LineSegment StartX=-5 StartY=78 StartZ=0 EndX=-3.00761 EndY=78.1743 EndZ=0
    g310: LineSegment StartX=-5 StartY=78 StartZ=0 EndX=-3.00761 EndY=77.8257 EndZ=0
    g311: LineSegment StartX=-3.00761 StartY=77.8257 StartZ=0 EndX=-3.00761 EndY=78.1743 EndZ=0
    g312: LineSegment [constr] StartX=-5 StartY=78 StartZ=0 EndX=-5 EndY=79 EndZ=0
    g313: LineSegment StartX=-5 StartY=79 StartZ=0 EndX=-3.00761 EndY=79.1743 EndZ=0
    g314: LineSegment StartX=-5 StartY=79 StartZ=0 EndX=-3.00761 EndY=78.8257 EndZ=0
    g315: LineSegment StartX=-3.00761 StartY=78.8257 StartZ=0 EndX=-3.00761 EndY=79.1743 EndZ=0
    g316: LineSegment [constr] StartX=-5 StartY=79 StartZ=0 EndX=-5 EndY=80 EndZ=0
    g317: LineSegment StartX=-5 StartY=80 StartZ=0 EndX=-3.00761 EndY=80.1743 EndZ=0
    g318: LineSegment StartX=-5 StartY=80 StartZ=0 EndX=-3.00761 EndY=79.8257 EndZ=0
    g319: LineSegment StartX=-3.00761 StartY=79.8257 StartZ=0 EndX=-3.00761 EndY=80.1743 EndZ=0
    g320: LineSegment [constr] StartX=-5 StartY=80 StartZ=0 EndX=-5 EndY=81 EndZ=0
    g321: LineSegment StartX=-5 StartY=81 StartZ=0 EndX=-3.00761 EndY=81.1743 EndZ=0
    g322: LineSegment StartX=-5 StartY=81 StartZ=0 EndX=-3.00761 EndY=80.8257 EndZ=0
    g323: LineSegment StartX=-3.00761 StartY=80.8257 StartZ=0 EndX=-3.00761 EndY=81.1743 EndZ=0
    g324: LineSegment [constr] StartX=-5 StartY=81 StartZ=0 EndX=-5 EndY=82 EndZ=0
    g325: LineSegment StartX=-5 StartY=82 StartZ=0 EndX=-3.00761 EndY=82.1743 EndZ=0
    g326: LineSegment StartX=-5 StartY=82 StartZ=0 EndX=-3.00761 EndY=81.8257 EndZ=0
    g327: LineSegment StartX=-3.00761 StartY=81.8257 StartZ=0 EndX=-3.00761 EndY=82.1743 EndZ=0
    g328: LineSegment [constr] StartX=-5 StartY=82 StartZ=0 EndX=-5 EndY=83 EndZ=0
    g329: LineSegment StartX=-5 StartY=83 StartZ=0 EndX=-3.00761 EndY=83.1743 EndZ=0
    g330: LineSegment StartX=-5 StartY=83 StartZ=0 EndX=-3.00761 EndY=82.8257 EndZ=0
    g331: LineSegment StartX=-3.00761 StartY=82.8257 StartZ=0 EndX=-3.00761 EndY=83.1743 EndZ=0
  constraints (339):
    c: Distance(g0) = 1
    c: Coincident(g0,g-4)
    c: PointOnObject(g0,g-3)
    c: Distance(g1) = 2
    c: Angle(g-1,g1) = 0.0872665
    c: Coincident(g1,g0)
    c: Distance(g2) = 2
    c: Angle(g-1,g2) = -0.0872665
    c: Coincident(g2,g0)
    c: Coincident(g3,g2)
    c: Coincident(g3,g1)
    c: Coincident(g5,g4)
    c: Coincident(g9,g8)
    c: Coincident(g13,g12)
    c: Coincident(g17,g16)
    c: Coincident(g21,g20)
    c: Coincident(g25,g24)
    c: Coincident(g29,g28)
    c: Coincident(g33,g32)
    c: Coincident(g37,g36)
    c: Coincident(g41,g40)
    c: Coincident(g45,g44)
    c: Coincident(g49,g48)
    c: Coincident(g53,g52)
    c: Coincident(g57,g56)
    c: Coincident(g61,g60)
    c: Coincident(g65,g64)
    c: Coincident(g69,g68)
    c: Coincident(g73,g72)
    c: Coincident(g77,g76)
    c: Coincident(g81,g80)
    c: Coincident(g85,g84)
    c: Coincident(g89,g88)
    c: Coincident(g93,g92)
    c: Coincident(g97,g96)
    c: Coincident(g101,g100)
    c: Coincident(g105,g104)
    c: Coincident(g109,g108)
    c: Coincident(g113,g112)
    c: Coincident(g117,g116)
    c: Coincident(g121,g120)
    c: Coincident(g125,g124)
    c: Coincident(g129,g128)
    c: Coincident(g133,g132)
    c: Coincident(g137,g136)
    c: Coincident(g141,g140)
    c: Coincident(g145,g144)
    c: Coincident(g149,g148)
    c: Coincident(g153,g152)
    c: Coincident(g157,g156)
    c: Coincident(g161,g160)
    c: Coincident(g165,g164)
    c: Coincident(g169,g168)
    c: Coincident(g173,g172)
    c: Coincident(g177,g176)
    c: Coincident(g181,g180)
    c: Coincident(g185,g184)
    c: Coincident(g189,g188)
    c: Coincident(g193,g192)
    c: Coincident(g197,g196)
    c: Coincident(g201,g200)
    c: Coincident(g205,g204)
    c: Coincident(g209,g208)
    c: Coincident(g213,g212)
    c: Coincident(g217,g216)
    c: Coincident(g221,g220)
    c: Coincident(g225,g224)
    c: Coincident(g229,g228)
    c: Coincident(g233,g232)
    c: Coincident(g237,g236)
    c: Coincident(g241,g240)
    c: Coincident(g245,g244)
    c: Coincident(g249,g248)
    c: Coincident(g253,g252)
    c: Coincident(g257,g256)
    c: Coincident(g261,g260)
    c: Coincident(g265,g264)
    c: Coincident(g269,g268)
    c: Coincident(g273,g272)
    c: Coincident(g277,g276)
    c: Coincident(g281,g280)
    c: Coincident(g285,g284)
    c: Coincident(g289,g288)
    c: Coincident(g293,g292)
    c: Coincident(g297,g296)
    c: Coincident(g301,g300)
    c: Coincident(g305,g304)
    c: Coincident(g309,g308)
    c: Coincident(g313,g312)
    c: Coincident(g317,g316)
    c: Coincident(g321,g320)
    c: Coincident(g325,g324)
    c: Coincident(g329,g328)
    c: Coincident(g6,g4)
    c: Coincident(g10,g8)
    c: Coincident(g14,g12)
    c: Coincident(g18,g16)
    c: Coincident(g22,g20)
    c: Coincident(g26,g24)
    c: Coincident(g30,g28)
    c: Coincident(g34,g32)
    c: Coincident(g38,g36)
    c: Coincident(g42,g40)
    c: Coincident(g46,g44)
    c: Coincident(g50,g48)
    c: Coincident(g54,g52)
    c: Coincident(g58,g56)
    c: Coincident(g62,g60)
    c: Coincident(g66,g64)
    c: Coincident(g70,g68)
    c: Coincident(g74,g72)
    c: Coincident(g78,g76)
    c: Coincident(g82,g80)
    c: Coincident(g86,g84)
    c: Coincident(g90,g88)
    c: Coincident(g94,g92)
    c: Coincident(g98,g96)
    c: Coincident(g102,g100)
    c: Coincident(g106,g104)
    c: Coincident(g110,g108)
    c: Coincident(g114,g112)
    c: Coincident(g118,g116)
    c: Coincident(g122,g120)
    c: Coincident(g126,g124)
    c: Coincident(g130,g128)
    c: Coincident(g134,g132)
    c: Coincident(g138,g136)
    c: Coincident(g142,g140)
    c: Coincident(g146,g144)
    c: Coincident(g150,g148)
    c: Coincident(g154,g152)
    c: Coincident(g158,g156)
    c: Coincident(g162,g160)
    c: Coincident(g166,g164)
    c: Coincident(g170,g168)
    c: Coincident(g174,g172)
    c: Coincident(g178,g176)
    c: Coincident(g182,g180)
    c: Coincident(g186,g184)
    c: Coincident(g190,g188)
    c: Coincident(g194,g192)
    c: Coincident(g198,g196)
    c: Coincident(g202,g200)
    c: Coincident(g206,g204)
    c: Coincident(g210,g208)
    c: Coincident(g214,g212)
    c: Coincident(g218,g216)
    c: Coincident(g222,g220)
    c: Coincident(g226,g224)
    c: Coincident(g230,g228)
    c: Coincident(g234,g232)
    c: Coincident(g238,g236)
    c: Coincident(g242,g240)
    c: Coincident(g246,g244)
    c: Coincident(g250,g248)
    c: Coincident(g254,g252)
    c: Coincident(g258,g256)
    c: Coincident(g262,g260)
    c: Coincident(g266,g264)
    c: Coincident(g270,g268)
    c: Coincident(g274,g272)
    c: Coincident(g278,g276)
    c: Coincident(g282,g280)
    c: Coincident(g286,g284)
    c: Coincident(g290,g288)
    c: Coincident(g294,g292)
    c: Coincident(g298,g296)
    c: Coincident(g302,g300)
    c: Coincident(g306,g304)
    c: Coincident(g310,g308)
    c: Coincident(g314,g312)
    c: Coincident(g318,g316)
    c: Coincident(g322,g320)
    c: Coincident(g326,g324)
    c: Coincident(g330,g328)
    c: Coincident(g7,g6)
    c: Coincident(g11,g10)
    c: Coincident(g15,g14)
    c: Coincident(g19,g18)
    c: Coincident(g23,g22)
    c: Coincident(g27,g26)
    c: Coincident(g31,g30)
    c: Coincident(g35,g34)
    c: Coincident(g39,g38)
    c: Coincident(g43,g42)
    c: Coincident(g47,g46)
    c: Coincident(g51,g50)
    c: Coincident(g55,g54)
    c: Coincident(g59,g58)
    c: Coincident(g63,g62)
    c: Coincident(g67,g66)
    c: Coincident(g71,g70)
    c: Coincident(g75,g74)
    c: Coincident(g79,g78)
    c: Coincident(g83,g82)
    c: Coincident(g87,g86)
    c: Coincident(g91,g90)
    c: Coincident(g95,g94)
    c: Coincident(g99,g98)
    c: Coincident(g103,g102)
    c: Coincident(g107,g106)
    c: Coincident(g111,g110)
    c: Coincident(g115,g114)
    c: Coincident(g119,g118)
    c: Coincident(g123,g122)
    c: Coincident(g127,g126)
    c: Coincident(g131,g130)
    c: Coincident(g135,g134)
    c: Coincident(g139,g138)
    c: Coincident(g143,g142)
    c: Coincident(g147,g146)
    c: Coincident(g151,g150)
    c: Coincident(g155,g154)
    c: Coincident(g159,g158)
    c: Coincident(g163,g162)
    c: Coincident(g167,g166)
    c: Coincident(g171,g170)
    c: Coincident(g175,g174)
    c: Coincident(g179,g178)
    c: Coincident(g183,g182)
    c: Coincident(g187,g186)
    c: Coincident(g191,g190)
    c: Coincident(g195,g194)
    c: Coincident(g199,g198)
    c: Coincident(g203,g202)
    c: Coincident(g207,g206)
    c: Coincident(g211,g210)
    c: Coincident(g215,g214)
    c: Coincident(g219,g218)
    c: Coincident(g223,g222)
    c: Coincident(g227,g226)
    c: Coincident(g231,g230)
    c: Coincident(g235,g234)
    c: Coincident(g239,g238)
    c: Coincident(g243,g242)
    c: Coincident(g247,g246)
    c: Coincident(g251,g250)
    c: Coincident(g255,g254)
    c: Coincident(g259,g258)
    c: Coincident(g263,g262)
    c: Coincident(g267,g266)
    c: Coincident(g271,g270)
    c: Coincident(g275,g274)
    c: Coincident(g279,g278)
    c: Coincident(g283,g282)
    c: Coincident(g287,g286)
    c: Coincident(g291,g290)
    c: Coincident(g295,g294)
    c: Coincident(g299,g298)
    c: Coincident(g303,g302)
    c: Coincident(g307,g306)
    c: Coincident(g311,g310)
    c: Coincident(g315,g314)
    c: Coincident(g319,g318)
    c: Coincident(g323,g322)
    c: Coincident(g327,g326)
    c: Coincident(g331,g330)
    c: Coincident(g7,g5)
    c: Coincident(g11,g9)
    c: Coincident(g15,g13)
    c: Coincident(g19,g17)
    c: Coincident(g23,g21)
    c: Coincident(g27,g25)
    c: Coincident(g31,g29)
    c: Coincident(g35,g33)
    c: Coincident(g39,g37)
    c: Coincident(g43,g41)
    c: Coincident(g47,g45)
    c: Coincident(g51,g49)
    c: Coincident(g55,g53)
    c: Coincident(g59,g57)
    c: Coincident(g63,g61)
    c: Coincident(g67,g65)
    c: Coincident(g71,g69)
    c: Coincident(g75,g73)
    c: Coincident(g79,g77)
    c: Coincident(g83,g81)
    c: Coincident(g87,g85)
    c: Coincident(g91,g89)
    c: Coincident(g95,g93)
    c: Coincident(g99,g97)
    c: Coincident(g103,g101)
    c: Coincident(g107,g105)
    c: Coincident(g111,g109)
    c: Coincident(g115,g113)
    c: Coincident(g119,g117)
    c: Coincident(g123,g121)
    c: Coincident(g127,g125)
    c: Coincident(g131,g129)
    c: Coincident(g135,g133)
    c: Coincident(g139,g137)
    c: Coincident(g143,g141)
    c: Coincident(g147,g145)
    c: Coincident(g151,g149)
    c: Coincident(g155,g153)
    c: Coincident(g159,g157)
    c: Coincident(g163,g161)
    c: Coincident(g167,g165)
    c: Coincident(g171,g169)
    c: Coincident(g175,g173)
    c: Coincident(g179,g177)
    c: Coincident(g183,g181)
    c: Coincident(g187,g185)
    c: Coincident(g191,g189)
    c: Coincident(g195,g193)
    c: Coincident(g199,g197)
    c: Coincident(g203,g201)
    c: Coincident(g207,g205)
    c: Coincident(g211,g209)
    c: Coincident(g215,g213)
    c: Coincident(g219,g217)
    c: Coincident(g223,g221)
    c: Coincident(g227,g225)
    c: Coincident(g231,g229)
    c: Coincident(g235,g233)
    c: Coincident(g239,g237)
    c: Coincident(g243,g241)
    c: Coincident(g247,g245)
    c: Coincident(g251,g249)
    c: Coincident(g255,g253)
    c: Coincident(g259,g257)
    c: Coincident(g263,g261)
    c: Coincident(g267,g265)
    c: Coincident(g271,g269)
    c: Coincident(g275,g273)
    c: Coincident(g279,g277)
    c: Coincident(g283,g281)
    c: Coincident(g287,g285)
    c: Coincident(g291,g289)
    c: Coincident(g295,g293)
    c: Coincident(g299,g297)
    c: Coincident(g303,g301)
    c: Coincident(g307,g305)
    c: Coincident(g311,g309)
    c: Coincident(g315,g313)
    c: Coincident(g319,g317)
    c: Coincident(g323,g321)
    c: Coincident(g327,g325)
    c: Coincident(g331,g329)
FEATURE [PartDesign::Pocket] Pocket016
  BaseFeature = -> Fillet005
  Direction = (1,0,2e-16)
  Length = 0.5
  Length2 = 5
  Placement = pos=(0,0,0) rot=(1,0,0;1.5708rad)
  Profile = -> Sketch038
  ReferenceAxis = -> Sketch038 [N_Axis]
  Refine = true
  Suppressed = false
  Type = 0
FEATURE [Sketcher::SketchObject] Sketch039
  ArcFitTolerance = 1e-06
  AttachmentSupport = -> [Pocket015]
  ExternalGeometry = -> [Pocket015]
  FullyConstrained = false
  MakeInternals = false
  MapMode = 5
  Placement = pos=(-1.2282e-09,-84,2e-15) rot=(-0.707107,0,0.707107;3.14159rad)
  sketch-geometry (68):
    g0: LineSegment [constr] StartX=-5.35355 StartY=-84 StartZ=0 EndX=-5.35355 EndY=-75 EndZ=0
    g1: LineSegment StartX=-5.35355 StartY=-75 StartZ=0 EndX=-7.34594 EndY=-74.8257 EndZ=0
    g2: LineSegment StartX=-5.35355 StartY=-75 StartZ=0 EndX=-7.34594 EndY=-75.1743 EndZ=0
    g3: LineSegment StartX=-7.34594 StartY=-75.1743 StartZ=0 EndX=-7.34594 EndY=-74.8257 EndZ=0
    g4: LineSegment StartX=-5.35355 StartY=-75.9 StartZ=0 EndX=-7.34594 EndY=-75.7257 EndZ=0
    g5: LineSegment StartX=-5.35355 StartY=-75.9 StartZ=0 EndX=-7.34594 EndY=-76.0743 EndZ=0
    g6: LineSegment StartX=-7.34594 StartY=-76.0743 StartZ=0 EndX=-7.34594 EndY=-75.7257 EndZ=0
    g7: LineSegment StartX=-5.35355 StartY=-76.8 StartZ=0 EndX=-7.34594 EndY=-76.6257 EndZ=0
    g8: LineSegment StartX=-5.35355 StartY=-76.8 StartZ=0 EndX=-7.34594 EndY=-76.9743 EndZ=0
    g9: LineSegment StartX=-7.34594 StartY=-76.9743 StartZ=0 EndX=-7.34594 EndY=-76.6257 EndZ=0
    g10: LineSegment StartX=-5.35355 StartY=-77.7 StartZ=0 EndX=-7.34594 EndY=-77.5257 EndZ=0
    g11: LineSegment StartX=-5.35355 StartY=-77.7 StartZ=0 EndX=-7.34594 EndY=-77.8743 EndZ=0
    g12: LineSegment StartX=-7.34594 StartY=-77.8743 StartZ=0 EndX=-7.34594 EndY=-77.5257 EndZ=0
    g13: LineSegment StartX=-5.35355 StartY=-78.6 StartZ=0 EndX=-7.34594 EndY=-78.4257 EndZ=0
    g14: LineSegment StartX=-5.35355 StartY=-78.6 StartZ=0 EndX=-7.34594 EndY=-78.7743 EndZ=0
    g15: LineSegment StartX=-7.34594 StartY=-78.7743 StartZ=0 EndX=-7.34594 EndY=-78.4257 EndZ=0
    g16: LineSegment StartX=-5.35355 StartY=-79.5 StartZ=0 EndX=-7.34594 EndY=-79.3257 EndZ=0
    g17: LineSegment StartX=-5.35355 StartY=-79.5 StartZ=0 EndX=-7.34594 EndY=-79.6743 EndZ=0
    g18: LineSegment StartX=-7.34594 StartY=-79.6743 StartZ=0 EndX=-7.34594 EndY=-79.3257 EndZ=0
    g19: LineSegment StartX=-5.35355 StartY=-80.4 StartZ=0 EndX=-7.34594 EndY=-80.2257 EndZ=0
    g20: LineSegment StartX=-5.35355 StartY=-80.4 StartZ=0 EndX=-7.34594 EndY=-80.5743 EndZ=0
    g21: LineSegment StartX=-7.34594 StartY=-80.5743 StartZ=0 EndX=-7.34594 EndY=-80.2257 EndZ=0
    g22: LineSegment StartX=-5.35355 StartY=-81.3 StartZ=0 EndX=-7.34594 EndY=-81.1257 EndZ=0
    g23: LineSegment StartX=-5.35355 StartY=-81.3 StartZ=0 EndX=-7.34594 EndY=-81.4743 EndZ=0
    g24: LineSegment StartX=-7.34594 StartY=-81.4743 StartZ=0 EndX=-7.34594 EndY=-81.1257 EndZ=0
    g25: LineSegment StartX=-5.35355 StartY=-82.2 StartZ=0 EndX=-7.34594 EndY=-82.0257 EndZ=0
    g26: LineSegment StartX=-5.35355 StartY=-82.2 StartZ=0 EndX=-7.34594 EndY=-82.3743 EndZ=0
    g27: LineSegment StartX=-7.34594 StartY=-82.3743 StartZ=0 EndX=-7.34594 EndY=-82.0257 EndZ=0
    g28: LineSegment StartX=-5.35355 StartY=-83.1 StartZ=0 EndX=-7.34594 EndY=-82.9257 EndZ=0
    g29: LineSegment StartX=-5.35355 StartY=-83.1 StartZ=0 EndX=-7.34594 EndY=-83.2743 EndZ=0
    g30: LineSegment StartX=-7.34594 StartY=-83.2743 StartZ=0 EndX=-7.34594 EndY=-82.9257 EndZ=0
    g31: LineSegment [constr] StartX=-5.35355 StartY=0 StartZ=0 EndX=-5.35355 EndY=-9 EndZ=0
    g32: LineSegment StartX=-5.35355 StartY=-9 StartZ=0 EndX=-7.34594 EndY=-9.17431 EndZ=0
    g33: LineSegment StartX=-5.35355 StartY=-9 StartZ=0 EndX=-7.34594 EndY=-8.82569 EndZ=0
    g34: LineSegment StartX=-7.34594 StartY=-8.82569 StartZ=0 EndX=-7.34594 EndY=-9.17431 EndZ=0
    g35: LineSegment StartX=-5.35355 StartY=-8.1 StartZ=0 EndX=-7.34594 EndY=-8.27431 EndZ=0
    g36: LineSegment StartX=-5.35355 StartY=-8.1 StartZ=0 EndX=-7.34594 EndY=-7.92569 EndZ=0
    g37: LineSegment StartX=-7.34594 StartY=-7.92569 StartZ=0 EndX=-7.34594 EndY=-8.27431 EndZ=0
    g38: LineSegment StartX=-5.35355 StartY=-7.2 StartZ=0 EndX=-7.34594 EndY=-7.37431 EndZ=0
    g39: LineSegment StartX=-5.35355 StartY=-7.2 StartZ=0 EndX=-7.34594 EndY=-7.02569 EndZ=0
    g40: LineSegment StartX=-7.34594 StartY=-7.02569 StartZ=0 EndX=-7.34594 EndY=-7.37431 EndZ=0
    g41: LineSegment StartX=-5.35355 StartY=-6.3 StartZ=0 EndX=-7.34594 EndY=-6.47431 EndZ=0
    g42: LineSegment StartX=-5.35355 StartY=-6.3 StartZ=0 EndX=-7.34594 EndY=-6.12569 EndZ=0
    g43: LineSegment StartX=-7.34594 StartY=-6.12569 StartZ=0 EndX=-7.34594 EndY=-6.47431 EndZ=0
    g44: LineSegment StartX=-5.35355 StartY=-5.4 StartZ=0 EndX=-7.34594 EndY=-5.57431 EndZ=0
    g45: LineSegment StartX=-5.35355 StartY=-5.4 StartZ=0 EndX=-7.34594 EndY=-5.22569 EndZ=0
    g46: LineSegment StartX=-7.34594 StartY=-5.22569 StartZ=0 EndX=-7.34594 EndY=-5.57431 EndZ=0
    g47: LineSegment StartX=-5.35355 StartY=-4.5 StartZ=0 EndX=-7.34594 EndY=-4.67431 EndZ=0
    g48: LineSegment StartX=-5.35355 StartY=-4.5 StartZ=0 EndX=-7.34594 EndY=-4.32569 EndZ=0
    g49: LineSegment StartX=-7.34594 StartY=-4.32569 StartZ=0 EndX=-7.34594 EndY=-4.67431 EndZ=0
    g50: LineSegment StartX=-5.35355 StartY=-3.6 StartZ=0 EndX=-7.34594 EndY=-3.77431 EndZ=0
    g51: LineSegment StartX=-5.35355 StartY=-3.6 StartZ=0 EndX=-7.34594 EndY=-3.42569 EndZ=0
    g52: LineSegment StartX=-7.34594 StartY=-3.42569 StartZ=0 EndX=-7.34594 EndY=-3.77431 EndZ=0
    g53: LineSegment StartX=-5.35355 StartY=-2.7 StartZ=0 EndX=-7.34594 EndY=-2.87431 EndZ=0
    g54: LineSegment StartX=-5.35355 StartY=-2.7 StartZ=0 EndX=-7.34594 EndY=-2.52569 EndZ=0
    g55: LineSegment StartX=-7.34594 StartY=-2.52569 StartZ=0 EndX=-7.34594 EndY=-2.87431 EndZ=0
    g56: LineSegment StartX=-5.35355 StartY=-1.8 StartZ=0 EndX=-7.34594 EndY=-1.97431 EndZ=0
    g57: LineSegment StartX=-5.35355 StartY=-1.8 StartZ=0 EndX=-7.34594 EndY=-1.62569 EndZ=0
    g58: LineSegment StartX=-7.34594 StartY=-1.62569 StartZ=0 EndX=-7.34594 EndY=-1.97431 EndZ=0
    g59: LineSegment StartX=-5.35355 StartY=-0.9 StartZ=0 EndX=-7.34594 EndY=-1.07431 EndZ=0
    g60: LineSegment StartX=-5.35355 StartY=-0.9 StartZ=0 EndX=-7.34594 EndY=-0.725689 EndZ=0
    g61: LineSegment StartX=-7.34594 StartY=-0.725689 StartZ=0 EndX=-7.34594 EndY=-1.07431 EndZ=0
    g62: LineSegment StartX=-5.35355 StartY=-84 StartZ=0 EndX=-7.34594 EndY=-83.8257 EndZ=0
    g63: LineSegment StartX=-7.34594 StartY=-83.8257 StartZ=0 EndX=-7.34594 EndY=-84 EndZ=0
    g64: LineSegment StartX=-7.34594 StartY=-84 StartZ=0 EndX=-5.35355 EndY=-84 EndZ=0
    g65: LineSegment StartX=-5.35355 StartY=0 StartZ=0 EndX=-7.34594 EndY=-0.174312 EndZ=0
    g66: LineSegment StartX=-7.34594 StartY=-0.174312 StartZ=0 EndX=-7.34594 EndY=0 EndZ=0
    g67: LineSegment StartX=-7.34594 StartY=0 StartZ=0 EndX=-5.35355 EndY=0 EndZ=0
  constraints (74):
    c: Distance(g0) = 9
    c: Coincident(g0,g-4)
    c: PointOnObject(g0,g-3)
    c: Distance(g1) = 2
    c: Angle(g-1,g1) = 3.05433
    c: Coincident(g1,g0)
    c: Distance(g2) = 2
    c: Angle(g-1,g2) = -3.05433
    c: Coincident(g2,g0)
    c: Coincident(g3,g2)
    c: Coincident(g3,g1)
    c: Coincident(g6,g5)
    c: Coincident(g9,g8)
    c: Coincident(g12,g11)
    c: Coincident(g15,g14)
    c: Coincident(g18,g17)
    c: Coincident(g21,g20)
    c: Coincident(g24,g23)
    c: Coincident(g27,g26)
    c: Coincident(g30,g29)
    c: Coincident(g6,g4)
    c: Coincident(g9,g7)
    c: Coincident(g12,g10)
    c: Coincident(g15,g13)
    c: Coincident(g18,g16)
    c: Coincident(g21,g19)
    c: Coincident(g24,g22)
    c: Coincident(g27,g25)
    c: Coincident(g30,g28)
    c: Distance(g31) = 9
    c: Coincident(g31,g-3)
    c: PointOnObject(g31,g-3)
    c: Distance(g32) = 2
    c: Angle(g-1,g32) = -3.05433
    c: Coincident(g32,g31)
    c: Distance(g33) = 2
    c: Angle(g-1,g33) = 3.05433
    c: Coincident(g33,g31)
    c: Coincident(g34,g33)
    c: Coincident(g34,g32)
    c: Coincident(g37,g36)
    c: Coincident(g40,g39)
    c: Coincident(g43,g42)
    c: Coincident(g46,g45)
    c: Coincident(g49,g48)
    c: Coincident(g52,g51)
    c: Coincident(g55,g54)
    c: Coincident(g58,g57)
    c: Coincident(g61,g60)
    c: Coincident(g37,g35)
    c: Coincident(g40,g38)
    c: Coincident(g43,g41)
    c: Coincident(g46,g44)
    c: Coincident(g49,g47)
    c: Coincident(g52,g50)
    c: Coincident(g55,g53)
    c: Coincident(g58,g56)
    c: Coincident(g61,g59)
    c: Distance(g62) = 2
    c: Angle(g-1,g62) = 3.05433
    c: Coincident(g62,g0)
    c: Coincident(g63,g62)
    c: PointOnObject(g63,g-4)
    c: Vertical(g63)
    c: Coincident(g64,g63)
    c: Coincident(g64,g0)
    c: Distance(g65) = 2
    c: Angle(g-1,g65) = -3.05433
    c: Coincident(g65,g31)
    c: Coincident(g66,g65)
    c: Vertical(g66)
    c: Coincident(g67,g66)
    c: Coincident(g67,g31)
    c: Horizontal(g67)
FEATURE [PartDesign::Pocket] Pocket017
  BaseFeature = -> Pocket015
  Direction = (1,0,-2.14311e-10)
  Length = 0.5
  Length2 = 5
  Placement = pos=(0,-84,2e-15) rot=(1,0,0;1.5708rad)
  Profile = -> Sketch039
  ReferenceAxis = -> Sketch039 [N_Axis]
  Refine = true
  Suppressed = false
  Type = 0
FEATURE [Sketcher::SketchObject] Sketch040
  ArcFitTolerance = 1e-06
  AttachmentSupport = -> [Hole002]
  ExternalGeometry = -> [Hole002]
  FullyConstrained = true
  MakeInternals = false
  MapMode = 5
  Placement = pos=(3.7335e-08,0,9.85355) rot=(1,0,0;3.14159rad)
  sketch-geometry (4):
    g0: LineSegment StartX=38.7465 StartY=46.75 StartZ=0 EndX=38.7465 EndY=37.25 EndZ=0
    g1: LineSegment StartX=38.7465 StartY=37.25 StartZ=0 EndX=45.2465 EndY=37.25 EndZ=0
    g2: LineSegment StartX=45.2465 StartY=37.25 StartZ=0 EndX=45.2465 EndY=46.75 EndZ=0
    g3: LineSegment StartX=45.2465 StartY=46.75 StartZ=0 EndX=38.7465 EndY=46.75 EndZ=0
  constraints (10):
    c: Coincident(g0,g1)
    c: Coincident(g1,g2)
    c: Coincident(g2,g3)
    c: Coincident(g3,g0)
    c: Vertical(g0)
    c: Vertical(g2)
    c: Horizontal(g1)
    c: Horizontal(g3)
    c: Coincident(g0,g-5)
    c: Coincident(g1,g-6)
FEATURE [PartDesign::Pad] Pad019
  BaseFeature = -> Hole002
  Direction = (-3.78899e-09,0,-1)
  Length = 4.65
  Length2 = 10
  Profile = -> Sketch040
  ReferenceAxis = -> Sketch040 [N_Axis]
  Refine = true
  Suppressed = false
  Type = 0
FEATURE [PartDesign::Chamfer] Chamfer015
  Angle = 45
  Base = -> Pad019 [Edge6]
  BaseFeature = -> Pad019
  ChamferType = 0
  FlipDirection = false
  Refine = true
  Size = 4
  Size2 = 1
  SupportTransform = false
  Suppressed = false
  UseAllEdges = false
FEATURE [PartDesign::Chamfer] Chamfer016
  Angle = 45
  Base = -> Chamfer015 [Edge47]
  BaseFeature = -> Chamfer015
  ChamferType = 0
  FlipDirection = false
  Refine = true
  Size = 4
  Size2 = 1
  SupportTransform = false
  Suppressed = false
  UseAllEdges = false
FEATURE [Sketcher::SketchObject] Sketch041
  ArcFitTolerance = 1e-06
  AttachmentSupport = -> [Chamfer016]
  ExternalGeometry = -> [Chamfer016]
  FullyConstrained = true
  MakeInternals = false
  MapMode = 5
  Placement = pos=(0,-37.25,0) rot=(0,0.707107,0.707107;3.14159rad)
  sketch-geometry (4):
    g0: LineSegment StartX=-48.2465 StartY=20.8536 StartZ=0 EndX=-48.2465 EndY=6.85355 EndZ=0
    g1: LineSegment StartX=-48.2465 StartY=6.85355 StartZ=0 EndX=-46.2465 EndY=6.85355 EndZ=0
    g2: LineSegment StartX=-46.2465 StartY=6.85355 StartZ=0 EndX=-46.2465 EndY=20.8536 EndZ=0
    g3: LineSegment StartX=-46.2465 StartY=20.8536 StartZ=0 EndX=-48.2465 EndY=20.8536 EndZ=0
  constraints (11):
    c: Coincident(g0,g1)
    c: Coincident(g1,g2)
    c: Coincident(g2,g3)
    c: Coincident(g3,g0)
    c: Vertical(g0)
    c: Vertical(g2)
    c: Horizontal(g1)
    c: Horizontal(g3)
    c: Distance(g0,g2) = 2
    c: Distance(g1,g3) = 14
    c: Coincident(g0,g-11)
FEATURE [PartDesign::Pocket] Pocket018
  BaseFeature = -> Chamfer016
  Direction = (0,-1,2e-16)
  Length = 10
  Length2 = 5
  Profile = -> Sketch041
  ReferenceAxis = -> Sketch041 [N_Axis]
  Refine = true
  Suppressed = false
  Type = 0
FEATURE [Sketcher::SketchObject] Sketch043
  ArcFitTolerance = 1e-06
  AttachmentSupport = -> [Pocket018]
  ExternalGeometry = -> [Pocket018]
  FullyConstrained = true
  MakeInternals = false
  MapMode = 5
  Placement = pos=(0,-37.25,0) rot=(0,0.707107,0.707107;3.14159rad)
  sketch-geometry (4):
    g0: LineSegment StartX=-35.7465 StartY=20.8536 StartZ=0 EndX=-37.7465 EndY=20.8536 EndZ=0
    g1: LineSegment StartX=-37.7465 StartY=20.8536 StartZ=0 EndX=-37.7465 EndY=7.85355 EndZ=0
    g2: LineSegment StartX=-37.7465 StartY=7.85355 StartZ=0 EndX=-35.7465 EndY=7.85355 EndZ=0
    g3: LineSegment StartX=-35.7465 StartY=7.85355 StartZ=0 EndX=-35.7465 EndY=20.8536 EndZ=0
  constraints (11):
    c: Coincident(g0,g1)
    c: Coincident(g1,g2)
    c: Coincident(g2,g3)
    c: Coincident(g3,g0)
    c: Horizontal(g0)
    c: Horizontal(g2)
    c: Vertical(g1)
    c: Vertical(g3)
    c: Distance(g1,g3) = 2
    c: Distance(g0,g2) = 13
    c: Coincident(g0,g-4)
FEATURE [PartDesign::Pocket] Pocket019
  BaseFeature = -> Pocket018
  Direction = (0,-1,2e-16)
  Length = 10
  Length2 = 5
  Profile = -> Sketch043
  ReferenceAxis = -> Sketch043 [N_Axis]
  Refine = true
  Suppressed = false
  Type = 0
FEATURE [Sketcher::SketchObject] Sketch044
  ArcFitTolerance = 1e-06
  AttachmentSupport = -> [Pocket019]
  ExternalGeometry = -> [Pocket019]
  FullyConstrained = true
  MakeInternals = false
  MapMode = 5
  Placement = pos=(0,-37.25,0) rot=(0,0.707107,0.707107;3.14159rad)
  sketch-geometry (4):
    g0: LineSegment StartX=-46.2465 StartY=20.8536 StartZ=0 EndX=-54.2465 EndY=20.8536 EndZ=0
    g1: LineSegment StartX=-54.2465 StartY=20.8536 StartZ=0 EndX=-54.2465 EndY=16.8536 EndZ=0
    g2: LineSegment StartX=-46.2465 StartY=8.26777 StartZ=0 EndX=-46.2465 EndY=20.8536 EndZ=0
    g3: LineSegment StartX=-54.2465 StartY=16.8536 StartZ=0 EndX=-46.2465 EndY=8.26777 EndZ=0
  constraints (10):
    c: Distance(g0) = 8
    c: Coincident(g0,g-4)
    c: Horizontal(g0)
    c: Distance(g1) = 4
    c: Coincident(g1,g0)
    c: Vertical(g1)
    c: Coincident(g2,g0)
    c: Coincident(g3,g1)
    c: Coincident(g3,g2)
    c: Coincident(g-4,g2)
FEATURE [PartDesign::Pad] Pad020
  BaseFeature = -> Pocket019
  Direction = (0,1,-2e-16)
  Length = 9.5
  Length2 = 10
  Profile = -> Sketch044
  ReferenceAxis = -> Sketch044 [N_Axis]
  Refine = true
  Reversed = true
  Suppressed = false
  Type = 0
FEATURE [Sketcher::SketchObject] Sketch045
  ArcFitTolerance = 1e-06
  AttachmentSupport = -> [Pad020]
  ExternalGeometry = -> [Pad020]
  FullyConstrained = true
  MakeInternals = false
  MapMode = 5
  Placement = pos=(2.2e-14,-37.25,1.23e-14) rot=(0,0.707107,0.707107;3.14159rad)
  sketch-geometry (4):
    g0: LineSegment StartX=-37.7465 StartY=20.8536 StartZ=0 EndX=-29.7465 EndY=20.8536 EndZ=0
    g1: LineSegment StartX=-29.7465 StartY=20.8536 StartZ=0 EndX=-29.7465 EndY=16.8536 EndZ=0
    g2: LineSegment StartX=-29.7465 StartY=16.8536 StartZ=0 EndX=-37.7465 EndY=8.26777 EndZ=0
    g3: LineSegment StartX=-37.7465 StartY=8.26777 StartZ=0 EndX=-37.7465 EndY=20.8536 EndZ=0
  constraints (10):
    c: Distance(g0) = 8
    c: Coincident(g0,g-4)
    c: Horizontal(g0)
    c: Distance(g1) = 4
    c: Coincident(g1,g0)
    c: Vertical(g1)
    c: Coincident(g2,g1)
    c: Coincident(g2,g-6)
    c: Coincident(g3,g2)
    c: Coincident(g3,g0)
FEATURE [PartDesign::Pad] Pad021
  BaseFeature = -> Pad020
  Direction = (0,1,-2e-16)
  Length = 9.5
  Length2 = 10
  Profile = -> Sketch045
  ReferenceAxis = -> Sketch045 [N_Axis]
  Refine = true
  Reversed = true
  Suppressed = false
  Type = 0
FEATURE [Sketcher::SketchObject] Sketch046
  ArcFitTolerance = 1e-06
  AttachmentSupport = -> [Pad021]
  ExternalGeometry = -> [Pad021]
  FullyConstrained = true
  MakeInternals = false
  MapMode = 5
  Placement = pos=(8.12e-14,-37.25,0) rot=(0,0.707107,0.707107;3.14159rad)
  sketch-geometry (2):
    g0: GeomPoint [constr] X=-54.2465 Y=18.8536 Z=0
    g1: Circle CenterX=-54.2465 CenterY=18.8536 CenterZ=0 NormalX=0 NormalY=0 NormalZ=1 AngleXU=0 Radius=1
  constraints (3):
    c: Symmetric(g-3,g-3,g0)
    c: Diameter(g1) = 2
    c: Coincident(g1,g0)
FEATURE [PartDesign::Pocket] Pocket020
  BaseFeature = -> Pad021
  Direction = (2.2e-15,-1,2e-16)
  Length = 10
  Length2 = 5
  Profile = -> Sketch046
  ReferenceAxis = -> Sketch046 [N_Axis]
  Refine = true
  Suppressed = false
  Type = 0
FEATURE [Sketcher::SketchObject] Sketch047
  ArcFitTolerance = 1e-06
  AttachmentSupport = -> [Pocket020]
  ExternalGeometry = -> [Pocket020]
  FullyConstrained = true
  MakeInternals = false
  MapMode = 5
  Placement = pos=(8.12e-14,-37.25,0) rot=(0,0.707107,0.707107;3.14159rad)
  sketch-geometry (2):
    g0: GeomPoint X=-29.7465 Y=18.8536 Z=0
    g1: Circle CenterX=-29.7465 CenterY=18.8536 CenterZ=0 NormalX=0 NormalY=0 NormalZ=1 AngleXU=0 Radius=1
  constraints (3):
    c: Symmetric(g-3,g-3,g0)
    c: Diameter(g1) = 2
    c: Coincident(g1,g0)
FEATURE [PartDesign::Pocket] Pocket021
  BaseFeature = -> Pocket020
  Direction = (2.2e-15,-1,2e-16)
  Length = 11
  Length2 = 5
  Profile = -> Sketch047
  ReferenceAxis = -> Sketch047 [N_Axis]
  Refine = true
  Suppressed = false
  Type = 0
FEATURE [Sketcher::SketchObject] Sketch048
  ArcFitTolerance = 1e-06
  AttachmentSupport = -> [Pocket021]
  ExternalGeometry = -> [Pocket021]
  FullyConstrained = true
  MakeInternals = false
  MapMode = 5
  Placement = pos=(6.7647e-08,0,17.8536) rot=(0,0,1;0rad)
  sketch-geometry (1):
    g0: Circle CenterX=41.9965 CenterY=-42 CenterZ=0 NormalX=0 NormalY=0 NormalZ=1 AngleXU=0 Radius=1.35
  constraints (2):
    c: Coincident(g0,g-3)
    c: Equal(g0,g-3)
FEATURE [PartDesign::Pad] Pad022
  BaseFeature = -> Pocket021
  Direction = (3.78899e-09,0,1)
  Length = 3
  Length2 = 10
  Profile = -> Sketch048
  ReferenceAxis = -> Sketch048 [N_Axis]
  Refine = true
  Suppressed = false
  Type = 0
FEATURE [Sketcher::SketchObject] Sketch049
  ArcFitTolerance = 1e-06
  AttachmentSupport = -> [Pad022]
  ExternalGeometry = -> [Pad022]
  FullyConstrained = true
  MakeInternals = false
  MapMode = 5
  Placement = pos=(3.93837e-08,0,20.8536) rot=(0,0,1;0rad)
  sketch-geometry (8):
    g0: GeomPoint X=33.7465 Y=-37.25 Z=0
    g1: GeomPoint X=33.7465 Y=-46.75 Z=0
    g2: GeomPoint X=50.2465 Y=-46.75 Z=0
    g3: GeomPoint X=50.2465 Y=-37.25 Z=0
    g4: LineSegment [constr] StartX=33.7465 StartY=-37.25 StartZ=0 EndX=33.7465 EndY=-46.75 EndZ=0
    g5: LineSegment [constr] StartX=50.2465 StartY=-37.25 StartZ=0 EndX=50.2465 EndY=-46.75 EndZ=0
    g6: Circle CenterX=33.7465 CenterY=-42 CenterZ=0 NormalX=0 NormalY=0 NormalZ=1 AngleXU=0 Radius=1.35
    g7: Circle CenterX=50.2465 CenterY=-42 CenterZ=0 NormalX=0 NormalY=0 NormalZ=1 AngleXU=0 Radius=1.35
  constraints (12):
    c: Symmetric(g-3,g-3,g0)
    c: Symmetric(g-6,g-6,g1)
    c: Symmetric(g-5,g-5,g2)
    c: Symmetric(g-4,g-4,g3)
    c: Coincident(g4,g0)
    c: Coincident(g4,g1)
    c: Coincident(g5,g3)
    c: Coincident(g5,g2)
    c: Diameter(g6) = 2.7
    c: Symmetric(g4,g4,g6)
    c: Diameter(g7) = 2.7
    c: Symmetric(g5,g5,g7)
FEATURE [PartDesign::Pocket] Pocket022
  BaseFeature = -> Pad022
  Direction = (-1.88858e-09,0,-1)
  Length = 13
  Length2 = 5
  Profile = -> Sketch049
  ReferenceAxis = -> Sketch049 [N_Axis]
  Refine = true
  Suppressed = false
  Type = 0
FEATURE [Sketcher::SketchObject] Sketch050
  ArcFitTolerance = 1e-06
  AttachmentSupport = -> [Pocket017]
  FullyConstrained = true
  MakeInternals = false
  MapMode = 5
  Placement = pos=(7.71195e-08,-84,20.3536) rot=(1,0,0;3.14159rad)
  sketch-geometry (10):
    g0: LineSegment [constr] StartX=35.4965 StartY=-37 StartZ=0 EndX=29.6465 EndY=-37 EndZ=0
    g1: LineSegment [constr] StartX=48.4965 StartY=-37 StartZ=0 EndX=54.3465 EndY=-37 EndZ=0
    g2: LineSegment StartX=29.6465 StartY=-37 StartZ=0 EndX=29.6465 EndY=-47 EndZ=0
    g3: LineSegment StartX=29.6465 StartY=-47 StartZ=0 EndX=35.4965 EndY=-47 EndZ=0
    g4: LineSegment StartX=35.4965 StartY=-47 StartZ=0 EndX=35.4965 EndY=-37 EndZ=0
    g5: LineSegment StartX=35.4965 StartY=-37 StartZ=0 EndX=29.6465 EndY=-37 EndZ=0
    g6: LineSegment StartX=54.3465 StartY=-37 StartZ=0 EndX=48.4965 EndY=-37 EndZ=0
    g7: LineSegment StartX=48.4965 StartY=-37 StartZ=0 EndX=48.4965 EndY=-47 EndZ=0
    g8: LineSegment StartX=48.4965 StartY=-47 StartZ=0 EndX=54.3465 EndY=-47 EndZ=0
    g9: LineSegment StartX=54.3465 StartY=-47 StartZ=0 EndX=54.3465 EndY=-37 EndZ=0
  constraints (26):
    c: Distance(g0) = 5.85
    c: Coincident(g0,g-4)
    c: Horizontal(g0)
    c: Distance(g1) = 5.85
    c: Coincident(g1,g-5)
    c: Horizontal(g1)
    c: Coincident(g2,g3)
    c: Coincident(g3,g4)
    c: Coincident(g4,g5)
    c: Coincident(g5,g2)
    c: Vertical(g2)
    c: Vertical(g4)
    c: Horizontal(g3)
    c: Horizontal(g5)
    c: Coincident(g2,g0)
    c: Coincident(g3,g-6)
    c: Coincident(g6,g7)
    c: Coincident(g7,g8)
    c: Coincident(g8,g9)
    c: Coincident(g9,g6)
    c: Horizontal(g6)
    c: Horizontal(g8)
    c: Vertical(g7)
    c: Vertical(g9)
    c: Coincident(g6,g1)
    c: Coincident(g7,g-6)
FEATURE [PartDesign::Pocket] Pocket023
  BaseFeature = -> Pocket017
  Direction = (3.78899e-09,1.1e-15,1)
  Length = 0.5
  Length2 = 5
  Placement = pos=(0,-84,2e-15) rot=(1,0,0;1.5708rad)
  Profile = -> Sketch050
  ReferenceAxis = -> Sketch050 [N_Axis]
  Refine = true
  Suppressed = false
  Type = 0
FEATURE [Sketcher::SketchObject] Sketch051
  ArcFitTolerance = 1e-06
  AttachmentSupport = -> [Pocket023]
  ExternalGeometry = -> [Pocket023]
  FullyConstrained = true
  MakeInternals = false
  MapMode = 5
  Placement = pos=(7.9014e-08,-84,20.8536) rot=(1,0,0;3.14159rad)
  sketch-geometry (4):
    g0: LineSegment [constr] StartX=41.9965 StartY=-42 StartZ=0 EndX=50.2465 EndY=-42 EndZ=0
    g1: LineSegment [constr] StartX=41.9965 StartY=-42 StartZ=0 EndX=33.7465 EndY=-42 EndZ=0
    g2: Circle CenterX=33.7465 CenterY=-42 CenterZ=0 NormalX=0 NormalY=0 NormalZ=1 AngleXU=0 Radius=1.5
    g3: Circle CenterX=50.2465 CenterY=-42 CenterZ=0 NormalX=0 NormalY=0 NormalZ=1 AngleXU=0 Radius=1.5
  constraints (10):
    c: Distance(g0) = 8.25
    c: Coincident(g0,g-3)
    c: Horizontal(g0)
    c: Distance(g1) = 8.25
    c: Coincident(g1,g0)
    c: Horizontal(g1)
    c: Diameter(g2) = 3
    c: Coincident(g2,g1)
    c: Diameter(g3) = 3
    c: Coincident(g3,g0)
FEATURE [PartDesign::Pocket] Pocket024
  BaseFeature = -> Pocket023
  Direction = (3.78899e-09,1.2e-15,1)
  Length = 11
  Length2 = 5
  Placement = pos=(0,-84,2e-15) rot=(1,0,0;1.5708rad)
  Profile = -> Sketch051
  ReferenceAxis = -> Sketch051 [N_Axis]
  Refine = true
  Suppressed = false
  Type = 0
FEATURE [Sketcher::SketchObject] Sketch052
  ArcFitTolerance = 1e-06
  AttachmentSupport = -> [Pocket024]
  ExternalGeometry = -> [Pocket024]
  FullyConstrained = true
  MakeInternals = false
  MapMode = 5
  Placement = pos=(6.55296e-08,-84,23.3536) rot=(0,0,1;3.14159rad)
  sketch-geometry (2):
    g0: Circle CenterX=-41.9965 CenterY=-42 CenterZ=0 NormalX=0 NormalY=0 NormalZ=1 AngleXU=0 Radius=1.55
    g1: Circle CenterX=-41.9965 CenterY=-42 CenterZ=0 NormalX=0 NormalY=0 NormalZ=1 AngleXU=0 Radius=3
  constraints (4):
    c: Diameter(g0) = 3.1
    c: Coincident(g0,g-4)
    c: Diameter(g1) = 6
    c: Coincident(g1,g0)
FEATURE [PartDesign::Pad] Pad023
  BaseFeature = -> Pocket024
  Direction = (2.80598e-09,0,1)
  Length = 4
  Length2 = 10
  Placement = pos=(0,-84,2e-15) rot=(1,0,0;1.5708rad)
  Profile = -> Sketch052
  ReferenceAxis = -> Sketch052 [N_Axis]
  Refine = true
  Suppressed = false
  Type = 0
FEATURE [Sketcher::SketchObject] Sketch053
  ArcFitTolerance = 1e-06
  AttachmentSupport = -> [Pad023]
  ExternalGeometry = -> [Pad023]
  FullyConstrained = true
  MakeInternals = false
  MapMode = 5
  Placement = pos=(7.67535e-08,-84,27.3536) rot=(0,0,1;3.14159rad)
  sketch-geometry (2):
    g0: Circle CenterX=-50.2465 CenterY=-42 CenterZ=0 NormalX=0 NormalY=0 NormalZ=1 AngleXU=0 Radius=3
    g1: Circle CenterX=-33.7465 CenterY=-42 CenterZ=0 NormalX=0 NormalY=0 NormalZ=1 AngleXU=0 Radius=3
  constraints (4):
    c: Diameter(g0) = 6
    c: Coincident(g0,g-4)
    c: Diameter(g1) = 6
    c: Coincident(g1,g-3)
FEATURE [PartDesign::Pocket] Pocket025
  BaseFeature = -> Pad023
  Direction = (-2.80598e-09,0,-1)
  Length = 3.5
  Length2 = 5
  Placement = pos=(0,-84,2e-15) rot=(1,0,0;1.5708rad)
  Profile = -> Sketch053
  ReferenceAxis = -> Sketch053 [N_Axis]
  Refine = true
  Suppressed = false
  Type = 0
FEATURE [Sketcher::SketchObject] Sketch054
  ArcFitTolerance = 1e-06
  AttachmentSupport = -> [Pocket022]
  ExternalGeometry = -> [Pocket022]
  FullyConstrained = true
  MakeInternals = false
  MapMode = 5
  Placement = pos=(3.93837e-08,0,20.8536) rot=(0,0,1;0rad)
  sketch-geometry (8):
    g0: GeomPoint X=41.9965 Y=-37.25 Z=0
    g1: GeomPoint X=41.9965 Y=-46.75 Z=0
    g2: LineSegment [constr] StartX=41.9965 StartY=-37.25 StartZ=0 EndX=41.9965 EndY=-46.75 EndZ=0
    g3: GeomPoint [constr] X=41.9965 Y=-42 Z=0
    g4: LineSegment StartX=41.9965 StartY=-41 StartZ=0 EndX=41.1304 EndY=-42.5 EndZ=0
    g5: LineSegment StartX=41.1304 StartY=-42.5 StartZ=0 EndX=42.8625 EndY=-42.5 EndZ=0
    g6: LineSegment StartX=42.8625 StartY=-42.5 StartZ=0 EndX=41.9965 EndY=-41 EndZ=0
    g7: Circle [constr] CenterX=41.9965 CenterY=-42 CenterZ=0 NormalX=0 NormalY=0 NormalZ=1 AngleXU=0 Radius=1
  constraints (16):
    c: Symmetric(g-3,g-3,g0)
    c: Symmetric(g-4,g-4,g1)
    c: Coincident(g2,g0)
    c: Coincident(g2,g1)
    c: Symmetric(g2,g2,g3)
    c: Coincident(g4,g5)
    c: Coincident(g5,g6)
    c: Coincident(g6,g4)
    c: Equal(g4,g5)
    c: Equal(g4,g6)
    c: PointOnObject(g4,g7)
    c: PointOnObject(g5,g7)
    c: PointOnObject(g6,g7)
    c: Radius(g7) = 1
    c: Coincident(g7,g3)
    c: PointOnObject(g6,g2)
FEATURE [PartDesign::Pocket] Pocket026
  BaseFeature = -> Pocket022
  Direction = (-1.88858e-09,0,-1)
  Length = 0.5
  Length2 = 5
  Profile = -> Sketch054
  ReferenceAxis = -> Sketch054 [N_Axis]
  Refine = true
  Suppressed = false
  Type = 0
FEATURE [PartDesign::Body] Body004  label="Thread Block Modelled"
  AllowCompound = false
  Group = -> [Clone,Sketch018,Hole002,Sketch040,Pad019,Chamfer015,Chamfer016,Sketch041,Pocket018,Sketch043,Pocket019,Sketch044,Pad020,Sketch045,Pad021,Sketch046,Pocket020,Sketch047,Pocket021,Sketch048,Pad022,Sketch049,Pocket022,Sketch054,Pocket026]
  Origin = -> Origin004
  Placement = pos=(0,-23,0) rot=(0,0,1;0rad)
  Tip = -> Pocket026
FEATURE [Sketcher::SketchObject] Sketch055
  ArcFitTolerance = 1e-06
  AttachmentSupport = -> [Pocket014]
  ExternalGeometry = -> [Pocket014]
  FullyConstrained = true
  MakeInternals = false
  MapMode = 5
  Placement = pos=(42,-84,14) rot=(0.57735,0.57735,0.57735;4.18879rad)
  sketch-geometry (2):
    g0: Circle CenterX=0 CenterY=-0.03 CenterZ=0 NormalX=0 NormalY=0 NormalZ=1 AngleXU=0 Radius=3.03
    g1: Circle CenterX=0 CenterY=-0.03 CenterZ=0 NormalX=0 NormalY=0 NormalZ=1 AngleXU=0 Radius=3.75
  constraints (5):
    c: PointOnObject(g0,g-2)
    c: Tangent(g0,g-3)
    c: Diameter(g0) = 6.06
    c: Diameter(g1) = 7.5
    c: Coincident(g1,g0)
FEATURE [PartDesign::Pad] Pad024
  BaseFeature = -> Pocket014
  Direction = (0,1,0)
  Length = 21
  Length2 = 10
  Placement = pos=(42,-84,14) rot=(0.57735,-0.57735,0.57735;2.0944rad)
  Profile = -> Sketch055
  ReferenceAxis = -> Sketch055 [N_Axis]
  Refine = true
  Reversed = true
  Suppressed = false
  Type = 0
FEATURE [Sketcher::SketchObject] Sketch056
  ArcFitTolerance = 1e-06
  AttachmentSupport = -> [Pad024]
  ExternalGeometry = -> [Pad024]
  FullyConstrained = true
  MakeInternals = false
  MapMode = 5
  Placement = pos=(42,-84,14) rot=(0.57735,0.57735,0.57735;4.18879rad)
  sketch-geometry (2):
    g0: Circle CenterX=0 CenterY=0 CenterZ=0 NormalX=0 NormalY=0 NormalZ=1 AngleXU=0 Radius=2.9
    g1: Circle CenterX=0 CenterY=-0.03 CenterZ=0 NormalX=0 NormalY=0 NormalZ=1 AngleXU=0 Radius=3.75
  constraints (4):
    c: Coincident(g0,g-1)
    c: Diameter(g0) = 5.8
    c: Coincident(g1,g-3)
    c: Equal(g1,g-3)
FEATURE [PartDesign::Pocket] Pocket027
  BaseFeature = -> Pad024
  Direction = (0,-1,0)
  Length = 8
  Length2 = 5
  Placement = pos=(42,-84,14) rot=(0.57735,-0.57735,0.57735;2.0944rad)
  Profile = -> Sketch056
  ReferenceAxis = -> Sketch056 [N_Axis]
  Refine = true
  Suppressed = false
  Type = 0
FEATURE [Part::FeaturePython] BinBase  label="2u Gridfinity Base Plate"  # WARN: FeaturePython — macro-defined, semantics opaque (R4)
  BaseProfileBottomChamfer = 0.8
  BaseProfileHeight = 4.75
  BaseProfileTopChamfer = 2.15
  BaseProfileVerticalSection = 1.8
  BinBottomRadius = 0.8
  BinOuterRadius = 3.75
  BinUnit = 41.5
  BinVerticalRadius = 1.6
  CustomHeight = 42
  GridSize = 42
  HeightUnitValue = 7
  HeightUnits = 1
  MagnetHoleDepth = 2.4
  MagnetHoleDiameter = 6.5
  MagnetHoleDistanceFromEdge = 8
  MagnetHoles = true
  NonStandardHeight = false
  Placement = pos=(-72,-63,-2) rot=(0,0,1;0rad)
  ScrewHoleDepth = 6
  ScrewHoleDiameter = 3
  ScrewHoles = true
  SequentialBridgingLayerHeight = 0.2
  StackingLip = false
  StackingLipBottomChamfer = 0.7
  StackingLipTopChamfer = 1.5
  StackingLipTopLedge = 0.4
  StackingLipVerticalSection = 1.8
  Tolerance = 0.25
  TotalHeight = 7
  WallThickness = 1
  version = 0.6.0
  xGridUnits = 2
  xTotalWidth = 83.5
  yGridUnits = 2
  yTotalWidth = 83.5
FEATURE [PartDesign::ShapeBinder] CopyBinBase
  Placement = pos=(-72,-63,-2) rot=(0,0,1;0rad)
  TraceSupport = false
FEATURE [PartDesign::Plane] DatumPlane011
  AttachmentSupport = -> [CopyBinBase]
  Length = 186.287
  MapMode = 5
  Placement = pos=(-72,-63,-9) rot=(1,0,0;3.14159rad)
  ResizeMode = 0
  Width = 177.287
FEATURE [PartDesign::SubShapeBinder] Binder
  BindCopyOnChange = 0
  BindMode = 0
  ClaimChildren = false
  Context = -> Body007 [Binder.]
  Fuse = false
  MakeFace = true
  OffsetFill = false
  OffsetIntersection = false
  OffsetJoinType = 0
  OffsetOpenResult = false
  PartialLoad = false
  Refine = true
  Relative = true
  Support = -> [BinBase]
  _Version = 2
FEATURE [PartDesign::SubShapeBinder] Binder001
  BindCopyOnChange = 0
  BindMode = 0
  ClaimChildren = false
  Context = -> Body007 [Binder001.]
  Fuse = false
  MakeFace = true
  OffsetFill = false
  OffsetIntersection = false
  OffsetJoinType = 0
  OffsetOpenResult = false
  PartialLoad = false
  Refine = true
  Relative = true
  Support = -> [BinBase[Face242]]
  _Version = 2
FEATURE [PartDesign::SubShapeBinder] Binder002
  BindCopyOnChange = 0
  BindMode = 0
  ClaimChildren = false
  Context = -> Body007 [Binder002.]
  Fuse = false
  MakeFace = true
  OffsetFill = false
  OffsetIntersection = false
  OffsetJoinType = 0
  OffsetOpenResult = false
  PartialLoad = false
  Refine = true
  Relative = true
  Support = -> [BinBase[Face2]]
  _Version = 2
FEATURE [PartDesign::SubShapeBinder] Binder003
  BindCopyOnChange = 0
  BindMode = 0
  ClaimChildren = false
  Context = -> Body007 [Binder003.]
  Fuse = false
  MakeFace = true
  OffsetFill = false
  OffsetIntersection = false
  OffsetJoinType = 0
  OffsetOpenResult = false
  PartialLoad = false
  Refine = true
  Relative = true
  Support = -> [BinBase[Face236]]
  _Version = 2
FEATURE [PartDesign::SubShapeBinder] Binder004
  BindCopyOnChange = 0
  BindMode = 0
  ClaimChildren = false
  Context = -> Body007 [Binder004.]
  Fuse = false
  MakeFace = true
  OffsetFill = false
  OffsetIntersection = false
  OffsetJoinType = 0
  OffsetOpenResult = false
  PartialLoad = false
  Refine = true
  Relative = true
  Support = -> [BinBase[Face234]]
  _Version = 2
FEATURE [Sketcher::SketchObject] Sketch060
  ArcFitTolerance = 1e-06
  AttachmentSupport = -> [DatumPlane011]
  ExternalGeometry = -> [Binder004,Binder001,Binder003,Binder002]
  FullyConstrained = true
  MakeInternals = false
  MapMode = 5
  Placement = pos=(-72,-63,-9) rot=(1,0,0;3.14159rad)
  sketch-geometry (8):
    g0: Circle CenterX=80 CenterY=13 CenterZ=0 NormalX=0 NormalY=0 NormalZ=1 AngleXU=0 Radius=1.3
    g1: Circle CenterX=80 CenterY=-13 CenterZ=0 NormalX=0 NormalY=0 NormalZ=1 AngleXU=0 Radius=1.3
    g2: Circle CenterX=80 CenterY=-29 CenterZ=0 NormalX=0 NormalY=0 NormalZ=1 AngleXU=0 Radius=1.3
    g3: Circle CenterX=80 CenterY=-55 CenterZ=0 NormalX=0 NormalY=0 NormalZ=1 AngleXU=0 Radius=1.3
    g4: Circle CenterX=148 CenterY=-55 CenterZ=0 NormalX=0 NormalY=0 NormalZ=1 AngleXU=0 Radius=1.3
    g5: Circle CenterX=148 CenterY=-29 CenterZ=0 NormalX=0 NormalY=0 NormalZ=1 AngleXU=0 Radius=1.3
    g6: Circle CenterX=148 CenterY=-13 CenterZ=0 NormalX=0 NormalY=0 NormalZ=1 AngleXU=0 Radius=1.3
    g7: Circle CenterX=148 CenterY=13 CenterZ=0 NormalX=0 NormalY=0 NormalZ=1 AngleXU=0 Radius=1.3
  constraints (16):
    c: Diameter(g0) = 2.6
    c: Coincident(g0,g-3)
    c: Diameter(g1) = 2.6
    c: Coincident(g1,g-8)
    c: Diameter(g2) = 2.6
    c: Coincident(g2,g-7)
    c: Diameter(g3) = 2.6
    c: Coincident(g3,g-6)
    c: Diameter(g4) = 2.6
    c: Coincident(g4,g-5)
    c: Diameter(g5) = 2.6
    c: Coincident(g5,g-10)
    c: Diameter(g6) = 2.6
    c: Coincident(g6,g-9)
    c: Diameter(g7) = 2.6
    c: Coincident(g7,g-4)
FEATURE [Sketcher::SketchObject] Sketch061
  ArcFitTolerance = 1e-06
  AttachmentSupport = -> [Pocket016]
  ExternalGeometry = -> [Pocket016]
  FullyConstrained = true
  MakeInternals = false
  MapMode = 5
  Placement = pos=(84,0,0) rot=(0.707107,0,0.707107;3.14159rad)
  expr: Constraints[19] = VarSet.HoleDiameter
  sketch-geometry (9):
    g0: LineSegment [constr] StartX=5 StartY=84 StartZ=0 EndX=5 EndY=56 EndZ=0
    g1: LineSegment [constr] StartX=5 StartY=56 StartZ=0 EndX=5 EndY=28 EndZ=0
    g2: LineSegment [constr] StartX=5 StartY=28 StartZ=0 EndX=5 EndY=0 EndZ=0
    g3: LineSegment [constr] StartX=5 StartY=56 StartZ=0 EndX=0 EndY=56 EndZ=0
    g4: LineSegment [constr] StartX=5 StartY=28 StartZ=0 EndX=0 EndY=28 EndZ=0
    g5: GeomPoint X=2.5 Y=56 Z=0
    g6: GeomPoint X=2.5 Y=28 Z=0
    g7: Circle CenterX=2.5 CenterY=56 CenterZ=0 NormalX=0 NormalY=0 NormalZ=1 AngleXU=0 Radius=1.3
    g8: Circle CenterX=2.5 CenterY=28 CenterZ=0 NormalX=0 NormalY=0 NormalZ=1 AngleXU=0 Radius=1.3
  constraints (20):
    c: Coincident(g0,g-4)
    c: PointOnObject(g0,g-4)
    c: Coincident(g1,g0)
    c: PointOnObject(g1,g-4)
    c: Coincident(g2,g1)
    c: Coincident(g2,g-4)
    c: Equal(g0,g1)
    c: Equal(g1,g2)
    c: Coincident(g3,g0)
    c: PointOnObject(g3,g-5)
    c: Horizontal(g3)
    c: Coincident(g4,g1)
    c: PointOnObject(g4,g-5)
    c: Horizontal(g4)
    c: Symmetric(g3,g3,g5)
    c: Symmetric(g4,g4,g6)
    c: Coincident(g7,g5)
    c: Coincident(g8,g6)
    c: Equal(g7,g8)
    c: Diameter(g8) = 2.6
FEATURE [App::VarSet] VarSet
  HoleDepth = 6
  HoleDiameter = 2.6
FEATURE [PartDesign::Pocket] Pocket031
  BaseFeature = -> Pocket016
  Direction = (-1,0,2e-16)
  Length = 6
  Length2 = 5
  Placement = pos=(0,0,0) rot=(1,0,0;1.5708rad)
  Profile = -> Sketch061
  ReferenceAxis = -> Sketch061 [N_Axis]
  Refine = true
  Suppressed = false
  Type = 0
  expr: Length = VarSet.HoleDepth
FEATURE [Sketcher::SketchObject] Sketch062
  ArcFitTolerance = 1e-06
  AttachmentSupport = -> [Pocket031]
  ExternalGeometry = -> [Pocket031]
  FullyConstrained = true
  MakeInternals = false
  MapMode = 5
  Placement = pos=(0,0,0) rot=(0.707107,0,-0.707107;3.14159rad)
  expr: Constraints[19] = VarSet.HoleDiameter
  sketch-geometry (9):
    g0: LineSegment [constr] StartX=-5 StartY=84 StartZ=0 EndX=-5 EndY=56 EndZ=0
    g1: LineSegment [constr] StartX=-5 StartY=56 StartZ=0 EndX=-5 EndY=28 EndZ=0
    g2: LineSegment [constr] StartX=-5 StartY=28 StartZ=0 EndX=-5 EndY=0 EndZ=0
    g3: LineSegment [constr] StartX=-5 StartY=56 StartZ=0 EndX=0 EndY=56 EndZ=0
    g4: LineSegment [constr] StartX=-5 StartY=28 StartZ=0 EndX=0 EndY=28 EndZ=0
    g5: GeomPoint [constr] X=-2.5 Y=56 Z=0
    g6: GeomPoint [constr] X=-2.5 Y=28 Z=0
    g7: Circle CenterX=-2.5 CenterY=56 CenterZ=0 NormalX=0 NormalY=0 NormalZ=1 AngleXU=0 Radius=1.3
    g8: Circle CenterX=-2.5 CenterY=28 CenterZ=0 NormalX=0 NormalY=0 NormalZ=1 AngleXU=0 Radius=1.3
  constraints (20):
    c: Coincident(g0,g-3)
    c: Vertical(g0)
    c: Coincident(g1,g0)
    c: Vertical(g1)
    c: Coincident(g2,g1)
    c: Coincident(g2,g-5)
    c: Equal(g2,g1)
    c: Equal(g1,g0)
    c: Coincident(g3,g0)
    c: PointOnObject(g3,g-4)
    c: Horizontal(g3)
    c: Coincident(g4,g1)
    c: PointOnObject(g4,g-4)
    c: Horizontal(g4)
    c: Symmetric(g3,g3,g5)
    c: Symmetric(g4,g4,g6)
    c: Coincident(g7,g5)
    c: Coincident(g8,g6)
    c: Equal(g8,g7)
    c: Diameter(g7) = 2.6
FEATURE [PartDesign::Pocket] Pocket032
  BaseFeature = -> Pocket031
  Direction = (1,0,2e-16)
  Length = 6
  Length2 = 5
  Placement = pos=(0,0,0) rot=(1,0,0;1.5708rad)
  Profile = -> Sketch062
  ReferenceAxis = -> Sketch062 [N_Axis]
  Refine = true
  Suppressed = false
  Type = 0
  expr: Length = VarSet.HoleDepth
FEATURE [Sketcher::SketchObject] Sketch063
  ArcFitTolerance = 1e-06
  AttachmentSupport = -> [Pocket032]
  ExternalGeometry = -> [Pocket032]
  FullyConstrained = true
  MakeInternals = false
  MapMode = 5
  Placement = pos=(0,-84,0) rot=(1,0,0;1.5708rad)
  expr: Constraints[19] = VarSet.HoleDiameter
  sketch-geometry (9):
    g0: LineSegment [constr] StartX=0 StartY=5 StartZ=0 EndX=28 EndY=5 EndZ=0
    g1: LineSegment [constr] StartX=28 StartY=5 StartZ=0 EndX=56 EndY=5 EndZ=0
    g2: LineSegment [constr] StartX=56 StartY=5 StartZ=0 EndX=84 EndY=5 EndZ=0
    g3: LineSegment [constr] StartX=28 StartY=5 StartZ=0 EndX=28 EndY=0 EndZ=0
    g4: LineSegment [constr] StartX=56 StartY=5 StartZ=0 EndX=56 EndY=0 EndZ=0
    g5: GeomPoint [constr] X=28 Y=2.5 Z=0
    g6: GeomPoint [constr] X=56 Y=2.5 Z=0
    g7: Circle CenterX=28 CenterY=2.5 CenterZ=0 NormalX=0 NormalY=0 NormalZ=1 AngleXU=0 Radius=1.3
    g8: Circle CenterX=56 CenterY=2.5 CenterZ=0 NormalX=0 NormalY=0 NormalZ=1 AngleXU=0 Radius=1.3
  constraints (20):
    c: Coincident(g0,g-3)
    c: Horizontal(g0)
    c: Coincident(g1,g0)
    c: Horizontal(g1)
    c: Coincident(g2,g1)
    c: Coincident(g2,g-4)
    c: Equal(g2,g1)
    c: Equal(g1,g0)
    c: Coincident(g3,g0)
    c: PointOnObject(g3,g-5)
    c: Vertical(g3)
    c: Coincident(g4,g1)
    c: PointOnObject(g4,g-5)
    c: Vertical(g4)
    c: Symmetric(g3,g3,g5)
    c: Symmetric(g4,g4,g6)
    c: Coincident(g7,g5)
    c: Coincident(g8,g6)
    c: Equal(g7,g8)
    c: Diameter(g7) = 2.6
FEATURE [PartDesign::Pocket] Pocket033
  BaseFeature = -> Pocket032
  Direction = (0,1,-2e-16)
  Length = 6
  Length2 = 5
  Placement = pos=(0,0,0) rot=(1,0,0;1.5708rad)
  Profile = -> Sketch063
  ReferenceAxis = -> Sketch063 [N_Axis]
  Refine = true
  Suppressed = false
  Type = 0
  expr: Length = VarSet.HoleDepth
FEATURE [Sketcher::SketchObject] Sketch064
  ArcFitTolerance = 1e-06
  AttachmentSupport = -> [Pocket033]
  ExternalGeometry = -> [Pocket033]
  FullyConstrained = true
  MakeInternals = false
  MapMode = 5
  Placement = pos=(0,1.7e-15,0) rot=(-1,0,0;1.5708rad)
  expr: Constraints[19] = VarSet.HoleDiameter
  sketch-geometry (9):
    g0: LineSegment [constr] StartX=0 StartY=-5 StartZ=0 EndX=28 EndY=-5 EndZ=0
    g1: LineSegment [constr] StartX=28 StartY=-5 StartZ=0 EndX=56 EndY=-5 EndZ=0
    g2: LineSegment [constr] StartX=56 StartY=-5 StartZ=0 EndX=84 EndY=-5 EndZ=0
    g3: LineSegment [constr] StartX=28 StartY=-5 StartZ=0 EndX=28 EndY=0 EndZ=0
    g4: LineSegment [constr] StartX=56 StartY=-5 StartZ=0 EndX=56 EndY=0 EndZ=0
    g5: GeomPoint [constr] X=28 Y=-2.5 Z=0
    g6: GeomPoint [constr] X=56 Y=-2.5 Z=0
    g7: Circle CenterX=28 CenterY=-2.5 CenterZ=0 NormalX=0 NormalY=0 NormalZ=1 AngleXU=0 Radius=1.3
    g8: Circle CenterX=56 CenterY=-2.5 CenterZ=0 NormalX=0 NormalY=0 NormalZ=1 AngleXU=0 Radius=1.3
  constraints (20):
    c: Coincident(g-4,g0)
    c: Horizontal(g0)
    c: Coincident(g0,g1)
    c: Horizontal(g1)
    c: Coincident(g1,g2)
    c: Coincident(g2,g-5)
    c: Equal(g0,g1)
    c: Equal(g1,g2)
    c: Coincident(g3,g0)
    c: PointOnObject(g3,g-3)
    c: Vertical(g3)
    c: Coincident(g4,g1)
    c: PointOnObject(g4,g-3)
    c: Vertical(g4)
    c: Symmetric(g3,g3,g5)
    c: Symmetric(g4,g4,g6)
    c: Coincident(g7,g5)
    c: Coincident(g8,g6)
    c: Equal(g7,g8)
    c: Diameter(g7) = 2.6
FEATURE [PartDesign::Pocket] Pocket034
  BaseFeature = -> Pocket033
  Direction = (0,-1,-2e-16)
  Length = 6
  Length2 = 5
  Placement = pos=(0,0,0) rot=(1,0,0;1.5708rad)
  Profile = -> Sketch064
  ReferenceAxis = -> Sketch064 [N_Axis]
  Refine = true
  Suppressed = false
  Type = 0
  expr: Length = VarSet.HoleDepth
FEATURE [PartDesign::Body] Body  label="Base with Integrated Gridfinity"
  AllowCompound = false
  Group = -> [Sketch,Pad,Sketch001,Pad001,Sketch002,Hole,Sketch003,Pad002,DatumPlane,Sketch004,Pad003,DatumPlane001,Sketch005,Pad004,Chamfer,Chamfer001,Chamfer002,Chamfer003,Chamfer004,Chamfer005,Chamfer006,Chamfer007,Chamfer008,Chamfer009,Chamfer010,Chamfer011,Chamfer012,Fillet,Sketch027,Pad015,Fillet005,Sketch038,Pocket016,Sketch061,VarSet,Pocket031,Sketch062,Pocket032,Sketch063,Pocket033,Sketch064,Pocket034]
  Origin = -> Origin
  Tip = -> Pocket034
FEATURE [PartDesign::FeatureBase] Clone001
  BaseFeature = -> Body
  Suppressed = false
FEATURE [Sketcher::SketchObject] Sketch028
  ArcFitTolerance = 1e-06
  AttachmentSupport = -> [Clone001]
  ExternalGeometry = -> [Clone001]
  FullyConstrained = true
  MakeInternals = false
  MapMode = 5
  Placement = pos=(0,1.7e-15,0) rot=(0,0.707107,0.707107;3.14159rad)
  sketch-geometry (4):
    g0: LineSegment StartX=-84 StartY=0 StartZ=0 EndX=-84 EndY=-7 EndZ=0
    g1: LineSegment StartX=-84 StartY=-7 StartZ=0 EndX=0 EndY=-7 EndZ=0
    g2: LineSegment StartX=0 StartY=-7 StartZ=0 EndX=0 EndY=0 EndZ=0
    g3: LineSegment StartX=0 StartY=0 StartZ=0 EndX=-84 EndY=0 EndZ=0
  constraints (11):
    c: Coincident(g0,g1)
    c: Coincident(g1,g2)
    c: Coincident(g2,g3)
    c: Coincident(g3,g0)
    c: Vertical(g0)
    c: Vertical(g2)
    c: Horizontal(g1)
    c: Horizontal(g3)
    c: Distance(g1,g3) = 7
    c: Coincident(g0,g-4)
    c: PointOnObject(g1,g-2)
FEATURE [PartDesign::Pocket] Pocket009
  BaseFeature = -> Clone001
  Direction = (0,-1,2e-16)
  Length = 5
  Length2 = 5
  Profile = -> Sketch028
  ReferenceAxis = -> Sketch028 [N_Axis]
  Refine = true
  Suppressed = false
  Type = 1
FEATURE [Sketcher::SketchObject] Sketch029
  ArcFitTolerance = 1e-06
  AttachmentSupport = -> [Pocket009]
  ExternalGeometry = -> [Pocket009]
  FullyConstrained = true
  MakeInternals = false
  MapMode = 5
  Placement = pos=(0,0,3e-16) rot=(1,0,0;3.14159rad)
  sketch-geometry (20):
    g0: LineSegment [constr] StartX=0 StartY=84 StartZ=0 EndX=0 EndY=79 EndZ=0
    g1: LineSegment [constr] StartX=0 StartY=79 StartZ=0 EndX=5 EndY=79 EndZ=0
    g2: LineSegment [constr] StartX=5 StartY=79 StartZ=0 EndX=5 EndY=84 EndZ=0
    g3: LineSegment [constr] StartX=5 StartY=84 StartZ=0 EndX=0 EndY=84 EndZ=0
    g4: LineSegment [constr] StartX=0 StartY=0 StartZ=0 EndX=5 EndY=0 EndZ=0
    g5: LineSegment [constr] StartX=5 StartY=0 StartZ=0 EndX=5 EndY=5 EndZ=0
    g6: LineSegment [constr] StartX=5 StartY=5 StartZ=0 EndX=0 EndY=5 EndZ=0
    g7: LineSegment [constr] StartX=0 StartY=5 StartZ=0 EndX=0 EndY=0 EndZ=0
    g8: LineSegment [constr] StartX=84 StartY=0 StartZ=0 EndX=84 EndY=5 EndZ=0
    g9: LineSegment [constr] StartX=84 StartY=5 StartZ=0 EndX=79 EndY=5 EndZ=0
    g10: LineSegment [constr] StartX=79 StartY=5 StartZ=0 EndX=79 EndY=0 EndZ=0
    g11: LineSegment [constr] StartX=79 StartY=0 StartZ=0 EndX=84 EndY=0 EndZ=0
    g12: LineSegment [constr] StartX=84 StartY=84 StartZ=0 EndX=79 EndY=84 EndZ=0
    g13: LineSegment [constr] StartX=79 StartY=84 StartZ=0 EndX=79 EndY=79 EndZ=0
    g14: LineSegment [constr] StartX=79 StartY=79 StartZ=0 EndX=84 EndY=79 EndZ=0
    g15: LineSegment [constr] StartX=84 StartY=79 StartZ=0 EndX=84 EndY=84 EndZ=0
    g16: Circle CenterX=5 CenterY=79 CenterZ=0 NormalX=0 NormalY=0 NormalZ=1 AngleXU=0 Radius=1.5
    g17: Circle CenterX=5 CenterY=5 CenterZ=0 NormalX=0 NormalY=0 NormalZ=1 AngleXU=0 Radius=1.5
    g18: Circle CenterX=79 CenterY=5 CenterZ=0 NormalX=0 NormalY=0 NormalZ=1 AngleXU=0 Radius=1.5
    g19: Circle CenterX=79 CenterY=79 CenterZ=0 NormalX=0 NormalY=0 NormalZ=1 AngleXU=0 Radius=1.5
  constraints (52):
    c: Coincident(g0,g1)
    c: Coincident(g1,g2)
    c: Coincident(g2,g3)
    c: Coincident(g3,g0)
    c: Vertical(g0)
    c: Vertical(g2)
    c: Horizontal(g1)
    c: Horizontal(g3)
    c: Distance(g0,g2) = 5
    c: Distance(g1,g3) = 5
    c: Coincident(g0,g-4)
    c: Coincident(g4,g5)
    c: Coincident(g5,g6)
    c: Coincident(g6,g7)
    c: Coincident(g7,g4)
    c: Horizontal(g4)
    c: Horizontal(g6)
    c: Vertical(g5)
    c: Vertical(g7)
    c: Distance(g5,g7) = 5
    c: Distance(g4,g6) = 5
    c: Coincident(g4,g-1)
    c: Coincident(g8,g9)
    c: Coincident(g9,g10)
    c: Coincident(g10,g11)
    c: Coincident(g11,g8)
    c: Vertical(g8)
    c: Vertical(g10)
    c: Horizontal(g9)
    c: Horizontal(g11)
    c: Distance(g8,g10) = 5
    c: Distance(g9,g11) = 5
    c: Coincident(g8,g-6)
    c: Coincident(g12,g13)
    c: Coincident(g13,g14)
    c: Coincident(g14,g15)
    c: Coincident(g15,g12)
    c: Horizontal(g12)
    c: Horizontal(g14)
    c: Vertical(g13)
    c: Vertical(g15)
    c: Distance(g13,g15) = 5
    c: Distance(g12,g14) = 5
    c: Coincident(g12,g-6)
    c: Diameter(g16) = 3
    c: Coincident(g16,g1)
    c: Diameter(g17) = 3
    c: Coincident(g17,g5)
    c: Diameter(g18) = 3
    c: Coincident(g18,g9)
    c: Diameter(g19) = 3
    c: Coincident(g19,g13)
FEATURE [PartDesign::Pocket] Pocket010
  BaseFeature = -> Pocket009
  Direction = (0,0,1)
  Length = 4
  Length2 = 5
  Profile = -> Sketch029
  ReferenceAxis = -> Sketch029 [N_Axis]
  Refine = true
  Suppressed = false
  Type = 0
FEATURE [Sketcher::SketchObject] Sketch057
  ArcFitTolerance = 1e-06
  AttachmentSupport = -> [Pocket010]
  ExternalGeometry = -> [Pocket010]
  FullyConstrained = true
  MakeInternals = false
  MapMode = 5
  Placement = pos=(0,0,3e-16) rot=(1,0,0;3.14159rad)
  sketch-geometry (4):
    g0: Circle CenterX=5 CenterY=79 CenterZ=0 NormalX=0 NormalY=0 NormalZ=1 AngleXU=0 Radius=1.5
    g1: Circle CenterX=79 CenterY=79 CenterZ=0 NormalX=0 NormalY=0 NormalZ=1 AngleXU=0 Radius=1.5
    g2: Circle CenterX=79 CenterY=5 CenterZ=0 NormalX=0 NormalY=0 NormalZ=1 AngleXU=0 Radius=1.5
    g3: Circle CenterX=5 CenterY=5 CenterZ=0 NormalX=0 NormalY=0 NormalZ=1 AngleXU=0 Radius=1.5
  constraints (8):
    c: Coincident(g0,g-3)
    c: Equal(g0,g-3)
    c: Coincident(g1,g-4)
    c: Equal(g1,g-4)
    c: Coincident(g2,g-5)
    c: Equal(g2,g-5)
    c: Coincident(g3,g-6)
    c: Equal(g3,g-6)
FEATURE [PartDesign::Pocket] Pocket028
  BaseFeature = -> Pocket010
  Direction = (0,0,1)
  Length = 10
  Length2 = 5
  Profile = -> Sketch057
  ReferenceAxis = -> Sketch057 [N_Axis]
  Refine = true
  Suppressed = false
  Type = 0
FEATURE [Sketcher::SketchObject] Sketch058
  ArcFitTolerance = 1e-06
  AttachmentSupport = -> [Pocket028]
  ExternalGeometry = -> [Pocket028]
  FullyConstrained = true
  MakeInternals = false
  MapMode = 5
  Placement = pos=(0,2.2e-15,5) rot=(0,0,1;0rad)
  sketch-geometry (4):
    g0: Circle CenterX=5 CenterY=-5 CenterZ=0 NormalX=0 NormalY=0 NormalZ=1 AngleXU=0 Radius=3
    g1: Circle CenterX=5 CenterY=-79 CenterZ=0 NormalX=0 NormalY=0 NormalZ=1 AngleXU=0 Radius=3
    g2: Circle CenterX=79 CenterY=-79 CenterZ=0 NormalX=0 NormalY=0 NormalZ=1 AngleXU=0 Radius=3
    g3: Circle CenterX=79 CenterY=-5 CenterZ=0 NormalX=0 NormalY=0 NormalZ=1 AngleXU=0 Radius=3
  constraints (8):
    c: Diameter(g0) = 6
    c: Coincident(g0,g-3)
    c: Diameter(g1) = 6
    c: Coincident(g1,g-4)
    c: Diameter(g2) = 6
    c: Coincident(g2,g-5)
    c: Diameter(g3) = 6
    c: Coincident(g3,g-6)
FEATURE [PartDesign::Pocket] Pocket029
  BaseFeature = -> Pocket028
  Direction = (0,0,-1)
  Length = 3.25
  Length2 = 5
  Profile = -> Sketch058
  ReferenceAxis = -> Sketch058 [N_Axis]
  Refine = true
  Suppressed = false
  Type = 0
FEATURE [Sketcher::SketchObject] Sketch059
  ArcFitTolerance = 1e-06
  AttachmentSupport = -> [Pocket029]
  ExternalGeometry = -> [Pocket029]
  FullyConstrained = true
  MakeInternals = false
  MapMode = 5
  Placement = pos=(0,0,3e-16) rot=(1,0,0;3.14159rad)
  sketch-geometry (8):
    g0: LineSegment StartX=0 StartY=84 StartZ=0 EndX=0 EndY=0 EndZ=0
    g1: LineSegment StartX=0 StartY=0 StartZ=0 EndX=84 EndY=0 EndZ=0
    g2: LineSegment StartX=84 StartY=0 StartZ=0 EndX=84 EndY=84 EndZ=0
    g3: LineSegment StartX=84 StartY=84 StartZ=0 EndX=0 EndY=84 EndZ=0
    g4: Circle CenterX=79 CenterY=5 CenterZ=0 NormalX=0 NormalY=0 NormalZ=1 AngleXU=0 Radius=1.5
    g5: Circle CenterX=5 CenterY=5 CenterZ=0 NormalX=0 NormalY=0 NormalZ=1 AngleXU=0 Radius=1.5
    g6: Circle CenterX=5 CenterY=79 CenterZ=0 NormalX=0 NormalY=0 NormalZ=1 AngleXU=0 Radius=1.5
    g7: Circle CenterX=79 CenterY=79 CenterZ=0 NormalX=0 NormalY=0 NormalZ=1 AngleXU=0 Radius=1.5
  constraints (18):
    c: Coincident(g0,g1)
    c: Coincident(g1,g2)
    c: Coincident(g2,g3)
    c: Coincident(g3,g0)
    c: Vertical(g0)
    c: Vertical(g2)
    c: Horizontal(g1)
    c: Horizontal(g3)
    c: Coincident(g0,g-3)
    c: Coincident(g1,g-4)
    c: Coincident(g4,g-8)
    c: Equal(g4,g-8)
    c: Coincident(g5,g-5)
    c: Equal(g5,g-5)
    c: Coincident(g6,g-6)
    c: Equal(g6,g-6)
    c: Coincident(g7,g-7)
    c: Equal(g7,g-7)
FEATURE [PartDesign::Pad] Pad025
  BaseFeature = -> Pocket029
  Direction = (0,0,-1)
  Length = 1.25
  Length2 = 10
  Profile = -> Sketch059
  ReferenceAxis = -> Sketch059 [N_Axis]
  Refine = true
  Suppressed = false
  Type = 0
FEATURE [PartDesign::Pocket] Pocket030
  BaseFeature = -> Pad025
  Direction = (0,0,1)
  Length = 12
  Length2 = 5
  Profile = -> Sketch060
  ReferenceAxis = -> Sketch060 [N_Axis]
  Refine = true
  Suppressed = false
  Type = 1
FEATURE [PartDesign::FeatureBase] BaseFeature
  BaseFeature = -> BinBase
  Suppressed = false
FEATURE [PartDesign::Pocket] Pocket035
  BaseFeature = -> BaseFeature
  Direction = (0,0,1)
  Length = 5
  Length2 = 5
  Profile = -> BaseFeature [Face632,Face631,Face636,Face635,Face232,Face231,Face630,Face629]
  Refine = true
  Suppressed = false
  Type = 2
FEATURE [PartDesign::Body] Body009  label="Gridfinity Bolt On Base"
  AllowCompound = false
  BaseFeature = -> BinBase
  Group = -> [BaseFeature,Pocket035]
  Origin = -> Origin009
  Placement = pos=(-72,-63,0) rot=(0,0,1;0rad)
  Tip = -> Pocket035
FEATURE [PartDesign::FeaturePython] ScrewTogetherBaseplate  # WARN: FeaturePython — macro-defined, semantics opaque (R4)
  BaseProfileBottomChamfer = 0.7
  BaseProfileHeight = 4.25
  BaseProfileTopChamfer = 1.75
  BaseProfileVerticalSection = 1.8
  BaseThickness = 6.4
  BaseplateProfileTotalHeight = 0
  BaseplateTopLedgeWidth = 0.4
  BinBottomRadius = 1.15
  BinOuterRadius = 4
  BinVerticalRadius = 1.85
  Clearance = 0.25
  ConnectionHoleDiameter = 3.2
  GridSize = 42
  HeightUnitValue = 7
  MagnetBaseHole = 3
  MagnetBottomChamfer = 2
  MagnetChamfer = 0.4
  MagnetEdgeThickness = 1.2
  MagnetHoleDepth = 2.4
  MagnetHoleDiameter = 6.5
  MagnetHoleDistanceFromEdge = 8
  MagnetHolesShape = 0
  ScrewHoleDiameter = 3
  SmallFillet = 1
  Suppressed = false
  TotalHeight = 10.65
  version = 0.8.0
  xGridUnits = 4
  xTotalWidth = 168
  yGridUnits = 4
  yTotalWidth = 168
FEATURE [PartDesign::Body] Body010  label="Gridfinity Bolt Together Mesh"
  AllowCompound = false
  Group = -> [ScrewTogetherBaseplate]
  Origin = -> Origin010
  Placement = pos=(-59,45,0) rot=(0,0,1;0rad)
  Tip = -> ScrewTogetherBaseplate
FEATURE [Sketcher::SketchObject] Sketch065
  ArcFitTolerance = 1e-06
  AttachmentSupport = -> [Pocket030]
  ExternalGeometry = -> [Pocket030]
  FullyConstrained = true
  MakeInternals = false
  MapMode = 5
  Placement = pos=(0,-84,-8.9e-14) rot=(1,0,0;1.5708rad)
  sketch-geometry (6):
    g0: Circle CenterX=28 CenterY=2.5 CenterZ=0 NormalX=0 NormalY=0 NormalZ=1 AngleXU=0 Radius=1.3
    g1: Circle CenterX=56 CenterY=2.5 CenterZ=0 NormalX=0 NormalY=0 NormalZ=1 AngleXU=0 Radius=1.3
    g2: LineSegment StartX=0 StartY=5 StartZ=0 EndX=0 EndY=-1.25 EndZ=0
    g3: LineSegment StartX=0 StartY=-1.25 StartZ=0 EndX=84 EndY=-1.25 EndZ=0
    g4: LineSegment StartX=84 StartY=-1.25 StartZ=0 EndX=84 EndY=5 EndZ=0
    g5: LineSegment StartX=84 StartY=5 StartZ=0 EndX=0 EndY=5 EndZ=0
  constraints (14):
    c: Coincident(g0,g-8)
    c: Equal(g0,g-8)
    c: Coincident(g1,g-7)
    c: Equal(g1,g-7)
    c: Coincident(g2,g3)
    c: Coincident(g3,g4)
    c: Coincident(g4,g5)
    c: Coincident(g5,g2)
    c: Vertical(g2)
    c: Vertical(g4)
    c: Horizontal(g3)
    c: Horizontal(g5)
    c: Coincident(g2,g-5)
    c: Coincident(g3,g-3)
FEATURE [PartDesign::Pad] Pad026
  BaseFeature = -> Pocket030
  Direction = (0,-1,-1.1e-15)
  Length = 38
  Length2 = 10
  Profile = -> Sketch065
  ReferenceAxis = -> Sketch065 [N_Axis]
  Refine = true
  Suppressed = false
  Type = 0
FEATURE [Sketcher::SketchObject] Sketch066
  ArcFitTolerance = 1e-06
  AttachmentSupport = -> [Pocket027]
  FullyConstrained = true
  MakeInternals = false
  MapMode = 5
  Placement = pos=(42,-119,14) rot=(0.57735,-0.57735,0.57735;2.0944rad)
  sketch-geometry (2):
    g0: Circle CenterX=0 CenterY=0 CenterZ=0 NormalX=0 NormalY=0 NormalZ=1 AngleXU=0 Radius=3.75
    g1: Circle CenterX=0 CenterY=0 CenterZ=0 NormalX=0 NormalY=0 NormalZ=1 AngleXU=0 Radius=8.25
  constraints (4):
    c: Coincident(g0,g-1)
    c: Diameter(g1) = 16.5
    c: Coincident(g1,g0)
    c: Diameter(g0) = 7.5
FEATURE [PartDesign::Pocket] Pocket036
  BaseFeature = -> Pocket027
  Direction = (0,1,0)
  Length = 25
  Length2 = 5
  Placement = pos=(42,-84,14) rot=(0.57735,-0.57735,0.57735;2.0944rad)
  Profile = -> Sketch066
  ReferenceAxis = -> Sketch066 [N_Axis]
  Refine = true
  Suppressed = false
  Type = 1
FEATURE [Sketcher::SketchObject] Sketch067
  ArcFitTolerance = 1e-06
  AttachmentSupport = -> [Pocket036]
  FullyConstrained = true
  MakeInternals = false
  MapMode = 5
  Placement = pos=(42,-119,14) rot=(0.57735,-0.57735,0.57735;2.0944rad)
  sketch-geometry (5):
    g0: LineSegment StartX=-1.55 StartY=-2.55 StartZ=0 EndX=1.55 EndY=-2.55 EndZ=0
    g1: LineSegment StartX=1.55 StartY=-2.55 StartZ=0 EndX=1.55 EndY=2.55 EndZ=0
    g2: LineSegment StartX=1.55 StartY=2.55 StartZ=0 EndX=-1.55 EndY=2.55 EndZ=0
    g3: LineSegment StartX=-1.55 StartY=2.55 StartZ=0 EndX=-1.55 EndY=-2.55 EndZ=0
    g4: GeomPoint [constr] X=0 Y=0 Z=0
  constraints (12):
    c: Coincident(g0,g1)
    c: Coincident(g1,g2)
    c: Coincident(g2,g3)
    c: Coincident(g3,g0)
    c: Horizontal(g0)
    c: Horizontal(g2)
    c: Vertical(g1)
    c: Vertical(g3)
    c: Symmetric(g2,g0,g4)
    c: Distance(g1,g3) = 3.1
    c: Distance(g0,g2) = 5.1
    c: Coincident(g4,g-1)
FEATURE [PartDesign::Pocket] Pocket037
  BaseFeature = -> Pocket036
  Direction = (0,1,0)
  Length = 6
  Length2 = 5
  Placement = pos=(42,-84,14) rot=(0.57735,-0.57735,0.57735;2.0944rad)
  Profile = -> Sketch067
  ReferenceAxis = -> Sketch067 [N_Axis]
  Refine = true
  Suppressed = false
  Type = 0
FEATURE [Sketcher::SketchObject] Sketch068
  ArcFitTolerance = 1e-06
  AttachmentSupport = -> [Pocket037]
  ExternalGeometry = -> [Pocket037]
  FullyConstrained = true
  MakeInternals = false
  MapMode = 5
  Placement = pos=(42,-119,14) rot=(0.57735,-0.57735,0.57735;2.0944rad)
  sketch-geometry (2):
    g0: Circle CenterX=0 CenterY=0 CenterZ=0 NormalX=0 NormalY=0 NormalZ=1 AngleXU=0 Radius=5
    g1: Circle CenterX=0 CenterY=0 CenterZ=0 NormalX=0 NormalY=0 NormalZ=1 AngleXU=0 Radius=3.75
  constraints (4):
    c: Diameter(g0) = 10
    c: Coincident(g0,g-1)
    c: Coincident(g1,g0)
    c: Diameter(g1) = 7.5
FEATURE [PartDesign::Pad] Pad027
  BaseFeature = -> Pocket037
  Direction = (0,-1,0)
  Length = 10
  Length2 = 10
  Placement = pos=(42,-84,14) rot=(0.57735,-0.57735,0.57735;2.0944rad)
  Profile = -> Sketch068
  ReferenceAxis = -> Sketch068 [N_Axis]
  Refine = true
  Reversed = true
  Suppressed = false
  Type = 0
FEATURE [PartDesign::Chamfer] Chamfer017
  Angle = 45
  Base = -> Pad027 [Edge106]
  BaseFeature = -> Pad027
  ChamferType = 0
  FlipDirection = false
  Placement = pos=(42,-84,14) rot=(0.57735,-0.57735,0.57735;2.0944rad)
  Refine = true
  Size = 1
  Size2 = 1
  SupportTransform = false
  Suppressed = false
  UseAllEdges = false
FEATURE [PartDesign::ShapeBinder] CopyChamfer017
  Placement = pos=(42,-84,14) rot=(0.57735,-0.57735,0.57735;2.0944rad)
  TraceSupport = false
FEATURE [PartDesign::Plane] DatumPlane012
  AttachmentSupport = -> [CopyChamfer017]
  Length = 63.2646
  MapMode = 5
  Placement = pos=(42,-119,14) rot=(0.57735,-0.57735,0.57735;2.0944rad)
  ResizeMode = 0
  Width = 101.239
FEATURE [Sketcher::SketchObject] Sketch069
  ArcFitTolerance = 1e-06
  AttachmentSupport = -> [DatumPlane012]
  FullyConstrained = true
  MakeInternals = false
  MapMode = 5
  Placement = pos=(42,-119,14) rot=(0.57735,-0.57735,0.57735;2.0944rad)
  sketch-geometry (9):
    g0: ArcOfCircle CenterX=0 CenterY=0 CenterZ=0 NormalX=0 NormalY=0 NormalZ=1 AngleXU=0 Radius=2.5 StartAngle=0.927295 EndAngle=2.2143
    g1: LineSegment [constr] StartX=-1.5 StartY=-2.5 StartZ=0 EndX=1.5 EndY=-2.5 EndZ=0
    g2: LineSegment [constr] StartX=1.5 StartY=-2.5 StartZ=0 EndX=1.5 EndY=2.5 EndZ=0
    g3: LineSegment [constr] StartX=1.5 StartY=2.5 StartZ=0 EndX=-1.5 EndY=2.5 EndZ=0
    g4: LineSegment [constr] StartX=-1.5 StartY=2.5 StartZ=0 EndX=-1.5 EndY=-2.5 EndZ=0
    g5: GeomPoint [constr] X=0 Y=0 Z=0
    g6: ArcOfCircle CenterX=0 CenterY=0 CenterZ=0 NormalX=0 NormalY=0 NormalZ=1 AngleXU=0 Radius=2.5 StartAngle=4.06889 EndAngle=5.35589
    g7: LineSegment StartX=-1.5 StartY=2 StartZ=0 EndX=-1.5 EndY=-2 EndZ=0
    g8: LineSegment StartX=1.5 StartY=-2 StartZ=0 EndX=1.5 EndY=2 EndZ=0
  constraints (24):
    c: Diameter(g0) = 5
    c: Coincident(g0,g-1)
    c: Coincident(g1,g2)
    c: Coincident(g2,g3)
    c: Coincident(g3,g4)
    c: Coincident(g4,g1)
    c: Horizontal(g1)
    c: Horizontal(g3)
    c: Vertical(g2)
    c: Vertical(g4)
    c: Symmetric(g3,g1,g5)
    c: Distance(g2,g4) = 3
    c: Distance(g1,g3) = 5
    c: Coincident(g5,g0)
    c: PointOnObject(g6,g2)
    c: PointOnObject(g0,g2)
    c: Equal(g0,g6)
    c: PointOnObject(g0,g4)
    c: PointOnObject(g6,g4)
    c: Coincident(g0,g6)
    c: Coincident(g7,g0)
    c: Coincident(g7,g6)
    c: Coincident(g8,g6)
    c: Coincident(g8,g0)
FEATURE [PartDesign::Pad] Pad028
  Direction = (0,-1,0)
  Length = 6
  Length2 = 10
  Placement = pos=(42,-119,14) rot=(0.57735,-0.57735,0.57735;2.0944rad)
  Profile = -> Sketch069
  ReferenceAxis = -> Sketch069 [N_Axis]
  Refine = true
  Reversed = true
  Suppressed = false
  Type = 0
FEATURE [Sketcher::SketchObject] Sketch070
  ArcFitTolerance = 1e-06
  AttachmentSupport = -> [Pad028]
  FullyConstrained = true
  MakeInternals = false
  MapMode = 5
  Placement = pos=(42,-119,14) rot=(0.57735,-0.57735,0.57735;2.0944rad)
  sketch-geometry (1):
    g0: Circle CenterX=0 CenterY=0 CenterZ=0 NormalX=0 NormalY=0 NormalZ=1 AngleXU=0 Radius=2.5
  constraints (2):
    c: Diameter(g0) = 5
    c: Coincident(g0,g-1)
FEATURE [PartDesign::Pad] Pad029
  BaseFeature = -> Pad028
  Direction = (0,-1,0)
  Length = 1.5
  Length2 = 10
  Placement = pos=(42,-119,14) rot=(0.57735,-0.57735,0.57735;2.0944rad)
  Profile = -> Sketch070
  ReferenceAxis = -> Sketch070 [N_Axis]
  Refine = true
  Suppressed = false
  Type = 0
FEATURE [Sketcher::SketchObject] Sketch071
  ArcFitTolerance = 1e-06
  AttachmentSupport = -> [Pad029]
  FullyConstrained = true
  MakeInternals = false
  MapMode = 5
  Placement = pos=(42,-120.5,14) rot=(0.57735,-0.57735,0.57735;2.0944rad)
  sketch-geometry (1):
    g0: Circle CenterX=0 CenterY=0 CenterZ=0 NormalX=0 NormalY=0 NormalZ=1 AngleXU=0 Radius=4.75
  constraints (2):
    c: Diameter(g0) = 9.5
    c: Coincident(g0,g-1)
FEATURE [PartDesign::Pad] Pad030
  BaseFeature = -> Pad029
  Direction = (0,-1,0)
  Length = 1.5
  Length2 = 10
  Placement = pos=(42,-119,14) rot=(0.57735,-0.57735,0.57735;2.0944rad)
  Profile = -> Sketch071
  ReferenceAxis = -> Sketch071 [N_Axis]
  Refine = true
  Suppressed = false
  Type = 0
FEATURE [Sketcher::SketchObject] Sketch072
  ArcFitTolerance = 1e-06
  AttachmentSupport = -> [Pad030]
  FullyConstrained = true
  MakeInternals = false
  MapMode = 5
  Placement = pos=(42,-122,14) rot=(0.57735,-0.57735,0.57735;2.0944rad)
  sketch-geometry (18):
    g0: LineSegment [constr] StartX=0 StartY=0 StartZ=0 EndX=-8 EndY=0 EndZ=0
    g1: LineSegment [constr] StartX=-8 StartY=0 StartZ=0 EndX=-8 EndY=17.5 EndZ=0
    g2: LineSegment [constr] StartX=-8 StartY=0 StartZ=0 EndX=-8 EndY=-17.5 EndZ=0
    g3: Circle CenterX=-8 CenterY=17.5 CenterZ=0 NormalX=0 NormalY=0 NormalZ=1 AngleXU=0 Radius=2
    g4: Circle CenterX=-8 CenterY=-17.5 CenterZ=0 NormalX=0 NormalY=0 NormalZ=1 AngleXU=0 Radius=2
    g5: ArcOfCircle CenterX=-8 CenterY=17.5 CenterZ=0 NormalX=0 NormalY=0 NormalZ=1 AngleXU=0 Radius=3.5 StartAngle=0 EndAngle=3.14159
    g6: ArcOfCircle [constr] CenterX=-8 CenterY=0 CenterZ=0 NormalX=0 NormalY=0 NormalZ=1 AngleXU=0 Radius=14 StartAngle=1.82348 EndAngle=7.6013
    g7: LineSegment [constr] StartX=-8 StartY=-17.5 StartZ=0 EndX=-11.5 EndY=-17.5 EndZ=0
    g8: LineSegment [constr] StartX=-8 StartY=-17.5 StartZ=0 EndX=-4.5 EndY=-17.5 EndZ=0
    g9: LineSegment [constr] StartX=-8 StartY=17.5 StartZ=0 EndX=-4.5 EndY=17.5 EndZ=0
    g10: LineSegment [constr] StartX=-8 StartY=17.5 StartZ=0 EndX=-11.5 EndY=17.5 EndZ=0
    g11: LineSegment StartX=-4.5 StartY=17.5 StartZ=0 EndX=-4.5 EndY=13.5554 EndZ=0
    g12: LineSegment StartX=-11.5 StartY=17.5 StartZ=0 EndX=-11.5 EndY=13.5554 EndZ=0
    g13: ArcOfCircle CenterX=-8 CenterY=0 CenterZ=0 NormalX=0 NormalY=0 NormalZ=1 AngleXU=0 Radius=14 StartAngle=1.82348 EndAngle=4.45971
    g14: ArcOfCircle CenterX=-8 CenterY=0 CenterZ=0 NormalX=0 NormalY=0 NormalZ=1 AngleXU=0 Radius=14 StartAngle=4.96507 EndAngle=7.6013
    g15: ArcOfCircle CenterX=-8 CenterY=-17.5 CenterZ=0 NormalX=0 NormalY=0 NormalZ=1 AngleXU=0 Radius=3.5 StartAngle=3.14159 EndAngle=6.28319
    g16: LineSegment StartX=-11.5 StartY=-13.5554 StartZ=0 EndX=-11.5 EndY=-17.5 EndZ=0
    g17: LineSegment StartX=-4.5 StartY=-13.5554 StartZ=0 EndX=-4.5 EndY=-17.5 EndZ=0
  constraints (50):
    c: Distance(g0) = 8
    c: Coincident(g0,g-1)
    c: PointOnObject(g0,g-1)
    c: Coincident(g1,g0)
    c: Vertical(g1)
    c: Coincident(g2,g0)
    c: Vertical(g2)
    c: DistanceY(g1,g1) = 17.5
    c: Equal(g1,g2)
    c: Diameter(g3) = 4
    c: Coincident(g3,g1)
    c: Diameter(g4) = 4
    c: Coincident(g4,g2)
    c: Diameter(g5) = 7
    c: Coincident(g5,g1)
    c: Diameter(g6) = 28
    c: Coincident(g6,g0)
    c: Coincident(g7,g2)
    c: Horizontal(g7)
    c: Coincident(g8,g2)
    c: Horizontal(g8)
    c: Coincident(g9,g1)
    c: Horizontal(g9)
    c: Coincident(g10,g1)
    c: Horizontal(g10)
    c: PointOnObject(g13,g6)
    c: Coincident(g11,g9)
    c: Vertical(g11)
    c: Coincident(g12,g10)
    c: Vertical(g12)
    c: Coincident(g5,g9)
    c: Coincident(g5,g10)
    c: Coincident(g6,g12)
    c: Coincident(g6,g11)
    c: Coincident(g13,g0)
    c: PointOnObject(g13,g12)
    c: Coincident(g14,g6)
    c: Coincident(g14,g0)
    c: DistanceX(g8,g8) = 3.5
    c: Vertical(g14,g8)
    c: Vertical(g13,g7)
    c: Coincident(g15,g2)
    c: Coincident(g15,g8)
    c: Coincident(g15,g7)
    c: Coincident(g16,g13)
    c: Coincident(g16,g7)
    c: Coincident(g17,g14)
    c: Coincident(g17,g8)
    c: Vertical(g17)
    c: Tangent(g17,g15)
FEATURE [PartDesign::Pad] Pad031
  BaseFeature = -> Pad030
  Direction = (0,-1,0)
  Length = 19
  Length2 = 10
  Placement = pos=(42,-119,14) rot=(0.57735,-0.57735,0.57735;2.0944rad)
  Profile = -> Sketch072
  ReferenceAxis = -> Sketch072 [N_Axis]
  Refine = true
  Suppressed = false
  Type = 0
FEATURE [Sketcher::SketchObject] Sketch073
  ArcFitTolerance = 1e-06
  AttachmentSupport = -> [Pad031]
  ExternalGeometry = -> [Pad031]
  FullyConstrained = true
  MakeInternals = false
  MapMode = 5
  Placement = pos=(42,-141,14) rot=(0.57735,-0.57735,0.57735;2.0944rad)
  sketch-geometry (7):
    g0: LineSegment [constr] StartX=0 StartY=0 StartZ=0 EndX=-8 EndY=0 EndZ=0
    g1: LineSegment [constr] StartX=-8 StartY=0 StartZ=0 EndX=-25 EndY=0 EndZ=0
    g2: LineSegment StartX=-25 StartY=0 StartZ=0 EndX=-25 EndY=7.3 EndZ=0
    g3: LineSegment StartX=-25 StartY=0 StartZ=0 EndX=-25 EndY=-7.3 EndZ=0
    g4: LineSegment StartX=-25 StartY=7.3 StartZ=0 EndX=-19.9461 EndY=7.3 EndZ=0
    g5: LineSegment StartX=-25 StartY=-7.3 StartZ=0 EndX=-19.9461 EndY=-7.3 EndZ=0
    g6: LineSegment StartX=-19.9461 StartY=-7.3 StartZ=0 EndX=-19.9461 EndY=7.3 EndZ=0
  constraints (20):
    c: Distance(g0) = 8
    c: Coincident(g0,g-1)
    c: PointOnObject(g0,g-1)
    c: Distance(g1) = 17
    c: Coincident(g1,g0)
    c: PointOnObject(g1,g-1)
    c: Distance(g2) = 7.3
    c: Coincident(g2,g1)
    c: Vertical(g2)
    c: Coincident(g3,g1)
    c: Vertical(g3)
    c: Equal(g2,g3)
    c: Coincident(g4,g2)
    c: PointOnObject(g4,g-3)
    c: Horizontal(g4)
    c: Coincident(g5,g3)
    c: PointOnObject(g5,g-3)
    c: Horizontal(g5)
    c: Coincident(g6,g5)
    c: Coincident(g6,g4)
FEATURE [PartDesign::Pad] Pad032
  BaseFeature = -> Pad031
  Direction = (0,-1,0)
  Length = 10
  Length2 = 10
  Placement = pos=(42,-119,14) rot=(0.57735,-0.57735,0.57735;2.0944rad)
  Profile = -> Sketch073
  ReferenceAxis = -> Sketch073 [N_Axis]
  Refine = true
  Reversed = true
  Suppressed = false
  Type = 3
  UpToFace = -> Pad031 [Face9]
FEATURE [Sketcher::SketchObject] Sketch074
  ArcFitTolerance = 1e-06
  AttachmentSupport = -> [Pad032]
  ExternalGeometry = -> [Pad032]
  FullyConstrained = true
  MakeInternals = false
  MapMode = 5
  Placement = pos=(42,-141,14) rot=(0.57735,-0.57735,0.57735;2.0944rad)
  sketch-geometry (10):
    g0: LineSegment StartX=-11.5 StartY=21.4446 StartZ=0 EndX=-11.5 EndY=13.5554 EndZ=0
    g1: LineSegment StartX=-11.5 StartY=13.5554 StartZ=0 EndX=-4.5 EndY=13.5554 EndZ=0
    g2: LineSegment StartX=-4.5 StartY=13.5554 StartZ=0 EndX=-4.5 EndY=21.4446 EndZ=0
    g3: LineSegment StartX=-4.5 StartY=21.4446 StartZ=0 EndX=-11.5 EndY=21.4446 EndZ=0
    g4: GeomPoint [constr] X=-8 Y=17.5 Z=0
    g5: LineSegment StartX=-11.5 StartY=-21.4446 StartZ=0 EndX=-4.5 EndY=-21.4446 EndZ=0
    g6: LineSegment StartX=-4.5 StartY=-21.4446 StartZ=0 EndX=-4.5 EndY=-13.5554 EndZ=0
    g7: LineSegment StartX=-4.5 StartY=-13.5554 StartZ=0 EndX=-11.5 EndY=-13.5554 EndZ=0
    g8: LineSegment StartX=-11.5 StartY=-13.5554 StartZ=0 EndX=-11.5 EndY=-21.4446 EndZ=0
    g9: GeomPoint [constr] X=-8 Y=-17.5 Z=0
  constraints (22):
    c: Coincident(g0,g1)
    c: Coincident(g1,g2)
    c: Coincident(g2,g3)
    c: Coincident(g3,g0)
    c: Vertical(g0)
    c: Vertical(g2)
    c: Horizontal(g1)
    c: Horizontal(g3)
    c: Symmetric(g2,g0,g4)
    c: Coincident(g4,g-3)
    c: Coincident(g1,g-5)
    c: Coincident(g5,g6)
    c: Coincident(g6,g7)
    c: Coincident(g7,g8)
    c: Coincident(g8,g5)
    c: Horizontal(g5)
    c: Horizontal(g7)
    c: Vertical(g6)
    c: Vertical(g8)
    c: Symmetric(g7,g5,g9)
    c: Coincident(g9,g-4)
    c: Coincident(g6,g-5)
FEATURE [PartDesign::Pocket] Pocket038
  BaseFeature = -> Pad032
  Direction = (0,1,0)
  Length = 18
  Length2 = 5
  Placement = pos=(42,-119,14) rot=(0.57735,-0.57735,0.57735;2.0944rad)
  Profile = -> Sketch074
  ReferenceAxis = -> Sketch074 [N_Axis]
  Refine = true
  Suppressed = false
  Type = 0
FEATURE [PartDesign::Body] Body011  label="28BYJ-48 Stepper Motor"
  AllowCompound = false
  Group = -> [DatumPlane012,CopyChamfer017,Sketch069,Pad028,Sketch070,Pad029,Sketch071,Pad030,Sketch072,Pad031,Sketch073,Pad032,Sketch074,Pocket038]
  Origin = -> Origin011
  Placement = pos=(-93,0,0) rot=(0,0,1;0rad)
  Tip = -> Pocket038
FEATURE [Sketcher::SketchObject] Sketch075
  ArcFitTolerance = 1e-06
  AttachmentSupport = -> [Pad026]
  ExternalGeometry = -> [Pad026]
  FullyConstrained = true
  MakeInternals = false
  MapMode = 5
  Placement = pos=(0,-122,0) rot=(1,0,0;1.5708rad)
  sketch-geometry (14):
    g0: GeomPoint X=42 Y=5 Z=0
    g1: LineSegment [constr] StartX=42 StartY=5 StartZ=0 EndX=24.5 EndY=5 EndZ=0
    g2: LineSegment [constr] StartX=42 StartY=5 StartZ=0 EndX=59.5 EndY=5 EndZ=0
    g3: LineSegment [constr] StartX=24.5 StartY=5 StartZ=0 EndX=24.5 EndY=6 EndZ=0
    g4: LineSegment [constr] StartX=59.5 StartY=5 StartZ=0 EndX=59.5 EndY=6 EndZ=0
    g5: Circle CenterX=24.5 CenterY=6 CenterZ=0 NormalX=0 NormalY=0 NormalZ=1 AngleXU=0 Radius=1.7
    g6: Circle CenterX=59.5 CenterY=6 CenterZ=0 NormalX=0 NormalY=0 NormalZ=1 AngleXU=0 Radius=1.7
    g7: GeomPoint [constr] X=42 Y=5 Z=0
    g8: Circle CenterX=24.5 CenterY=6 CenterZ=0 NormalX=0 NormalY=0 NormalZ=1 AngleXU=0 Radius=3.64975
    g9: Circle CenterX=59.5 CenterY=6 CenterZ=0 NormalX=0 NormalY=0 NormalZ=1 AngleXU=0 Radius=3.64975
    g10: GeomPoint X=20.9899 Y=5 Z=0
    g11: GeomPoint X=28.0101 Y=5 Z=0
    g12: GeomPoint X=55.9899 Y=5 Z=0
    g13: GeomPoint X=63.0101 Y=5 Z=0
  constraints (30):
    c: Symmetric(g-3,g-3,g0)
    c: Distance(g1) = 17.5
    c: Coincident(g1,g0)
    c: PointOnObject(g1,g-3)
    c: Coincident(g2,g0)
    c: PointOnObject(g2,g-3)
    c: Equal(g1,g2)
    c: Distance(g3) = 1
    c: Coincident(g3,g1)
    c: Vertical(g3)
    c: Coincident(g4,g2)
    c: Vertical(g4)
    c: Equal(g3,g4)
    c: Diameter(g5) = 3.4
    c: Coincident(g5,g3)
    c: Coincident(g6,g4)
    c: Equal(g6,g5)
    c: Coincident(g7,g0)
    c: Coincident(g8,g3)
    c: Tangent(g8,g-5)
    c: Coincident(g9,g4)
    c: Tangent(g9,g-4)
    c: PointOnObject(g10,g8)
    c: PointOnObject(g11,g8)
    c: PointOnObject(g12,g2)
    c: PointOnObject(g13,g-3)
    c: PointOnObject(g13,g9)
    c: PointOnObject(g12,g9)
    c: PointOnObject(g10,g-3)
    c: PointOnObject(g11,g1)
FEATURE [PartDesign::Pad] Pad033
  BaseFeature = -> Pad026
  Direction = (0,-1,2e-16)
  Length = 11
  Length2 = 10
  Profile = -> Sketch075
  ReferenceAxis = -> Sketch075 [N_Axis]
  Refine = true
  Reversed = true
  Suppressed = false
  Type = 0
FEATURE [Sketcher::SketchObject] Sketch076
  ArcFitTolerance = 1e-06
  AttachmentSupport = -> [Pad033]
  ExternalGeometry = -> [Pad033]
  FullyConstrained = true
  MakeInternals = false
  MapMode = 5
  Placement = pos=(0,-122,9.27e-14) rot=(1,0,0;1.5708rad)
  sketch-geometry (2):
    g0: Circle CenterX=24.5 CenterY=6 CenterZ=0 NormalX=0 NormalY=0 NormalZ=1 AngleXU=0 Radius=1.7
    g1: Circle CenterX=59.5 CenterY=6 CenterZ=0 NormalX=0 NormalY=0 NormalZ=1 AngleXU=0 Radius=1.7
  constraints (4):
    c: Coincident(g0,g-3)
    c: Equal(g0,g-3)
    c: Coincident(g1,g-4)
    c: Equal(g1,g-4)
FEATURE [PartDesign::Pocket] Pocket039
  BaseFeature = -> Pad033
  Direction = (0,1,-2e-16)
  Length = 0
  Length2 = 5
  Profile = -> Sketch076
  ReferenceAxis = -> Sketch076 [N_Axis]
  Refine = true
  Suppressed = false
  Type = 3
  UpToFace = -> Pad033 [Face25]
FEATURE [PartDesign::ShapeBinder] CopyPocket039
  TraceSupport = false
FEATURE [PartDesign::Plane] DatumPlane013
  AttachmentSupport = -> [CopyPocket039]
  Length = 134.316
  MapMode = 5
  Placement = pos=(0,1.2e-15,-1.25) rot=(1,0,0;3.14159rad)
  ResizeMode = 0
  Width = 172.316
FEATURE [Sketcher::SketchObject] Sketch077
  ArcFitTolerance = 1e-06
  AttachmentSupport = -> [DatumPlane013]
  ExternalGeometry = -> [CopyPocket039]
  FullyConstrained = true
  MakeInternals = false
  MapMode = 5
  Placement = pos=(0,1.2e-15,-1.25) rot=(1,0,0;3.14159rad)
  sketch-geometry (15):
    g0: Circle CenterX=5 CenterY=79 CenterZ=0 NormalX=0 NormalY=0 NormalZ=1 AngleXU=0 Radius=1.3
    g1: Circle CenterX=79 CenterY=79 CenterZ=0 NormalX=0 NormalY=0 NormalZ=1 AngleXU=0 Radius=1.3
    g2: Circle CenterX=79 CenterY=5 CenterZ=0 NormalX=0 NormalY=0 NormalZ=1 AngleXU=0 Radius=1.3
    g3: Circle CenterX=5 CenterY=5 CenterZ=0 NormalX=0 NormalY=0 NormalZ=1 AngleXU=0 Radius=1.3
    g4: LineSegment StartX=0 StartY=122 StartZ=0 EndX=0 EndY=0 EndZ=0
    g5: LineSegment StartX=0 StartY=0 StartZ=0 EndX=84 EndY=1.2e-15 EndZ=0
    g6: LineSegment StartX=84 StartY=1.2e-15 StartZ=0 EndX=84 EndY=122 EndZ=0
    g7: LineSegment StartX=84 StartY=122 StartZ=0 EndX=74 EndY=122 EndZ=0
    g8: LineSegment StartX=0 StartY=122 StartZ=0 EndX=10 EndY=122 EndZ=0
    g9: LineSegment [constr] StartX=42 StartY=4e-16 StartZ=0 EndX=42 EndY=10 EndZ=0
    g10: LineSegment [constr] StartX=42 StartY=10 StartZ=0 EndX=0 EndY=10 EndZ=0
    g11: LineSegment [constr] StartX=42 StartY=10 StartZ=0 EndX=84 EndY=10 EndZ=0
    g12: LineSegment StartX=10 StartY=122 StartZ=0 EndX=10 EndY=10 EndZ=0
    g13: LineSegment StartX=74 StartY=122 StartZ=0 EndX=74 EndY=10 EndZ=0
    g14: LineSegment StartX=74 StartY=10 StartZ=0 EndX=10 EndY=10 EndZ=0
  constraints (37):
    c: Coincident(g0,g-5)
    c: Coincident(g1,g-6)
    c: Coincident(g2,g-4)
    c: Coincident(g3,g-3)
    c: Diameter(g3) = 2.6
    c: Equal(g2,g1)
    c: Equal(g1,g0)
    c: Equal(g0,g3)
    c: Coincident(g4,g-10)
    c: Coincident(g4,g-1)
    c: Coincident(g5,g4)
    c: Coincident(g5,g-9)
    c: Coincident(g6,g5)
    c: Coincident(g6,g-10)
    c: Distance(g7) = 10
    c: Coincident(g7,g6)
    c: PointOnObject(g7,g-10)
    c: Distance(g8) = 10
    c: Coincident(g8,g4)
    c: PointOnObject(g8,g-10)
    c: Distance(g9) = 10
    c: Symmetric(g5,g5,g9)
    c: Vertical(g9)
    c: Coincident(g10,g9)
    c: PointOnObject(g10,g4)
    c: Horizontal(g10)
    c: Coincident(g11,g9)
    c: PointOnObject(g11,g6)
    c: Horizontal(g11)
    c: Coincident(g12,g8)
    c: PointOnObject(g12,g10)
    c: Vertical(g12)
    c: Coincident(g13,g7)
    c: PointOnObject(g13,g11)
    c: Vertical(g13)
    c: Coincident(g14,g13)
    c: Coincident(g14,g12)
FEATURE [PartDesign::Pad] Pad034
  Direction = (0,0,-1)
  Length = 30
  Length2 = 10
  Placement = pos=(0,1.2e-15,-1.25) rot=(1,0,0;3.14159rad)
  Profile = -> Sketch077
  ReferenceAxis = -> Sketch077 [N_Axis]
  Refine = true
  Suppressed = false
  Type = 0
FEATURE [Sketcher::SketchObject] Sketch078
  ArcFitTolerance = 1e-06
  AttachmentSupport = -> [Pad034]
  ExternalGeometry = -> [Pad034,CopyPocket039]
  FullyConstrained = true
  MakeInternals = false
  MapMode = 5
  Placement = pos=(0,1.2e-15,-1.25) rot=(0.57735,0.57735,-0.57735;4.18879rad)
  sketch-geometry (11):
    g0: LineSegment [constr] StartX=-122 StartY=30 StartZ=0 EndX=-122 EndY=25 EndZ=0
    g1: LineSegment [constr] StartX=-122 StartY=25 StartZ=0 EndX=-117 EndY=25 EndZ=0
    g2: Circle CenterX=-117 CenterY=25 CenterZ=0 NormalX=0 NormalY=0 NormalZ=1 AngleXU=0 Radius=1.3
    g3: LineSegment [constr] StartX=-117 StartY=25 StartZ=0 EndX=-117 EndY=20 EndZ=0
    g4: LineSegment [constr] StartX=-117 StartY=20 StartZ=0 EndX=-117 EndY=15 EndZ=0
    g5: LineSegment [constr] StartX=-117 StartY=15 StartZ=0 EndX=-117 EndY=10 EndZ=0
    g6: LineSegment [constr] StartX=-117 StartY=10 StartZ=0 EndX=-117 EndY=5 EndZ=0
    g7: Circle CenterX=-117 CenterY=20 CenterZ=0 NormalX=0 NormalY=0 NormalZ=1 AngleXU=0 Radius=1.3
    g8: Circle CenterX=-117 CenterY=15 CenterZ=0 NormalX=0 NormalY=0 NormalZ=1 AngleXU=0 Radius=1.3
    g9: Circle CenterX=-117 CenterY=10 CenterZ=0 NormalX=0 NormalY=0 NormalZ=1 AngleXU=0 Radius=1.3
    g10: Circle CenterX=-117 CenterY=5 CenterZ=0 NormalX=0 NormalY=0 NormalZ=1 AngleXU=0 Radius=1.3
  constraints (28):
    c: Distance(g0) = 5
    c: Coincident(g0,g-4)
    c: PointOnObject(g0,g-4)
    c: Distance(g1) = 5
    c: Coincident(g1,g0)
    c: Horizontal(g1)
    c: Diameter(g2) = 2.6
    c: Coincident(g2,g1)
    c: Distance(g3) = 5
    c: Coincident(g3,g1)
    c: Vertical(g3)
    c: Distance(g4) = 5
    c: Coincident(g4,g3)
    c: Vertical(g4)
    c: Distance(g5) = 5
    c: Coincident(g5,g4)
    c: Vertical(g5)
    c: Distance(g6) = 5
    c: Coincident(g6,g5)
    c: Vertical(g6)
    c: Coincident(g7,g3)
    c: Coincident(g8,g4)
    c: Coincident(g9,g5)
    c: Coincident(g10,g6)
    c: Equal(g7,g8)
    c: Equal(g8,g9)
    c: Equal(g9,g10)
    c: Equal(g10,g2)
FEATURE [PartDesign::Pocket] Pocket040
  BaseFeature = -> Pad034
  Direction = (1,0,0)
  Length = 5
  Length2 = 5
  Placement = pos=(0,1.2e-15,-1.25) rot=(1,0,0;3.14159rad)
  Profile = -> Sketch078
  ReferenceAxis = -> Sketch078 [N_Axis]
  Refine = true
  Suppressed = false
  Type = 1
FEATURE [PartDesign::LinearPattern] LinearPattern
  BaseFeature = -> Pocket040
  Direction = -> Sketch078 [H_Axis]
  Length = 95
  Mode = 0
  Occurrences = 20
  Offset = 5
  Originals = -> [Pocket040]
  Placement = pos=(0,1.2e-15,-1.25) rot=(1,0,0;3.14159rad)
  Refine = true
  Suppressed = false
  TransformMode = 0
FEATURE [Sketcher::SketchObject] Sketch079
  ArcFitTolerance = 1e-06
  AttachmentSupport = -> [LinearPattern]
  ExternalGeometry = -> [LinearPattern]
  FullyConstrained = true
  MakeInternals = false
  MapMode = 5
  Placement = pos=(0,1e-15,-1.25) rot=(-1,0,0;1.5708rad)
  sketch-geometry (14):
    g0: LineSegment [constr] StartX=0 StartY=30 StartZ=0 EndX=0 EndY=25 EndZ=0
    g1: LineSegment [constr] StartX=0 StartY=25 StartZ=0 EndX=42 EndY=25 EndZ=0
    g2: LineSegment [constr] StartX=42 StartY=25 StartZ=0 EndX=42 EndY=30 EndZ=0
    g3: LineSegment [constr] StartX=42 StartY=30 StartZ=0 EndX=0 EndY=30 EndZ=0
    g4: Circle CenterX=42 CenterY=25 CenterZ=0 NormalX=0 NormalY=0 NormalZ=1 AngleXU=0 Radius=1.3
    g5: LineSegment [constr] StartX=42 StartY=25 StartZ=0 EndX=42 EndY=20 EndZ=0
    g6: LineSegment [constr] StartX=42 StartY=20 StartZ=0 EndX=42 EndY=15 EndZ=0
    g7: LineSegment [constr] StartX=42 StartY=15 StartZ=0 EndX=42 EndY=10 EndZ=0
    g8: LineSegment [constr] StartX=42 StartY=10 StartZ=0 EndX=42 EndY=5 EndZ=0
    g9: Circle CenterX=42 CenterY=20 CenterZ=0 NormalX=0 NormalY=0 NormalZ=1 AngleXU=0 Radius=1.3
    g10: Circle CenterX=42 CenterY=15 CenterZ=0 NormalX=0 NormalY=0 NormalZ=1 AngleXU=0 Radius=1.3
    g11: Circle CenterX=42 CenterY=10 CenterZ=0 NormalX=0 NormalY=0 NormalZ=1 AngleXU=0 Radius=1.3
    g12: Circle CenterX=42 CenterY=5 CenterZ=0 NormalX=0 NormalY=0 NormalZ=1 AngleXU=0 Radius=1.3
    g13: GeomPoint X=42 Y=30 Z=0
  constraints (33):
    c: Coincident(g0,g1)
    c: Coincident(g1,g2)
    c: Coincident(g2,g3)
    c: Coincident(g3,g0)
    c: Vertical(g0)
    c: Vertical(g2)
    c: Horizontal(g1)
    c: Distance(g1,g3) = 5
    c: Coincident(g0,g-4)
    c: Coincident(g4,g1)
    c: Diameter(g4) = 2.6
    c: Distance(g5) = 5
    c: Coincident(g5,g1)
    c: Vertical(g5)
    c: Distance(g6) = 5
    c: Coincident(g6,g5)
    c: Vertical(g6)
    c: Distance(g7) = 5
    c: Coincident(g7,g6)
    c: Parallel(g7,g6)
    c: Distance(g8) = 5
    c: Coincident(g8,g7)
    c: Vertical(g8)
    c: Coincident(g9,g5)
    c: Coincident(g10,g6)
    c: Coincident(g11,g7)
    c: Coincident(g12,g8)
    c: Equal(g11,g12)
    c: Equal(g12,g10)
    c: Equal(g10,g9)
    c: Equal(g9,g4)
    c: Symmetric(g-3,g-3,g13)
    c: Coincident(g2,g13)
FEATURE [PartDesign::Pocket] Pocket041
  BaseFeature = -> LinearPattern
  Direction = (0,-1,-2e-16)
  Length = 5
  Length2 = 5
  Placement = pos=(0,1.2e-15,-1.25) rot=(1,0,0;3.14159rad)
  Profile = -> Sketch079
  ReferenceAxis = -> Sketch079 [N_Axis]
  Refine = true
  Suppressed = false
  Type = 1
FEATURE [PartDesign::LinearPattern] LinearPattern001
  BaseFeature = -> Pocket041
  Direction = -> Sketch079 [H_Axis]
  Length = 30
  Mode = 0
  Occurrences = 7
  Offset = 5
  Originals = -> [Pocket041]
  Placement = pos=(0,1.2e-15,-1.25) rot=(1,0,0;3.14159rad)
  Refine = true
  Suppressed = false
  TransformMode = 0
FEATURE [PartDesign::LinearPattern] LinearPattern002
  BaseFeature = -> LinearPattern001
  Direction = -> Sketch079 [H_Axis]
  Length = 30
  Mode = 0
  Occurrences = 7
  Offset = 5
  Originals = -> [Pocket041]
  Placement = pos=(0,1.2e-15,-1.25) rot=(1,0,0;3.14159rad)
  Refine = true
  Reversed = true
  Suppressed = false
  TransformMode = 0
FEATURE [PartDesign::Chamfer] Chamfer018
  Angle = 45
  Base = -> LinearPattern002 [Edge4,Edge128]
  BaseFeature = -> LinearPattern002
  ChamferType = 0
  FlipDirection = false
  Placement = pos=(0,1.2e-15,-1.25) rot=(1,0,0;3.14159rad)
  Refine = true
  Size = 5
  Size2 = 1
  SupportTransform = false
  Suppressed = false
  UseAllEdges = false
FEATURE [PartDesign::Chamfer] Chamfer019
  Angle = 45
  Base = -> Chamfer018 [Edge472,Edge573,Edge120,Edge3]
  BaseFeature = -> Chamfer018
  ChamferType = 0
  FlipDirection = false
  Placement = pos=(0,1.2e-15,-1.25) rot=(1,0,0;3.14159rad)
  Refine = true
  Size = 3
  Size2 = 1
  SupportTransform = false
  Suppressed = false
  UseAllEdges = false
FEATURE [PartDesign::Body] Body012  label="Motorised Stage Base"
  AllowCompound = false
  Group = -> [DatumPlane013,CopyPocket039,Sketch077,Pad034,Sketch078,Pocket040,LinearPattern,Sketch079,Pocket041,LinearPattern001,LinearPattern002,Chamfer018,Chamfer019]
  Origin = -> Origin012
  Tip = -> Chamfer019
FEATURE [PartDesign::ShapeBinder] CopyChamfer019
  Placement = pos=(0,1.2e-15,-1.25) rot=(1,0,0;3.14159rad)
  TraceSupport = false
FEATURE [PartDesign::Plane] DatumPlane014
  AttachmentSupport = -> [CopyChamfer019]
  Length = 84.7279
  MapMode = 5
  Placement = pos=(84,1.2e-15,-1.25) rot=(0.57735,-0.57735,0.57735;4.18879rad)
  ResizeMode = 0
  Width = 68.9779
FEATURE [Sketcher::SketchObject] Sketch080
  ArcFitTolerance = 1e-06
  AttachmentSupport = -> [DatumPlane014]
  ExternalGeometry = -> [CopyChamfer019]
  FullyConstrained = true
  MakeInternals = false
  MapMode = 5
  Placement = pos=(84,1.2e-15,-1.25) rot=(0.57735,-0.57735,0.57735;4.18879rad)
  sketch-geometry (10):
    g0: LineSegment [constr] StartX=22 StartY=25 StartZ=0 EndX=22 EndY=30 EndZ=0
    g1: LineSegment [constr] StartX=42 StartY=25 StartZ=0 EndX=42 EndY=30 EndZ=0
    g2: LineSegment [constr] StartX=42 StartY=30 StartZ=0 EndX=47 EndY=30 EndZ=0
    g3: LineSegment [constr] StartX=22 StartY=30 StartZ=0 EndX=17 EndY=30 EndZ=0
    g4: LineSegment StartX=17 StartY=30 StartZ=0 EndX=17 EndY=22.5 EndZ=0
    g5: LineSegment StartX=17 StartY=22.5 StartZ=0 EndX=47 EndY=22.5 EndZ=0
    g6: LineSegment StartX=47 StartY=22.5 StartZ=0 EndX=47 EndY=30 EndZ=0
    g7: LineSegment StartX=47 StartY=30 StartZ=0 EndX=17 EndY=30 EndZ=0
    g8: Circle CenterX=22 CenterY=25 CenterZ=0 NormalX=0 NormalY=0 NormalZ=1 AngleXU=0 Radius=1.5
    g9: Circle CenterX=42 CenterY=25 CenterZ=0 NormalX=0 NormalY=0 NormalZ=1 AngleXU=0 Radius=1.5
  constraints (26):
    c: Coincident(g0,g-3)
    c: PointOnObject(g0,g-5)
    c: Vertical(g0)
    c: Coincident(g1,g-4)
    c: PointOnObject(g1,g-5)
    c: Vertical(g1)
    c: Distance(g2) = 5
    c: Coincident(g2,g1)
    c: PointOnObject(g2,g-5)
    c: Distance(g3) = 5
    c: Coincident(g3,g0)
    c: PointOnObject(g3,g-5)
    c: Distance(g4) = 7.5
    c: Vertical(g4)
    c: Coincident(g4,g3)
    c: Coincident(g4,g5)
    c: Horizontal(g5)
    c: Coincident(g5,g6)
    c: Coincident(g6,g2)
    c: Vertical(g6)
    c: Coincident(g6,g7)
    c: Coincident(g7,g3)
    c: Diameter(g8) = 3
    c: Coincident(g8,g0)
    c: Diameter(g9) = 3
    c: Coincident(g9,g1)
FEATURE [PartDesign::Pad] Pad035
  Direction = (1,0,0)
  Length = 3
  Length2 = 10
  Placement = pos=(84,1.2e-15,-1.25) rot=(0.57735,-0.57735,0.57735;4.18879rad)
  Profile = -> Sketch080
  ReferenceAxis = -> Sketch080 [N_Axis]
  Refine = true
  Suppressed = false
  Type = 0
FEATURE [Sketcher::SketchObject] Sketch081
  ArcFitTolerance = 1e-06
  AttachmentSupport = -> [Pad035]
  ExternalGeometry = -> [Pad035]
  FullyConstrained = true
  MakeInternals = false
  MapMode = 5
  Placement = pos=(87,1.2e-15,-1.25) rot=(0.57735,-0.57735,0.57735;4.18879rad)
  sketch-geometry (8):
    g0: ArcOfCircle CenterX=22 CenterY=25 CenterZ=0 NormalX=0 NormalY=0 NormalZ=1 AngleXU=0 Radius=3 StartAngle=5.29807 EndAngle=10.4099
    g1: ArcOfCircle CenterX=42 CenterY=25 CenterZ=0 NormalX=0 NormalY=0 NormalZ=1 AngleXU=0 Radius=3 StartAngle=5.29807 EndAngle=10.4099
    g2: LineSegment StartX=47 StartY=22.5 StartZ=0 EndX=43.6583 EndY=22.5 EndZ=0
    g3: LineSegment StartX=40.3417 StartY=22.5 StartZ=0 EndX=23.6583 EndY=22.5 EndZ=0
    g4: LineSegment StartX=20.3417 StartY=22.5 StartZ=0 EndX=17 EndY=22.5 EndZ=0
    g5: LineSegment StartX=17 StartY=22.5 StartZ=0 EndX=17 EndY=30 EndZ=0
    g6: LineSegment StartX=17 StartY=30 StartZ=0 EndX=47 EndY=30 EndZ=0
    g7: LineSegment StartX=47 StartY=30 StartZ=0 EndX=47 EndY=22.5 EndZ=0
  constraints (22):
    c: Diameter(g0) = 6
    c: Coincident(g0,g-3)
    c: Diameter(g1) = 6
    c: Coincident(g1,g-4)
    c: Coincident(g2,g-6)
    c: Coincident(g4,g-7)
    c: PointOnObject(g0,g4)
    c: PointOnObject(g1,g3)
    c: Coincident(g2,g1)
    c: PointOnObject(g3,g1)
    c: Coincident(g3,g0)
    c: PointOnObject(g4,g0)
    c: Horizontal(g0,g1)
    c: PointOnObject(g1,g-6)
    c: PointOnObject(g0,g-6)
    c: PointOnObject(g1,g-6)
    c: Coincident(g5,g4)
    c: Coincident(g5,g-8)
    c: Coincident(g6,g5)
    c: Coincident(g6,g-8)
    c: Coincident(g7,g6)
    c: Coincident(g7,g2)
FEATURE [PartDesign::Pad] Pad036
  BaseFeature = -> Pad035
  Direction = (1,0,0)
  Length = 4
  Length2 = 10
  Placement = pos=(84,1.2e-15,-1.25) rot=(0.57735,-0.57735,0.57735;4.18879rad)
  Profile = -> Sketch081
  ReferenceAxis = -> Sketch081 [N_Axis]
  Refine = true
  Suppressed = false
  Type = 0
FEATURE [Sketcher::SketchObject] Sketch082
  ArcFitTolerance = 1e-06
  AttachmentSupport = -> [Pad036]
  ExternalGeometry = -> [Pad036]
  FullyConstrained = true
  MakeInternals = false
  MapMode = 5
  Placement = pos=(91,1.2e-15,-1.25) rot=(0.57735,-0.57735,0.57735;4.18879rad)
  sketch-geometry (10):
    g0: GeomPoint [constr] X=17 Y=26.25 Z=0
    g1: LineSegment [constr] StartX=17 StartY=26.25 StartZ=0 EndX=47 EndY=26.25 EndZ=0
    g2: ArcOfCircle CenterX=22 CenterY=25 CenterZ=0 NormalX=0 NormalY=0 NormalZ=1 AngleXU=0 Radius=3 StartAngle=0.429775 EndAngle=2.71182
    g3: ArcOfCircle CenterX=42 CenterY=25 CenterZ=0 NormalX=0 NormalY=0 NormalZ=1 AngleXU=0 Radius=3 StartAngle=0.429775 EndAngle=2.71182
    g4: LineSegment StartX=17 StartY=26.25 StartZ=0 EndX=19.2728 EndY=26.25 EndZ=0
    g5: LineSegment StartX=17 StartY=26.25 StartZ=0 EndX=17 EndY=30 EndZ=0
    g6: LineSegment StartX=17 StartY=30 StartZ=0 EndX=47 EndY=30 EndZ=0
    g7: LineSegment StartX=47 StartY=30 StartZ=0 EndX=47 EndY=26.25 EndZ=0
    g8: LineSegment StartX=44.7272 StartY=26.25 StartZ=0 EndX=47 EndY=26.25 EndZ=0
    g9: LineSegment StartX=24.7272 StartY=26.25 StartZ=0 EndX=39.2728 EndY=26.25 EndZ=0
  constraints (23):
    c: Symmetric(g-3,g-3,g0)
    c: Coincident(g1,g0)
    c: Symmetric(g-5,g-5,g1)
    c: Coincident(g2,g-6)
    c: Equal(g2,g-6)
    c: Coincident(g3,g-7)
    c: Equal(g3,g-7)
    c: Coincident(g4,g0)
    c: Coincident(g8,g1)
    c: Coincident(g5,g0)
    c: Coincident(g5,g-4)
    c: Coincident(g6,g5)
    c: Coincident(g6,g-5)
    c: Coincident(g7,g6)
    c: Coincident(g7,g1)
    c: PointOnObject(g3,g1)
    c: PointOnObject(g3,g1)
    c: PointOnObject(g2,g1)
    c: PointOnObject(g2,g1)
    c: Coincident(g9,g3)
    c: Coincident(g9,g2)
    c: Coincident(g4,g2)
    c: Coincident(g8,g3)
FEATURE [PartDesign::Pad] Pad037
  BaseFeature = -> Pad036
  Direction = (1,0,0)
  Length = 10
  Length2 = 10
  Placement = pos=(84,1.2e-15,-1.25) rot=(0.57735,-0.57735,0.57735;4.18879rad)
  Profile = -> Sketch082
  ReferenceAxis = -> Sketch082 [N_Axis]
  Refine = true
  Suppressed = false
  Type = 0
FEATURE [Sketcher::SketchObject] Sketch083
  ArcFitTolerance = 1e-06
  AttachmentSupport = -> [Pad037]
  ExternalGeometry = -> [Pad037]
  FullyConstrained = true
  MakeInternals = false
  MapMode = 5
  Placement = pos=(84,-5.1e-15,-27.5) rot=(0,0,-1;1.5708rad)
  sketch-geometry (7):
    g0: LineSegment [constr] StartX=17 StartY=17 StartZ=0 EndX=17 EndY=12 EndZ=0
    g1: LineSegment [constr] StartX=17 StartY=12 StartZ=0 EndX=47 EndY=12 EndZ=0
    g2: GeomPoint [constr] X=32 Y=12 Z=0
    g3: LineSegment [constr] StartX=32 StartY=12 StartZ=0 EndX=42 EndY=12 EndZ=0
    g4: LineSegment [constr] StartX=32 StartY=12 StartZ=0 EndX=22 EndY=12 EndZ=0
    g5: Circle CenterX=22 CenterY=12 CenterZ=0 NormalX=0 NormalY=0 NormalZ=1 AngleXU=0 Radius=3
    g6: Circle CenterX=42 CenterY=12 CenterZ=0 NormalX=0 NormalY=0 NormalZ=1 AngleXU=0 Radius=3
  constraints (15):
    c: Coincident(g0,g-5)
    c: Symmetric(g-5,g-5,g0)
    c: Coincident(g1,g0)
    c: Symmetric(g-7,g-7,g1)
    c: Symmetric(g1,g1,g2)
    c: Distance(g3) = 10
    c: Coincident(g3,g2)
    c: PointOnObject(g3,g1)
    c: Distance(g4) = 10
    c: Coincident(g4,g2)
    c: PointOnObject(g4,g1)
    c: Diameter(g5) = 6
    c: Coincident(g5,g4)
    c: Diameter(g6) = 6
    c: Coincident(g6,g3)
FEATURE [PartDesign::Pocket] Pocket042
  BaseFeature = -> Pad037
  Direction = (0,0,-1)
  Length = 2
  Length2 = 5
  Placement = pos=(84,1.2e-15,-1.25) rot=(0.57735,-0.57735,0.57735;4.18879rad)
  Profile = -> Sketch083
  ReferenceAxis = -> Sketch083 [N_Axis]
  Refine = true
  Suppressed = false
  Type = 0
FEATURE [Sketcher::SketchObject] Sketch084
  ArcFitTolerance = 1e-06
  AttachmentSupport = -> [Pocket042]
  ExternalGeometry = -> [Pocket042]
  FullyConstrained = true
  MakeInternals = false
  MapMode = 5
  Placement = pos=(84,1.2e-15,-29.5) rot=(0,0,-1;1.5708rad)
  sketch-geometry (2):
    g0: Circle CenterX=22 CenterY=12 CenterZ=0 NormalX=0 NormalY=0 NormalZ=1 AngleXU=0 Radius=1.5
    g1: Circle CenterX=42 CenterY=12 CenterZ=0 NormalX=0 NormalY=0 NormalZ=1 AngleXU=0 Radius=1.5
  constraints (4):
    c: Diameter(g0) = 3
    c: Coincident(g0,g-3)
    c: Diameter(g1) = 3
    c: Coincident(g1,g-4)
FEATURE [PartDesign::Pocket] Pocket043
  BaseFeature = -> Pocket042
  Direction = (0,0,-1)
  Length = 4
  Length2 = 5
  Placement = pos=(84,1.2e-15,-1.25) rot=(0.57735,-0.57735,0.57735;4.18879rad)
  Profile = -> Sketch084
  ReferenceAxis = -> Sketch084 [N_Axis]
  Refine = true
  Suppressed = false
  Type = 0
FEATURE [PartDesign::Chamfer] Chamfer020
  Angle = 45
  Base = -> Pocket043 [Edge10,Edge23]
  BaseFeature = -> Pocket043
  ChamferType = 0
  FlipDirection = false
  Placement = pos=(84,1.2e-15,-1.25) rot=(0.57735,-0.57735,0.57735;4.18879rad)
  Refine = true
  Size = 5
  Size2 = 1
  SupportTransform = false
  Suppressed = false
  UseAllEdges = false
FEATURE [Sketcher::SketchObject] Sketch085
  ArcFitTolerance = 1e-06
  AttachmentSupport = -> [Chamfer020]
  ExternalGeometry = -> [Chamfer020]
  FullyConstrained = true
  MakeInternals = false
  MapMode = 5
  Placement = pos=(84,-5.1e-15,-27.5) rot=(0,0,-1;1.5708rad)
  sketch-geometry (3):
    g0: GeomPoint X=32 Y=17 Z=0
    g1: LineSegment [constr] StartX=32 StartY=17 StartZ=0 EndX=32 EndY=12 EndZ=0
    g2: Circle CenterX=32 CenterY=12 CenterZ=0 NormalX=0 NormalY=0 NormalZ=1 AngleXU=0 Radius=1.5
  constraints (6):
    c: Symmetric(g-3,g-3,g0)
    c: Distance(g1) = 5
    c: Coincident(g1,g0)
    c: Perpendicular(g-3,g1)
    c: Diameter(g2) = 3
    c: Coincident(g2,g1)
FEATURE [PartDesign::Pocket] Pocket044
  BaseFeature = -> Chamfer020
  Direction = (0,0,-1)
  Length = 5
  Length2 = 5
  Placement = pos=(84,1.2e-15,-1.25) rot=(0.57735,-0.57735,0.57735;4.18879rad)
  Profile = -> Sketch085
  ReferenceAxis = -> Sketch085 [N_Axis]
  Refine = true
  Suppressed = false
  Type = 0
FEATURE [PartDesign::Chamfer] Chamfer021
  Angle = 45
  Base = -> Pocket044 [Edge30,Edge26,Edge16]
  BaseFeature = -> Pocket044
  ChamferType = 0
  FlipDirection = false
  Placement = pos=(84,1.2e-15,-1.25) rot=(0.57735,-0.57735,0.57735;4.18879rad)
  Refine = true
  Size = 3.74
  Size2 = 1
  SupportTransform = false
  Suppressed = false
  UseAllEdges = false
FEATURE [PartDesign::Chamfer] Chamfer022
  Angle = 45
  Base = -> Chamfer021 [Edge70]
  BaseFeature = -> Chamfer021
  ChamferType = 0
  FlipDirection = false
  Placement = pos=(84,1.2e-15,-1.25) rot=(0.57735,-0.57735,0.57735;4.18879rad)
  Refine = true
  Size = 2
  Size2 = 1
  SupportTransform = false
  Suppressed = false
  UseAllEdges = false
FEATURE [PartDesign::Body] Body013  label="5mm grid boltdown"
  AllowCompound = false
  Group = -> [DatumPlane014,CopyChamfer019,Sketch080,Pad035,Sketch081,Pad036,Sketch082,Pad037,Sketch083,Pocket042,Sketch084,Pocket043,Chamfer020,Sketch085,Pocket044,Chamfer021,Chamfer022]
  Origin = -> Origin013
  Tip = -> Chamfer022
FEATURE [Sketcher::SketchObject] Sketch086
  ArcFitTolerance = 1e-06
  AttachmentSupport = -> [Pocket025]
  ExternalGeometry = -> [Pocket025]
  FullyConstrained = true
  MakeInternals = false
  MapMode = 5
  Placement = pos=(84,-84,-1.80021e-08) rot=(0.707107,0,0.707107;3.14159rad)
  sketch-geometry (7):
    g0: LineSegment [constr] StartX=27.3536 StartY=-1.42e-14 StartZ=0 EndX=27.3536 EndY=-5 EndZ=0
    g1: LineSegment [constr] StartX=27.3536 StartY=-5 StartZ=0 EndX=22.3536 EndY=-5 EndZ=0
    g2: LineSegment [constr] StartX=22.3536 StartY=-5 StartZ=0 EndX=17.3536 EndY=-5 EndZ=0
    g3: LineSegment [constr] StartX=17.3536 StartY=-5 StartZ=0 EndX=12.3536 EndY=-5 EndZ=0
    g4: Circle CenterX=12.3536 CenterY=-5 CenterZ=0 NormalX=0 NormalY=0 NormalZ=1 AngleXU=0 Radius=1.3
    g5: Circle CenterX=17.3536 CenterY=-5 CenterZ=0 NormalX=0 NormalY=0 NormalZ=1 AngleXU=0 Radius=1.3
    g6: Circle CenterX=22.3536 CenterY=-5 CenterZ=0 NormalX=0 NormalY=0 NormalZ=1 AngleXU=0 Radius=1.3
  constraints (18):
    c: Distance(g0) = 5
    c: PointOnObject(g0,g-4)
    c: Coincident(g0,g-5)
    c: Distance(g1) = 5
    c: Horizontal(g1)
    c: Coincident(g1,g0)
    c: Distance(g2) = 5
    c: Coincident(g2,g1)
    c: Horizontal(g2)
    c: Distance(g3) = 5
    c: Coincident(g3,g2)
    c: Horizontal(g3)
    c: Diameter(g4) = 2.6
    c: Coincident(g4,g3)
    c: Diameter(g5) = 2.6
    c: Coincident(g5,g2)
    c: Diameter(g6) = 2.6
    c: Coincident(g6,g1)
FEATURE [PartDesign::Pocket] Pocket045
  BaseFeature = -> Pocket025
  Direction = (-1,0,2.14311e-10)
  Length = 5
  Length2 = 5
  Placement = pos=(0,-84,2e-15) rot=(1,0,0;1.5708rad)
  Profile = -> Sketch086
  ReferenceAxis = -> Sketch086 [N_Axis]
  Refine = true
  Suppressed = false
  Type = 0
FEATURE [Sketcher::SketchObject] Sketch087
  ArcFitTolerance = 1e-06
  AttachmentSupport = -> [Pocket045]
  ExternalGeometry = -> [Pocket045]
  FullyConstrained = true
  MakeInternals = false
  MapMode = 5
  Placement = pos=(-1.2282e-09,-84,2e-15) rot=(-0.707107,0,0.707107;3.14159rad)
  sketch-geometry (7):
    g0: LineSegment [constr] StartX=-27.3536 StartY=-1.42e-14 StartZ=0 EndX=-27.3536 EndY=-5 EndZ=0
    g1: LineSegment [constr] StartX=-27.3536 StartY=-5 StartZ=0 EndX=-22.3536 EndY=-5 EndZ=0
    g2: LineSegment [constr] StartX=-22.3536 StartY=-5 StartZ=0 EndX=-17.3536 EndY=-5 EndZ=0
    g3: LineSegment [constr] StartX=-17.3536 StartY=-5 StartZ=0 EndX=-12.3536 EndY=-5 EndZ=0
    g4: Circle CenterX=-22.3536 CenterY=-5 CenterZ=0 NormalX=0 NormalY=0 NormalZ=1 AngleXU=0 Radius=1.3
    g5: Circle CenterX=-17.3536 CenterY=-5 CenterZ=0 NormalX=0 NormalY=0 NormalZ=1 AngleXU=0 Radius=1.3
    g6: Circle CenterX=-12.3536 CenterY=-5 CenterZ=0 NormalX=0 NormalY=0 NormalZ=1 AngleXU=0 Radius=1.3
  constraints (18):
    c: Distance(g0) = 5
    c: Coincident(g0,g-3)
    c: PointOnObject(g0,g-3)
    c: Distance(g1) = 5
    c: Coincident(g1,g0)
    c: Horizontal(g1)
    c: Distance(g2) = 5
    c: Coincident(g2,g1)
    c: Horizontal(g2)
    c: Distance(g3) = 5
    c: Coincident(g3,g2)
    c: Horizontal(g3)
    c: Diameter(g4) = 2.6
    c: Coincident(g4,g1)
    c: Diameter(g5) = 2.6
    c: Coincident(g5,g2)
    c: Diameter(g6) = 2.6
    c: Coincident(g6,g3)
FEATURE [PartDesign::Pocket] Pocket046
  BaseFeature = -> Pocket045
  Direction = (1,0,-2.14311e-10)
  Length = 5
  Length2 = 5
  Placement = pos=(0,-84,2e-15) rot=(1,0,0;1.5708rad)
  Profile = -> Sketch087
  ReferenceAxis = -> Sketch087 [N_Axis]
  Refine = true
  Suppressed = false
  Type = 0
FEATURE [Sketcher::SketchObject] Sketch088
  ArcFitTolerance = 1e-06
  AttachmentSupport = -> [Pocket046]
  ExternalGeometry = -> [Pocket046]
  FullyConstrained = true
  MakeInternals = false
  MapMode = 5
  Placement = pos=(84,-84,-1.80021e-08) rot=(0.707107,0,0.707107;3.14159rad)
  sketch-geometry (7):
    g0: LineSegment [constr] StartX=27.3536 StartY=-84 StartZ=0 EndX=27.3536 EndY=-79 EndZ=0
    g1: LineSegment [constr] StartX=27.3536 StartY=-79 StartZ=0 EndX=22.3536 EndY=-79 EndZ=0
    g2: LineSegment [constr] StartX=22.3536 StartY=-79 StartZ=0 EndX=17.3536 EndY=-79 EndZ=0
    g3: LineSegment [constr] StartX=17.3536 StartY=-79 StartZ=0 EndX=12.3536 EndY=-79 EndZ=0
    g4: Circle CenterX=12.3536 CenterY=-79 CenterZ=0 NormalX=0 NormalY=0 NormalZ=1 AngleXU=0 Radius=1.3
    g5: Circle CenterX=17.3536 CenterY=-79 CenterZ=0 NormalX=0 NormalY=0 NormalZ=1 AngleXU=0 Radius=1.3
    g6: Circle CenterX=22.3536 CenterY=-79 CenterZ=0 NormalX=0 NormalY=0 NormalZ=1 AngleXU=0 Radius=1.3
  constraints (18):
    c: Distance(g0) = 5
    c: Coincident(g0,g-3)
    c: PointOnObject(g0,g-3)
    c: Distance(g1) = 5
    c: Coincident(g1,g0)
    c: Horizontal(g1)
    c: Distance(g2) = 5
    c: Coincident(g2,g1)
    c: Horizontal(g2)
    c: Distance(g3) = 5
    c: Coincident(g3,g2)
    c: Horizontal(g3)
    c: Diameter(g4) = 2.6
    c: Coincident(g4,g3)
    c: Diameter(g5) = 2.6
    c: Coincident(g5,g2)
    c: Diameter(g6) = 2.6
    c: Coincident(g6,g1)
FEATURE [PartDesign::Pocket] Pocket047
  BaseFeature = -> Pocket046
  Direction = (-1,0,2.14311e-10)
  Length = 5
  Length2 = 5
  Placement = pos=(0,-84,2e-15) rot=(1,0,0;1.5708rad)
  Profile = -> Sketch088
  ReferenceAxis = -> Sketch088 [N_Axis]
  Refine = true
  Suppressed = false
  Type = 0
FEATURE [Sketcher::SketchObject] Sketch089
  ArcFitTolerance = 1e-06
  AttachmentSupport = -> [Pocket047]
  ExternalGeometry = -> [Pocket047]
  FullyConstrained = true
  MakeInternals = false
  MapMode = 5
  Placement = pos=(-1.2282e-09,-84,2e-15) rot=(-0.707107,0,0.707107;3.14159rad)
  sketch-geometry (7):
    g0: LineSegment [constr] StartX=-27.3536 StartY=-84 StartZ=0 EndX=-27.3536 EndY=-79 EndZ=0
    g1: LineSegment [constr] StartX=-27.3536 StartY=-79 StartZ=0 EndX=-22.3536 EndY=-79 EndZ=0
    g2: LineSegment [constr] StartX=-22.3536 StartY=-79 StartZ=0 EndX=-17.3536 EndY=-79 EndZ=0
    g3: LineSegment [constr] StartX=-17.3536 StartY=-79 StartZ=0 EndX=-12.3536 EndY=-79 EndZ=0
    g4: Circle CenterX=-22.3536 CenterY=-79 CenterZ=0 NormalX=0 NormalY=0 NormalZ=1 AngleXU=0 Radius=1.3
    g5: Circle CenterX=-17.3536 CenterY=-79 CenterZ=0 NormalX=0 NormalY=0 NormalZ=1 AngleXU=0 Radius=1.3
    g6: Circle CenterX=-12.3536 CenterY=-79 CenterZ=0 NormalX=0 NormalY=0 NormalZ=1 AngleXU=0 Radius=1.3
  constraints (18):
    c: Distance(g0) = 5
    c: Coincident(g0,g-3)
    c: PointOnObject(g0,g-3)
    c: Distance(g1) = 5
    c: Coincident(g1,g0)
    c: Horizontal(g1)
    c: Distance(g2) = 5
    c: Coincident(g2,g1)
    c: Horizontal(g2)
    c: Distance(g3) = 5
    c: Coincident(g3,g2)
    c: Horizontal(g3)
    c: Diameter(g4) = 2.6
    c: Coincident(g4,g1)
    c: Diameter(g5) = 2.6
    c: Coincident(g5,g2)
    c: Diameter(g6) = 2.6
    c: Coincident(g6,g3)
FEATURE [PartDesign::Pocket] Pocket048
  BaseFeature = -> Pocket047
  Direction = (1,0,-2.14311e-10)
  Length = 5
  Length2 = 5
  Placement = pos=(0,-84,2e-15) rot=(1,0,0;1.5708rad)
  Profile = -> Sketch089
  ReferenceAxis = -> Sketch089 [N_Axis]
  Refine = true
  Suppressed = false
  Type = 0
FEATURE [PartDesign::Body] Body002  label="Upper"
  AllowCompound = false
  Group = -> [ShapeBinder001,DatumPlane004,CopyFillet001,Sketch008,Pad006,Sketch009,Pocket001,Sketch010,Pocket002,Sketch011,Pocket003,Sketch012,Pocket004,Sketch013,Pocket005,Sketch030,Pad016,Sketch031,Pocket011,Sketch037,Pocket015,Sketch039,Pocket017,Sketch050,Pocket023,Sketch051,Pocket024,Sketch052,Pad023,Sketch053,Pocket025,Sketch086,Pocket045,Sketch087,Pocket046,Sketch088,Pocket047,Sketch089,Pocket048]
  Origin = -> Origin002
  Placement = pos=(0,-27,0) rot=(0,0,1;0rad)
  Tip = -> Pocket048
FEATURE [Sketcher::SketchObject] Sketch090
  ArcFitTolerance = 1e-06
  AttachmentSupport = -> [Pocket039]
  ExternalGeometry = -> [Pocket039]
  FullyConstrained = true
  MakeInternals = false
  MapMode = 5
  Placement = pos=(0,-4e-15,5) rot=(0,0,1;0rad)
  sketch-geometry (14):
    g0: LineSegment [constr] StartX=0 StartY=-122 StartZ=0 EndX=0 EndY=-117 EndZ=0
    g1: LineSegment [constr] StartX=84 StartY=-122 StartZ=0 EndX=84 EndY=-117 EndZ=0
    g2: LineSegment [constr] StartX=84 StartY=-117 StartZ=0 EndX=79 EndY=-117 EndZ=0
    g3: LineSegment [constr] StartX=79 StartY=-117 StartZ=0 EndX=74 EndY=-117 EndZ=0
    g4: LineSegment [constr] StartX=74 StartY=-117 StartZ=0 EndX=69 EndY=-117 EndZ=0
    g5: LineSegment [constr] StartX=0 StartY=-117 StartZ=0 EndX=5 EndY=-117 EndZ=0
    g6: LineSegment [constr] StartX=5 StartY=-117 StartZ=0 EndX=10 EndY=-117 EndZ=0
    g7: LineSegment [constr] StartX=10 StartY=-117 StartZ=0 EndX=15 EndY=-117 EndZ=0
    g8: Circle CenterX=15 CenterY=-117 CenterZ=0 NormalX=0 NormalY=0 NormalZ=1 AngleXU=0 Radius=1.3
    g9: Circle CenterX=10 CenterY=-117 CenterZ=0 NormalX=0 NormalY=0 NormalZ=1 AngleXU=0 Radius=1.3
    g10: Circle CenterX=5 CenterY=-117 CenterZ=0 NormalX=0 NormalY=0 NormalZ=1 AngleXU=0 Radius=1.3
    g11: Circle CenterX=69 CenterY=-117 CenterZ=0 NormalX=0 NormalY=0 NormalZ=1 AngleXU=0 Radius=1.3
    g12: Circle CenterX=74 CenterY=-117 CenterZ=0 NormalX=0 NormalY=0 NormalZ=1 AngleXU=0 Radius=1.3
    g13: Circle CenterX=79 CenterY=-117 CenterZ=0 NormalX=0 NormalY=0 NormalZ=1 AngleXU=0 Radius=1.3
  constraints (36):
    c: Distance(g0) = 5
    c: Coincident(g0,g-6)
    c: PointOnObject(g0,g-6)
    c: Distance(g1) = 5
    c: Coincident(g1,g-4)
    c: PointOnObject(g1,g-4)
    c: Distance(g2) = 5
    c: Coincident(g2,g1)
    c: Horizontal(g2)
    c: Distance(g3) = 5
    c: Coincident(g3,g2)
    c: Horizontal(g3)
    c: Distance(g4) = 5
    c: Coincident(g4,g3)
    c: Horizontal(g4)
    c: Distance(g5) = 5
    c: Coincident(g5,g0)
    c: Horizontal(g5)
    c: Distance(g6) = 5
    c: Coincident(g6,g5)
    c: Horizontal(g6)
    c: Distance(g7) = 5
    c: Coincident(g7,g6)
    c: Horizontal(g7)
    c: Coincident(g8,g7)
    c: Coincident(g9,g6)
    c: Diameter(g10) = 2.6
    c: Coincident(g10,g5)
    c: Coincident(g11,g4)
    c: Coincident(g12,g3)
    c: Coincident(g13,g2)
    c: Equal(g10,g9)
    c: Equal(g9,g8)
    c: Equal(g8,g11)
    c: Equal(g11,g12)
    c: Equal(g12,g13)
FEATURE [PartDesign::Pocket] Pocket049
  BaseFeature = -> Pocket039
  Direction = (0,0,-1)
  Length = 5
  Length2 = 5
  Profile = -> Sketch090
  ReferenceAxis = -> Sketch090 [N_Axis]
  Refine = true
  Suppressed = false
  Type = 1
FEATURE [PartDesign::ShapeBinder] CopyPocket049
  TraceSupport = false
FEATURE [PartDesign::Plane] DatumPlane015
  AttachmentSupport = -> [CopyPocket049]
  Length = 134.316
  MapMode = 5
  Placement = pos=(0,-4e-15,5) rot=(0,0,1;0rad)
  ResizeMode = 0
  Width = 172.316
FEATURE [Sketcher::SketchObject] Sketch091
  ArcFitTolerance = 1e-06
  AttachmentSupport = -> [DatumPlane015]
  ExternalGeometry = -> [CopyPocket049]
  FullyConstrained = true
  MakeInternals = false
  MapMode = 5
  Placement = pos=(0,-4e-15,5) rot=(0,0,1;0rad)
  sketch-geometry (6):
    g0: Circle CenterX=79 CenterY=-117 CenterZ=0 NormalX=0 NormalY=0 NormalZ=1 AngleXU=0 Radius=1.5
    g1: Circle CenterX=69 CenterY=-117 CenterZ=0 NormalX=0 NormalY=0 NormalZ=1 AngleXU=0 Radius=1.5
    g2: LineSegment StartX=84 StartY=-122 StartZ=0 EndX=84 EndY=-112 EndZ=0
    g3: LineSegment StartX=84 StartY=-112 StartZ=0 EndX=64 EndY=-112 EndZ=0
    g4: LineSegment StartX=64 StartY=-112 StartZ=0 EndX=64 EndY=-122 EndZ=0
    g5: LineSegment StartX=64 StartY=-122 StartZ=0 EndX=84 EndY=-122 EndZ=0
  constraints (15):
    c: Coincident(g0,g-10)
    c: Coincident(g1,g-8)
    c: Equal(g1,g0)
    c: Coincident(g2,g3)
    c: Coincident(g3,g4)
    c: Coincident(g4,g5)
    c: Coincident(g5,g2)
    c: Vertical(g2)
    c: Vertical(g4)
    c: Horizontal(g3)
    c: Horizontal(g5)
    c: Distance(g2,g4) = 20
    c: Distance(g3,g5) = 10
    c: Coincident(g2,g-4)
    c: Diameter(g1) = 3
FEATURE [PartDesign::Pad] Pad038
  Direction = (0,0,1)
  Length = 3
  Length2 = 10
  Placement = pos=(0,-4e-15,5) rot=(0,0,1;0rad)
  Profile = -> Sketch091
  ReferenceAxis = -> Sketch091 [N_Axis]
  Refine = true
  Suppressed = false
  Type = 0
FEATURE [Sketcher::SketchObject] Sketch092
  ArcFitTolerance = 1e-06
  AttachmentSupport = -> [Pad038]
  ExternalGeometry = -> [Pad038]
  FullyConstrained = true
  MakeInternals = false
  MapMode = 5
  Placement = pos=(0,-4e-15,8) rot=(0,0,1;0rad)
  sketch-geometry (5):
    g0: LineSegment [constr] StartX=64 StartY=-112 StartZ=0 EndX=64 EndY=-119.5 EndZ=0
    g1: LineSegment StartX=64 StartY=-119.5 StartZ=0 EndX=84 EndY=-119.5 EndZ=0
    g2: LineSegment StartX=64 StartY=-119.5 StartZ=0 EndX=64 EndY=-121 EndZ=0
    g3: LineSegment StartX=64 StartY=-121 StartZ=0 EndX=84 EndY=-121 EndZ=0
    g4: LineSegment StartX=84 StartY=-121 StartZ=0 EndX=84 EndY=-119.5 EndZ=0
  constraints (14):
    c: Distance(g0) = 7.5
    c: Coincident(g0,g-4)
    c: Vertical(g0)
    c: Coincident(g1,g0)
    c: PointOnObject(g1,g-5)
    c: Horizontal(g1)
    c: Distance(g2) = 1.5
    c: Coincident(g2,g0)
    c: Vertical(g2)
    c: Coincident(g3,g2)
    c: PointOnObject(g3,g-5)
    c: Horizontal(g3)
    c: Coincident(g4,g3)
    c: Coincident(g4,g1)
FEATURE [PartDesign::Pad] Pad039
  BaseFeature = -> Pad038
  Direction = (0,0,1)
  Length = 23
  Length2 = 10
  Placement = pos=(0,-4e-15,5) rot=(0,0,1;0rad)
  Profile = -> Sketch092
  ReferenceAxis = -> Sketch092 [N_Axis]
  Refine = true
  Suppressed = false
  Type = 0
FEATURE [Sketcher::SketchObject] Sketch093
  ArcFitTolerance = 1e-06
  AttachmentSupport = -> [Pad039]
  ExternalGeometry = -> [Pad039]
  FullyConstrained = true
  MakeInternals = false
  MapMode = 5
  Placement = pos=(0,-121,5) rot=(1,0,0;1.5708rad)
  sketch-geometry (7):
    g0: GeomPoint X=74 Y=26 Z=0
    g1: LineSegment [constr] StartX=74 StartY=26 StartZ=0 EndX=74 EndY=17 EndZ=0
    g2: LineSegment StartX=67 StartY=10 StartZ=0 EndX=81 EndY=10 EndZ=0
    g3: LineSegment StartX=81 StartY=10 StartZ=0 EndX=81 EndY=24 EndZ=0
    g4: LineSegment StartX=81 StartY=24 StartZ=0 EndX=67 EndY=24 EndZ=0
    g5: LineSegment StartX=67 StartY=24 StartZ=0 EndX=67 EndY=10 EndZ=0
    g6: GeomPoint [constr] X=74 Y=17 Z=0
  constraints (16):
    c: Symmetric(g-3,g-3,g0)
    c: Distance(g1) = 9
    c: Coincident(g1,g0)
    c: Vertical(g1)
    c: Coincident(g2,g3)
    c: Coincident(g3,g4)
    c: Coincident(g4,g5)
    c: Coincident(g5,g2)
    c: Horizontal(g2)
    c: Horizontal(g4)
    c: Vertical(g3)
    c: Vertical(g5)
    c: Symmetric(g4,g2,g6)
    c: Distance(g3,g5) = 14
    c: Distance(g2,g4) = 14
    c: Coincident(g6,g1)
FEATURE [PartDesign::Pocket] Pocket050
  BaseFeature = -> Pad039
  Direction = (0,1,-2e-16)
  Length = 5
  Length2 = 5
  Placement = pos=(0,-4e-15,5) rot=(0,0,1;0rad)
  Profile = -> Sketch093
  ReferenceAxis = -> Sketch093 [N_Axis]
  Refine = true
  Suppressed = false
  Type = 1
FEATURE [PartDesign::Pad] Pad040
  BaseFeature = -> Pocket050
  Direction = (0,-1,0)
  Length = 10
  Length2 = 10
  Placement = pos=(0,-4e-15,5) rot=(0,0,1;0rad)
  Profile = -> Pocket050 [Face9]
  Refine = true
  Suppressed = false
  Type = 3
  UpToFace = -> Pocket050 [Face6]
FEATURE [PartDesign::Chamfer] Chamfer023
  Angle = 45
  Base = -> Pad040 [Edge2,Edge1]
  BaseFeature = -> Pad040
  ChamferType = 0
  FlipDirection = false
  Placement = pos=(0,-4e-15,5) rot=(0,0,1;0rad)
  Refine = true
  Size = 5
  Size2 = 1
  SupportTransform = false
  Suppressed = false
  UseAllEdges = false
FEATURE [PartDesign::Body] Body014  label="CherryMXHolder"
  AllowCompound = false
  Group = -> [DatumPlane015,CopyPocket049,Sketch091,Pad038,Sketch092,Pad039,Sketch093,Pocket050,Pad040,Chamfer023]
  Origin = -> Origin014
  Tip = -> Chamfer023
FEATURE [Sketcher::SketchObject] Sketch094
  ArcFitTolerance = 1e-06
  AttachmentSupport = -> [Pocket049]
  ExternalGeometry = -> [Pocket049]
  FullyConstrained = true
  MakeInternals = false
  MapMode = 5
  Placement = pos=(0,-84,-8.9e-14) rot=(1,0,0;1.5708rad)
  sketch-geometry (7):
    g0: Circle CenterX=42 CenterY=14 CenterZ=0 NormalX=0 NormalY=0 NormalZ=1 AngleXU=0 Radius=3.125
    g1: ArcOfCircle CenterX=42 CenterY=14 CenterZ=0 NormalX=0 NormalY=0 NormalZ=1 AngleXU=0 Radius=5.75 StartAngle=0 EndAngle=3.14159
    g2: GeomPoint [constr] X=36.25 Y=14 Z=0
    g3: GeomPoint [constr] X=47.75 Y=14 Z=0
    g4: LineSegment StartX=36.25 StartY=14 StartZ=0 EndX=36.25 EndY=5 EndZ=0
    g5: LineSegment StartX=47.75 StartY=14 StartZ=0 EndX=47.75 EndY=5 EndZ=0
    g6: LineSegment StartX=47.75 StartY=5 StartZ=0 EndX=36.25 EndY=5 EndZ=0
  constraints (16):
    c: Coincident(g0,g-5)
    c: Equal(g0,g-5)
    c: Coincident(g1,g0)
    c: Tangent(g-4,g1)
    c: Horizontal(g3,g0)
    c: Horizontal(g0,g2)
    c: Coincident(g4,g2)
    c: PointOnObject(g4,g-6)
    c: Perpendicular(g-6,g4)
    c: Coincident(g5,g3)
    c: PointOnObject(g5,g-6)
    c: Vertical(g5)
    c: Coincident(g6,g5)
    c: Coincident(g6,g4)
    c: Coincident(g1,g4)
    c: Coincident(g1,g5)
FEATURE [PartDesign::Pad] Pad041
  BaseFeature = -> Pocket049
  Direction = (0,-1,-1.1e-15)
  Length = 8
  Length2 = 10
  Profile = -> Sketch094
  ReferenceAxis = -> Sketch094 [N_Axis]
  Refine = true
  Suppressed = false
  Type = 0
FEATURE [PartDesign::ShapeBinder] CopyChamfer020
  Placement = pos=(0,1e-15,-1.25) rot=(1,0,0;3.14159rad)
  TraceSupport = false
FEATURE [PartDesign::Plane] DatumPlane016
  AttachmentSupport = -> [CopyChamfer020]
  Length = 92.8744
  MapMode = 5
  Placement = pos=(10,1e-15,-1.25) rot=(0.57735,-0.57735,0.57735;4.18879rad)
  ResizeMode = 0
  Width = 69.6244
FEATURE [Sketcher::SketchObject] Sketch095
  ArcFitTolerance = 1e-06
  AttachmentSupport = -> [DatumPlane016]
  ExternalGeometry = -> [CopyChamfer020]
  FullyConstrained = true
  MakeInternals = false
  MapMode = 5
  Placement = pos=(10,1e-15,-1.25) rot=(0.57735,-0.57735,0.57735;4.18879rad)
  sketch-geometry (16):
    g0: Circle CenterX=22 CenterY=25 CenterZ=0 NormalX=0 NormalY=0 NormalZ=1 AngleXU=0 Radius=1.3
    g1: Circle CenterX=52 CenterY=25 CenterZ=0 NormalX=0 NormalY=0 NormalZ=1 AngleXU=0 Radius=1.3
    g2: LineSegment [constr] StartX=19.5 StartY=22.5 StartZ=0 EndX=24.5 EndY=22.5 EndZ=0
    g3: LineSegment [constr] StartX=24.5 StartY=22.5 StartZ=0 EndX=24.5 EndY=27.5 EndZ=0
    g4: LineSegment [constr] StartX=24.5 StartY=27.5 StartZ=0 EndX=19.5 EndY=27.5 EndZ=0
    g5: LineSegment [constr] StartX=19.5 StartY=27.5 StartZ=0 EndX=19.5 EndY=22.5 EndZ=0
    g6: GeomPoint [constr] X=22 Y=25 Z=0
    g7: LineSegment [constr] StartX=49.5 StartY=22.5 StartZ=0 EndX=54.5 EndY=22.5 EndZ=0
    g8: LineSegment [constr] StartX=54.5 StartY=22.5 StartZ=0 EndX=54.5 EndY=27.5 EndZ=0
    g9: LineSegment [constr] StartX=54.5 StartY=27.5 StartZ=0 EndX=49.5 EndY=27.5 EndZ=0
    g10: LineSegment [constr] StartX=49.5 StartY=27.5 StartZ=0 EndX=49.5 EndY=22.5 EndZ=0
    g11: GeomPoint [constr] X=52 Y=25 Z=0
    g12: LineSegment StartX=19.5 StartY=22.5 StartZ=0 EndX=54.5 EndY=22.5 EndZ=0
    g13: LineSegment StartX=54.5 StartY=22.5 StartZ=0 EndX=54.5 EndY=30 EndZ=0
    g14: LineSegment StartX=19.5 StartY=22.5 StartZ=0 EndX=19.5 EndY=30 EndZ=0
    g15: LineSegment StartX=19.5 StartY=30 StartZ=0 EndX=54.5 EndY=30 EndZ=0
  constraints (38):
    c: Coincident(g0,g-4)
    c: Equal(g0,g-4)
    c: Coincident(g1,g-7)
    c: Equal(g1,g-7)
    c: Coincident(g2,g3)
    c: Coincident(g3,g4)
    c: Coincident(g4,g5)
    c: Coincident(g5,g2)
    c: Horizontal(g2)
    c: Horizontal(g4)
    c: Vertical(g3)
    c: Vertical(g5)
    c: Symmetric(g4,g2,g6)
    c: Distance(g3,g5) = 5
    c: Distance(g2,g4) = 5
    c: Coincident(g6,g0)
    c: Coincident(g7,g8)
    c: Coincident(g8,g9)
    c: Coincident(g9,g10)
    c: Coincident(g10,g7)
    c: Horizontal(g7)
    c: Horizontal(g9)
    c: Vertical(g8)
    c: Vertical(g10)
    c: Symmetric(g9,g7,g11)
    c: Distance(g8,g10) = 5
    c: Distance(g7,g9) = 5
    c: Coincident(g11,g1)
    c: Coincident(g12,g2)
    c: Coincident(g12,g7)
    c: Coincident(g13,g7)
    c: PointOnObject(g13,g-3)
    c: Vertical(g13)
    c: Coincident(g14,g2)
    c: PointOnObject(g14,g-3)
    c: Vertical(g14)
    c: Coincident(g15,g14)
    c: Coincident(g15,g13)
FEATURE [PartDesign::Pad] Pad042
  Direction = (1,0,0)
  Length = 3
  Length2 = 10
  Placement = pos=(10,1e-15,-1.25) rot=(0.57735,-0.57735,0.57735;4.18879rad)
  Profile = -> Sketch095
  ReferenceAxis = -> Sketch095 [N_Axis]
  Refine = true
  Suppressed = false
  Type = 0
FEATURE [Sketcher::SketchObject] Sketch096
  ArcFitTolerance = 1e-06
  AttachmentSupport = -> [Pad042]
  ExternalGeometry = -> [Pad042]
  FullyConstrained = true
  MakeInternals = false
  MapMode = 5
  Placement = pos=(13,1e-15,-1.25) rot=(0.57735,-0.57735,0.57735;4.18879rad)
  sketch-geometry (4):
    g0: LineSegment StartX=19.5 StartY=30 StartZ=0 EndX=19.5 EndY=22.5 EndZ=0
    g1: LineSegment StartX=19.5 StartY=22.5 StartZ=0 EndX=54.5 EndY=22.5 EndZ=0
    g2: LineSegment StartX=54.5 StartY=22.5 StartZ=0 EndX=54.5 EndY=30 EndZ=0
    g3: LineSegment StartX=54.5 StartY=30 StartZ=0 EndX=19.5 EndY=30 EndZ=0
  constraints (10):
    c: Coincident(g0,g1)
    c: Coincident(g1,g2)
    c: Coincident(g2,g3)
    c: Coincident(g3,g0)
    c: Vertical(g0)
    c: Vertical(g2)
    c: Horizontal(g1)
    c: Horizontal(g3)
    c: Coincident(g0,g-4)
    c: Coincident(g1,g-3)
FEATURE [PartDesign::Pad] Pad043
  BaseFeature = -> Pad042
  Direction = (1,0,0)
  Length = 35
  Length2 = 10
  Placement = pos=(10,1e-15,-1.25) rot=(0.57735,-0.57735,0.57735;4.18879rad)
  Profile = -> Sketch096
  ReferenceAxis = -> Sketch096 [N_Axis]
  Refine = true
  Suppressed = false
  Type = 0
FEATURE [Sketcher::SketchObject] Sketch097
  ArcFitTolerance = 1e-06
  AttachmentSupport = -> [Pad043]
  ExternalGeometry = -> [Pad043,CopyChamfer020]
  FullyConstrained = true
  MakeInternals = false
  MapMode = 5
  Placement = pos=(10,1e-15,-23.75) rot=(0,0,-1;1.5708rad)
  sketch-geometry (11):
    g0: LineSegment [constr] StartX=22.25 StartY=5.5 StartZ=0 EndX=51.75 EndY=5.5 EndZ=0
    g1: LineSegment [constr] StartX=51.75 StartY=5.5 StartZ=0 EndX=51.75 EndY=32.5 EndZ=0
    g2: LineSegment [constr] StartX=51.75 StartY=32.5 StartZ=0 EndX=22.25 EndY=32.5 EndZ=0
    g3: LineSegment [constr] StartX=22.25 StartY=32.5 StartZ=0 EndX=22.25 EndY=5.5 EndZ=0
    g4: GeomPoint [constr] X=37 Y=19 Z=0
    g5: GeomPoint X=37 Y=38 Z=0
    g6: GeomPoint X=19.5 Y=19 Z=0
    g7: Circle CenterX=22.25 CenterY=32.5 CenterZ=0 NormalX=0 NormalY=0 NormalZ=1 AngleXU=0 Radius=1.3
    g8: Circle CenterX=51.75 CenterY=32.5 CenterZ=0 NormalX=0 NormalY=0 NormalZ=1 AngleXU=0 Radius=1.3
    g9: Circle CenterX=51.75 CenterY=5.5 CenterZ=0 NormalX=0 NormalY=0 NormalZ=1 AngleXU=0 Radius=1.3
    g10: Circle CenterX=22.25 CenterY=5.5 CenterZ=0 NormalX=0 NormalY=0 NormalZ=1 AngleXU=0 Radius=1.3
  constraints (23):
    c: Coincident(g0,g1)
    c: Coincident(g1,g2)
    c: Coincident(g2,g3)
    c: Coincident(g3,g0)
    c: Horizontal(g0)
    c: Horizontal(g2)
    c: Vertical(g1)
    c: Vertical(g3)
    c: Symmetric(g2,g0,g4)
    c: Distance(g1,g3) = 29.5
    c: Distance(g0,g2) = 27
    c: Symmetric(g-3,g-3,g5)
    c: Symmetric(g-4,g-4,g6)
    c: Vertical(g4,g5)
    c: Horizontal(g4,g6)
    c: Diameter(g7) = 2.6
    c: Coincident(g7,g2)
    c: Coincident(g8,g1)
    c: Coincident(g9,g0)
    c: Coincident(g10,g0)
    c: Equal(g10,g7)
    c: Equal(g7,g8)
    c: Equal(g8,g9)
FEATURE [PartDesign::Pocket] Pocket051
  BaseFeature = -> Pad043
  Direction = (0,0,-1)
  Length = 5
  Length2 = 5
  Placement = pos=(10,1e-15,-1.25) rot=(0.57735,-0.57735,0.57735;4.18879rad)
  Profile = -> Sketch097
  ReferenceAxis = -> Sketch097 [N_Axis]
  Refine = true
  Suppressed = false
  Type = 1
FEATURE [Sketcher::SketchObject] Sketch098
  ArcFitTolerance = 1e-06
  AttachmentSupport = -> [Pocket051]
  ExternalGeometry = -> [Pocket051]
  FullyConstrained = true
  MakeInternals = false
  MapMode = 5
  Placement = pos=(10,1e-15,-23.75) rot=(0,0,-1;1.5708rad)
  sketch-geometry (7):
    g0: LineSegment StartX=24.5 StartY=6.5 StartZ=0 EndX=49.5 EndY=6.5 EndZ=0
    g1: LineSegment StartX=49.5 StartY=6.5 StartZ=0 EndX=49.5 EndY=31.5 EndZ=0
    g2: LineSegment StartX=49.5 StartY=31.5 StartZ=0 EndX=24.5 EndY=31.5 EndZ=0
    g3: LineSegment StartX=24.5 StartY=31.5 StartZ=0 EndX=24.5 EndY=6.5 EndZ=0
    g4: GeomPoint [constr] X=37 Y=19 Z=0
    g5: GeomPoint X=37 Y=38 Z=0
    g6: GeomPoint X=54.5 Y=19 Z=0
  constraints (15):
    c: Coincident(g0,g1)
    c: Coincident(g1,g2)
    c: Coincident(g2,g3)
    c: Coincident(g3,g0)
    c: Horizontal(g0)
    c: Horizontal(g2)
    c: Vertical(g1)
    c: Vertical(g3)
    c: Symmetric(g2,g0,g4)
    c: Distance(g1,g3) = 25
    c: Distance(g0,g2) = 25
    c: Symmetric(g-4,g-4,g5)
    c: Symmetric(g-3,g-3,g6)
    c: Horizontal(g4,g6)
    c: Vertical(g4,g5)
FEATURE [PartDesign::Pocket] Pocket052
  BaseFeature = -> Pocket051
  Direction = (0,0,-1)
  Length = 5
  Length2 = 5
  Placement = pos=(10,1e-15,-1.25) rot=(0.57735,-0.57735,0.57735;4.18879rad)
  Profile = -> Sketch098
  ReferenceAxis = -> Sketch098 [N_Axis]
  Refine = true
  Suppressed = false
  Type = 1
FEATURE [PartDesign::Chamfer] Chamfer024
  Angle = 45
  Base = -> Pocket052 [Edge19,Edge30]
  BaseFeature = -> Pocket052
  ChamferType = 0
  FlipDirection = false
  Placement = pos=(10,1e-15,-1.25) rot=(0.57735,-0.57735,0.57735;4.18879rad)
  Refine = true
  Size = 4
  Size2 = 1
  SupportTransform = false
  Suppressed = false
  UseAllEdges = false
FEATURE [PartDesign::Chamfer] Chamfer025
  Angle = 45
  Base = -> Chamfer024 [Edge37,Edge40,Edge35,Edge38]
  BaseFeature = -> Chamfer024
  ChamferType = 0
  FlipDirection = false
  Placement = pos=(10,1e-15,-1.25) rot=(0.57735,-0.57735,0.57735;4.18879rad)
  Refine = true
  Size = 3
  Size2 = 1
  SupportTransform = false
  Suppressed = false
  UseAllEdges = false
FEATURE [PartDesign::Body] Body015  label="ULN2003 Module Mount"
  AllowCompound = false
  Group = -> [DatumPlane016,CopyChamfer020,Sketch095,Pad042,Sketch096,Pad043,Sketch097,Pocket051,Sketch098,Pocket052,Chamfer024,Chamfer025]
  Origin = -> Origin015
  Tip = -> Chamfer025
FEATURE [Sketcher::SketchObject] Sketch106
  ArcFitTolerance = 1e-06
  AttachmentSupport = -> [Pad041]
  ExternalGeometry = -> [Pad041]
  FullyConstrained = true
  MakeInternals = false
  MapMode = 5
  Placement = pos=(0,-122,9.27e-14) rot=(1,0,0;1.5708rad)
  sketch-geometry (18):
    g0: LineSegment [constr] StartX=0 StartY=5 StartZ=0 EndX=5 EndY=5 EndZ=0
    g1: LineSegment [constr] StartX=5 StartY=5 StartZ=0 EndX=10.495 EndY=5 EndZ=0
    g2: LineSegment [constr] StartX=10.495 StartY=5 StartZ=0 EndX=15.495 EndY=5 EndZ=0
    g3: LineSegment [constr] StartX=5 StartY=5 StartZ=0 EndX=5 EndY=-1.25 EndZ=0
    g4: LineSegment [constr] StartX=10.495 StartY=5 StartZ=0 EndX=10.495 EndY=-1.25 EndZ=0
    g5: LineSegment [constr] StartX=15.495 StartY=5 StartZ=0 EndX=15.495 EndY=-1.25 EndZ=0
    g6: LineSegment [constr] StartX=84 StartY=5 StartZ=0 EndX=79 EndY=5 EndZ=0
    g7: LineSegment [constr] StartX=79 StartY=5 StartZ=0 EndX=73.505 EndY=5 EndZ=0
    g8: LineSegment [constr] StartX=73.505 StartY=5 StartZ=0 EndX=68.505 EndY=5 EndZ=0
    g9: LineSegment [constr] StartX=68.505 StartY=5 StartZ=0 EndX=68.505 EndY=-1.25 EndZ=0
    g10: LineSegment [constr] StartX=73.505 StartY=5 StartZ=0 EndX=73.505 EndY=-1.25 EndZ=0
    g11: LineSegment [constr] StartX=79 StartY=5 StartZ=0 EndX=79 EndY=-1.25 EndZ=0
    g12: Circle CenterX=5 CenterY=1.875 CenterZ=0 NormalX=0 NormalY=0 NormalZ=1 AngleXU=0 Radius=1.3
    g13: Circle CenterX=10.495 CenterY=1.875 CenterZ=0 NormalX=0 NormalY=0 NormalZ=1 AngleXU=0 Radius=1.3
    g14: Circle CenterX=15.495 CenterY=1.875 CenterZ=0 NormalX=0 NormalY=0 NormalZ=1 AngleXU=0 Radius=1.3
    g15: Circle CenterX=68.505 CenterY=1.875 CenterZ=0 NormalX=0 NormalY=0 NormalZ=1 AngleXU=0 Radius=1.3
    g16: Circle CenterX=73.505 CenterY=1.875 CenterZ=0 NormalX=0 NormalY=0 NormalZ=1 AngleXU=0 Radius=1.3
    g17: Circle CenterX=79 CenterY=1.875 CenterZ=0 NormalX=0 NormalY=0 NormalZ=1 AngleXU=0 Radius=1.3
  constraints (46):
    c: Distance(g0) = 5
    c: Coincident(g0,g-3)
    c: PointOnObject(g0,g-3)
    c: Coincident(g1,g0)
    c: Symmetric(g-3,g-3,g1)
    c: Distance(g2) = 5
    c: Coincident(g2,g1)
    c: PointOnObject(g2,g-3)
    c: Coincident(g3,g0)
    c: PointOnObject(g3,g-5)
    c: Vertical(g3)
    c: Coincident(g4,g1)
    c: PointOnObject(g4,g-5)
    c: Vertical(g4)
    c: Coincident(g5,g2)
    c: PointOnObject(g5,g-5)
    c: Vertical(g5)
    c: Distance(g6) = 5
    c: Coincident(g6,g-4)
    c: PointOnObject(g6,g-4)
    c: Coincident(g7,g6)
    c: Symmetric(g-4,g-4,g7)
    c: Distance(g8) = 5
    c: Coincident(g8,g7)
    c: PointOnObject(g8,g-4)
    c: Coincident(g9,g8)
    c: PointOnObject(g9,g-5)
    c: Vertical(g9)
    c: Coincident(g10,g7)
    c: PointOnObject(g10,g-5)
    c: Vertical(g10)
    c: Coincident(g11,g6)
    c: PointOnObject(g11,g-5)
    c: Vertical(g11)
    c: Diameter(g12) = 2.6
    c: Symmetric(g3,g3,g12)
    c: Diameter(g13) = 2.6
    c: Symmetric(g4,g4,g13)
    c: Diameter(g14) = 2.6
    c: Symmetric(g5,g5,g14)
    c: Diameter(g15) = 2.6
    c: Symmetric(g9,g9,g15)
    c: Diameter(g16) = 2.6
    c: Symmetric(g10,g10,g16)
    c: Diameter(g17) = 2.6
    c: Symmetric(g11,g11,g17)
FEATURE [PartDesign::Pocket] Pocket056
  BaseFeature = -> Pad041
  Direction = (0,1,-2e-16)
  Length = 5
  Length2 = 5
  Profile = -> Sketch106
  ReferenceAxis = -> Sketch106 [N_Axis]
  Refine = true
  Suppressed = false
  Type = 0
FEATURE [PartDesign::Body] Body007  label="Base"
  AllowCompound = false
  Group = -> [Clone001,Sketch028,Pocket009,Sketch029,Pocket010,Sketch057,Pocket028,Sketch058,Pocket029,Sketch059,Pad025,DatumPlane011,CopyBinBase,Binder,Binder001,Binder002,Binder003,Binder004,Sketch060,Pocket030,Sketch065,Pad026,Sketch075,Pad033,Sketch076,Pocket039,Sketch090,Pocket049,Sketch094,Pad041,Sketch106,Pocket056]
  Origin = -> Origin007
  Placement = pos=(-93,0,0) rot=(0,0,1;0rad)
  Tip = -> Pocket056
FEATURE [Sketcher::SketchObject] Sketch107
  ArcFitTolerance = 1e-06
  AttachmentSupport = -> [Chamfer017]
  ExternalGeometry = -> [Chamfer017]
  FullyConstrained = true
  MakeInternals = false
  MapMode = 5
  Placement = pos=(42,-84,15.55) rot=(1,0,0;3.14159rad)
  sketch-geometry (2):
    g0: LineSegment [constr] StartX=0 StartY=35 StartZ=0 EndX=0 EndY=29 EndZ=0
    g1: Circle CenterX=0 CenterY=32 CenterZ=0 NormalX=0 NormalY=0 NormalZ=1 AngleXU=0 Radius=0.85
  constraints (4):
    c: Symmetric(g-3,g-3,g0)
    c: Symmetric(g-4,g-4,g0)
    c: Diameter(g1) = 1.7
    c: Symmetric(g0,g0,g1)
FEATURE [PartDesign::Pocket] Pocket057
  BaseFeature = -> Chamfer017
  Direction = (0,0,1)
  Length = 5
  Length2 = 5
  Placement = pos=(42,-84,14) rot=(0.57735,-0.57735,0.57735;2.0944rad)
  Profile = -> Sketch107
  ReferenceAxis = -> Sketch107 [N_Axis]
  Refine = true
  Suppressed = false
  Type = 1
FEATURE [PartDesign::Body] Body005  label="Adjuster"
  AllowCompound = false
  Group = -> [ShapeBinder003,DatumPlane006,Sketch019,Pad009,Sketch020,Pad010,Sketch021,Pad011,Sketch022,Pocket007,Fillet004,DatumPoint,VThreadProfile,Helix,AdditivePipe,ShapeBinder004,DatumPlane007,Sketch023,Pad012,Sketch035,Pocket013,Sketch036,Pocket014,Sketch055,Pad024,Sketch056,Pocket027,Sketch066,Pocket036,Sketch067,Pocket037,Sketch068,Pad027,Chamfer017,Sketch107,Pocket057]
  Origin = -> Origin005
  Placement = pos=(-93,0,0) rot=(0,0,1;0rad)
  Tip = -> Pocket057
